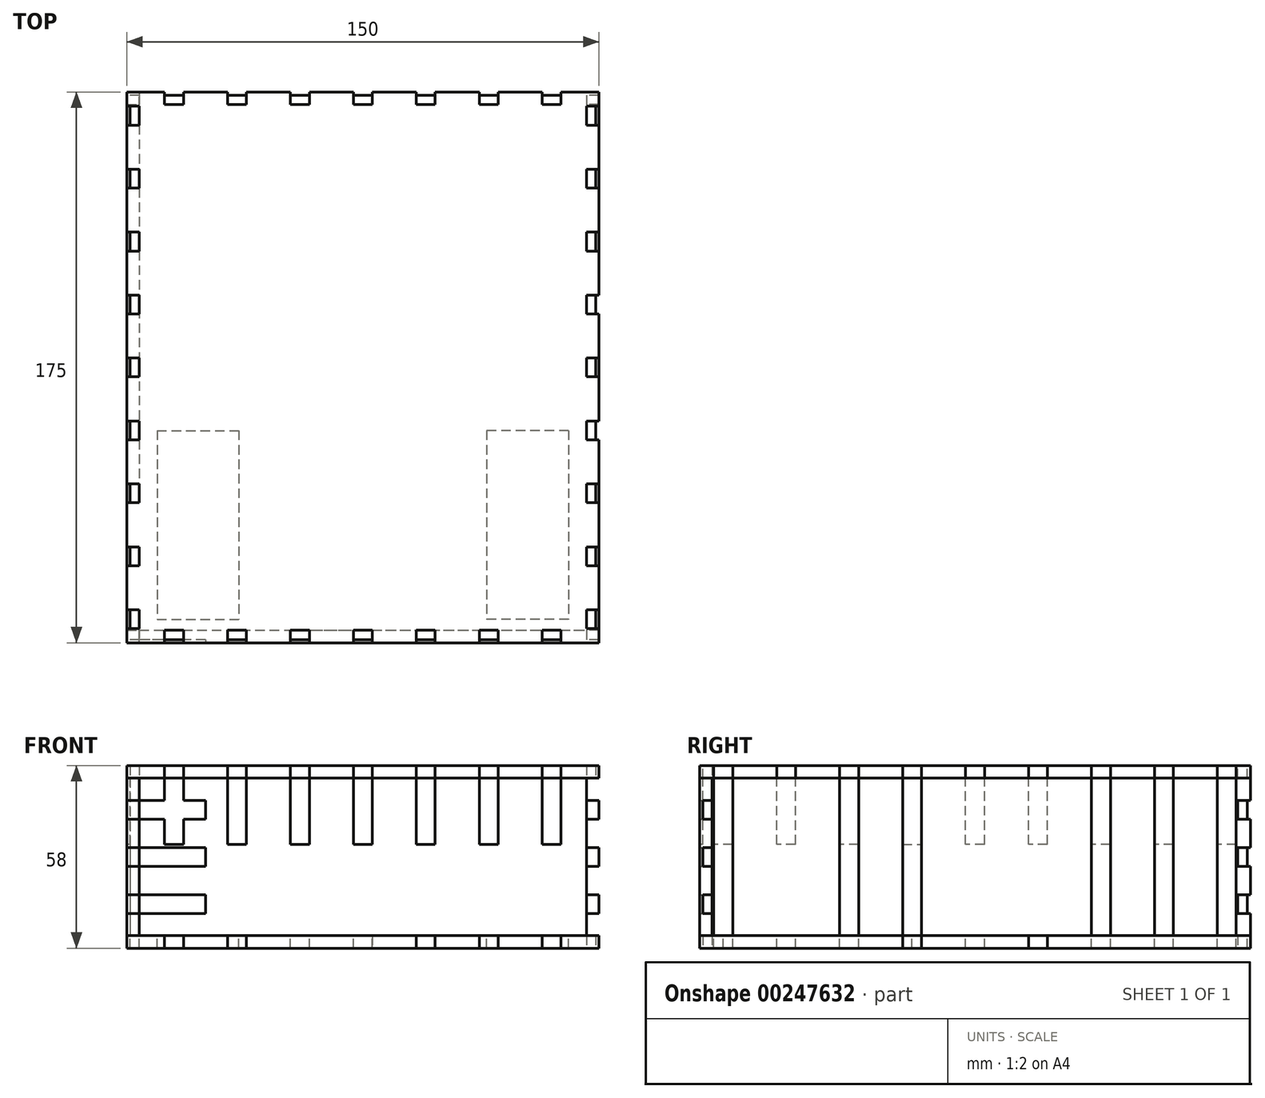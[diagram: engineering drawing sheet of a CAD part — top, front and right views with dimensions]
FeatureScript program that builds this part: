
annotation { "Feature Type Name" : "Feature", "Feature Type Description" : "" }
export const myFeature = defineFeature(function(context is Context, id is Id, definition is map)
    precondition{}
    {
        {
            var Q0;
            Q0=qCreatedBy(makeId("Top.planeOp"),FACE);
            var sketch = newSketch(context, id + "F0", { "sketchPlane" : qUnion([Q0])});
            skLineSegment(sketch, "E0.bottom", {"start": v(-75, 87.5) * mm, "end": v(75, 87.5) * mm});
            skLineSegment(sketch, "E0.top", {"start": v(-75, -87.5) * mm, "end": v(75, -87.5) * mm});
            skLineSegment(sketch, "E0.left", {"start": v(-75, 87.5) * mm, "end": v(-75, -87.5) * mm});
            skLineSegment(sketch, "E0.right", {"start": v(75, 87.5) * mm, "end": v(75, -87.5) * mm});
            skPoint(sketch, "E0.middle", {"position": v(0, 0) * mm});
            skLineSegment(sketch, "E1", {"start": v(-75, 87.5) * mm, "end": v(75, -87.5) * mm, "construction": true});
            skLineSegment(sketch, "E2", {"start": v(-75, 0) * mm, "end": v(75, 0) * mm, "construction": true});
            skLineSegment(sketch, "E3", {"start": v(0, 87.5) * mm, "end": v(0, -87.5) * mm, "construction": true});
            skLineSegment(sketch, "E4.bottom", {"start": v(-74, 3) * mm, "end": v(-71, 3) * mm});
            skLineSegment(sketch, "E4.top", {"start": v(-74, 0) * mm, "end": v(-71, 0) * mm});
            skLineSegment(sketch, "E4.left", {"start": v(-74, 3) * mm, "end": v(-74, 0) * mm});
            skLineSegment(sketch, "E4.right", {"start": v(-71, 3) * mm, "end": v(-71, 0) * mm});
            skLineSegment(sketch, "E5.MirrorCS", {"start": v(-74, -3) * mm, "end": v(-71, -3) * mm});
            skLineSegment(sketch, "E6.MirrorCS", {"start": v(-74, -3) * mm, "end": v(-74, 0) * mm});
            skLineSegment(sketch, "E7.MirrorCS", {"start": v(-71, -3) * mm, "end": v(-71, 0) * mm});
            skLineSegment(sketch, "E8.0.1.0", {"start": v(-74, 23) * mm, "end": v(-71, 23) * mm});
            skLineSegment(sketch, "E8.0.1.1", {"start": v(-74, 23) * mm, "end": v(-74, 20) * mm});
            skLineSegment(sketch, "E8.0.1.2", {"start": v(-74, 17) * mm, "end": v(-74, 20) * mm});
            skLineSegment(sketch, "E8.0.1.3", {"start": v(-74, 17) * mm, "end": v(-71, 17) * mm});
            skLineSegment(sketch, "E8.0.1.4", {"start": v(-71, 17) * mm, "end": v(-71, 20) * mm});
            skLineSegment(sketch, "E8.0.1.5", {"start": v(-71, 23) * mm, "end": v(-71, 20) * mm});
            skLineSegment(sketch, "E8.0.2.0", {"start": v(-74, 43) * mm, "end": v(-71, 43) * mm});
            skLineSegment(sketch, "E8.0.2.1", {"start": v(-74, 43) * mm, "end": v(-74, 40) * mm});
            skLineSegment(sketch, "E8.0.2.2", {"start": v(-74, 37) * mm, "end": v(-74, 40) * mm});
            skLineSegment(sketch, "E8.0.2.3", {"start": v(-74, 37) * mm, "end": v(-71, 37) * mm});
            skLineSegment(sketch, "E8.0.2.4", {"start": v(-71, 37) * mm, "end": v(-71, 40) * mm});
            skLineSegment(sketch, "E8.0.2.5", {"start": v(-71, 43) * mm, "end": v(-71, 40) * mm});
            skLineSegment(sketch, "E8.0.3.0", {"start": v(-74, 63) * mm, "end": v(-71, 63) * mm});
            skLineSegment(sketch, "E8.0.3.1", {"start": v(-74, 63) * mm, "end": v(-74, 60) * mm});
            skLineSegment(sketch, "E8.0.3.2", {"start": v(-74, 57) * mm, "end": v(-74, 60) * mm});
            skLineSegment(sketch, "E8.0.3.3", {"start": v(-74, 57) * mm, "end": v(-71, 57) * mm});
            skLineSegment(sketch, "E8.0.3.4", {"start": v(-71, 57) * mm, "end": v(-71, 60) * mm});
            skLineSegment(sketch, "E8.0.3.5", {"start": v(-71, 63) * mm, "end": v(-71, 60) * mm});
            skLineSegment(sketch, "E8.0.4.0", {"start": v(-74, 83) * mm, "end": v(-71, 83) * mm});
            skLineSegment(sketch, "E8.0.4.1", {"start": v(-74, 83) * mm, "end": v(-74, 80) * mm});
            skLineSegment(sketch, "E8.0.4.2", {"start": v(-74, 77) * mm, "end": v(-74, 80) * mm});
            skLineSegment(sketch, "E8.0.4.3", {"start": v(-74, 77) * mm, "end": v(-71, 77) * mm});
            skLineSegment(sketch, "E8.0.4.4", {"start": v(-71, 77) * mm, "end": v(-71, 80) * mm});
            skLineSegment(sketch, "E8.0.4.5", {"start": v(-71, 83) * mm, "end": v(-71, 80) * mm});
            skLineSegment(sketch, "E8.direction1", {"start": v(-74, 3) * mm, "end": v(-49, 3) * mm, "construction": true});
            skLineSegment(sketch, "E8.direction2", {"start": v(-74, 3) * mm, "end": v(-74, 23) * mm, "construction": true});
            skLineSegment(sketch, "E9.MirrorCS", {"start": v(-74, -17) * mm, "end": v(-71, -17) * mm});
            skLineSegment(sketch, "E10.MirrorCS", {"start": v(-71, -17) * mm, "end": v(-71, -20) * mm});
            skLineSegment(sketch, "E11.MirrorCS", {"start": v(-71, -23) * mm, "end": v(-71, -20) * mm});
            skLineSegment(sketch, "E12.MirrorCS", {"start": v(-74, -23) * mm, "end": v(-71, -23) * mm});
            skLineSegment(sketch, "E13.MirrorCS", {"start": v(-74, -37) * mm, "end": v(-71, -37) * mm});
            skLineSegment(sketch, "E14.MirrorCS", {"start": v(-74, -37) * mm, "end": v(-74, -40) * mm});
            skLineSegment(sketch, "E15.MirrorCS", {"start": v(-74, -43) * mm, "end": v(-74, -40) * mm});
            skLineSegment(sketch, "E16.MirrorCS", {"start": v(-74, -43) * mm, "end": v(-71, -43) * mm});
            skLineSegment(sketch, "E17.MirrorCS", {"start": v(-71, -37) * mm, "end": v(-71, -40) * mm});
            skLineSegment(sketch, "E18.MirrorCS", {"start": v(-71, -43) * mm, "end": v(-71, -40) * mm});
            skLineSegment(sketch, "E19.MirrorCS", {"start": v(-74, -57) * mm, "end": v(-74, -60) * mm});
            skLineSegment(sketch, "E20.MirrorCS", {"start": v(-74, -63) * mm, "end": v(-74, -60) * mm});
            skLineSegment(sketch, "E21.MirrorCS", {"start": v(-74, -63) * mm, "end": v(-71, -63) * mm});
            skLineSegment(sketch, "E22.MirrorCS", {"start": v(-71, -63) * mm, "end": v(-71, -60) * mm});
            skLineSegment(sketch, "E23.MirrorCS", {"start": v(-71, -57) * mm, "end": v(-71, -60) * mm});
            skLineSegment(sketch, "E24.MirrorCS", {"start": v(-74, -57) * mm, "end": v(-71, -57) * mm});
            skLineSegment(sketch, "E25.MirrorCS", {"start": v(-71, -77) * mm, "end": v(-71, -80) * mm});
            skLineSegment(sketch, "E26.MirrorCS", {"start": v(-71, -83) * mm, "end": v(-71, -80) * mm});
            skLineSegment(sketch, "E27.MirrorCS", {"start": v(-74, -83) * mm, "end": v(-71, -83) * mm});
            skLineSegment(sketch, "E28.MirrorCS", {"start": v(-74, -77) * mm, "end": v(-74, -80) * mm});
            skLineSegment(sketch, "E29.MirrorCS", {"start": v(-74, -77) * mm, "end": v(-71, -77) * mm});
            skLineSegment(sketch, "E30.MirrorCS", {"start": v(-74, -83) * mm, "end": v(-74, -80) * mm});
            skLineSegment(sketch, "E31", {"start": v(-74, -23) * mm, "end": v(-74, -17) * mm});
            skLineSegment(sketch, "E32.bottom", {"start": v(0, -83.5) * mm, "end": v(3, -83.5) * mm});
            skLineSegment(sketch, "E32.top", {"start": v(0, -86.5) * mm, "end": v(3, -86.5) * mm});
            skLineSegment(sketch, "E32.left", {"start": v(0, -83.5) * mm, "end": v(0, -86.5) * mm});
            skLineSegment(sketch, "E32.right", {"start": v(3, -83.5) * mm, "end": v(3, -86.5) * mm});
            skLineSegment(sketch, "E33.MirrorCS", {"start": v(0, -83.5) * mm, "end": v(-3, -83.5) * mm});
            skLineSegment(sketch, "E34.MirrorCS", {"start": v(-3, -83.5) * mm, "end": v(-3, -86.5) * mm});
            skLineSegment(sketch, "E35.MirrorCS", {"start": v(0, -86.5) * mm, "end": v(-3, -86.5) * mm});
            skLineSegment(sketch, "E36.1.0.0", {"start": v(20, -83.5) * mm, "end": v(17, -83.5) * mm});
            skLineSegment(sketch, "E36.1.0.1", {"start": v(20, -83.5) * mm, "end": v(23, -83.5) * mm});
            skLineSegment(sketch, "E36.1.0.2", {"start": v(20, -86.5) * mm, "end": v(17, -86.5) * mm});
            skLineSegment(sketch, "E36.1.0.3", {"start": v(17, -83.5) * mm, "end": v(17, -86.5) * mm});
            skLineSegment(sketch, "E36.1.0.4", {"start": v(20, -86.5) * mm, "end": v(23, -86.5) * mm});
            skLineSegment(sketch, "E36.1.0.5", {"start": v(23, -83.5) * mm, "end": v(23, -86.5) * mm});
            skLineSegment(sketch, "E36.2.0.0", {"start": v(40, -83.5) * mm, "end": v(37, -83.5) * mm});
            skLineSegment(sketch, "E36.2.0.1", {"start": v(40, -83.5) * mm, "end": v(43, -83.5) * mm});
            skLineSegment(sketch, "E36.2.0.2", {"start": v(40, -86.5) * mm, "end": v(37, -86.5) * mm});
            skLineSegment(sketch, "E36.2.0.3", {"start": v(37, -83.5) * mm, "end": v(37, -86.5) * mm});
            skLineSegment(sketch, "E36.2.0.4", {"start": v(40, -86.5) * mm, "end": v(43, -86.5) * mm});
            skLineSegment(sketch, "E36.2.0.5", {"start": v(43, -83.5) * mm, "end": v(43, -86.5) * mm});
            skLineSegment(sketch, "E36.3.0.0", {"start": v(60, -83.5) * mm, "end": v(57, -83.5) * mm});
            skLineSegment(sketch, "E36.3.0.1", {"start": v(60, -83.5) * mm, "end": v(63, -83.5) * mm});
            skLineSegment(sketch, "E36.3.0.2", {"start": v(60, -86.5) * mm, "end": v(57, -86.5) * mm});
            skLineSegment(sketch, "E36.3.0.3", {"start": v(57, -83.5) * mm, "end": v(57, -86.5) * mm});
            skLineSegment(sketch, "E36.3.0.4", {"start": v(60, -86.5) * mm, "end": v(63, -86.5) * mm});
            skLineSegment(sketch, "E36.3.0.5", {"start": v(63, -83.5) * mm, "end": v(63, -86.5) * mm});
            skLineSegment(sketch, "E36.direction1", {"start": v(-3, -83.5) * mm, "end": v(17, -83.5) * mm, "construction": true});
            skLineSegment(sketch, "E37.MirrorCS", {"start": v(-20, -83.5) * mm, "end": v(-17, -83.5) * mm});
            skLineSegment(sketch, "E38.MirrorCS", {"start": v(-20, -83.5) * mm, "end": v(-23, -83.5) * mm});
            skLineSegment(sketch, "E39.MirrorCS", {"start": v(-23, -83.5) * mm, "end": v(-23, -86.5) * mm});
            skLineSegment(sketch, "E40.MirrorCS", {"start": v(-20, -86.5) * mm, "end": v(-23, -86.5) * mm});
            skLineSegment(sketch, "E41.MirrorCS", {"start": v(-20, -86.5) * mm, "end": v(-17, -86.5) * mm});
            skLineSegment(sketch, "E42.MirrorCS", {"start": v(-17, -83.5) * mm, "end": v(-17, -86.5) * mm});
            skLineSegment(sketch, "E43.MirrorCS", {"start": v(-40, -83.5) * mm, "end": v(-43, -83.5) * mm});
            skLineSegment(sketch, "E44.MirrorCS", {"start": v(-40, -83.5) * mm, "end": v(-37, -83.5) * mm});
            skLineSegment(sketch, "E45.MirrorCS", {"start": v(-37, -83.5) * mm, "end": v(-37, -86.5) * mm});
            skLineSegment(sketch, "E46.MirrorCS", {"start": v(75, -87.5) * mm, "end": v(-75, -87.5) * mm});
            skLineSegment(sketch, "E47.MirrorCS", {"start": v(-40, -86.5) * mm, "end": v(-37, -86.5) * mm});
            skLineSegment(sketch, "E48.MirrorCS", {"start": v(-40, -86.5) * mm, "end": v(-43, -86.5) * mm});
            skLineSegment(sketch, "E49.MirrorCS", {"start": v(-43, -83.5) * mm, "end": v(-43, -86.5) * mm});
            skLineSegment(sketch, "E50.MirrorCS", {"start": v(-60, -83.5) * mm, "end": v(-57, -83.5) * mm});
            skLineSegment(sketch, "E51.MirrorCS", {"start": v(-60, -83.5) * mm, "end": v(-63, -83.5) * mm});
            skLineSegment(sketch, "E52.MirrorCS", {"start": v(-63, -83.5) * mm, "end": v(-63, -86.5) * mm});
            skLineSegment(sketch, "E53.MirrorCS", {"start": v(-60, -86.5) * mm, "end": v(-63, -86.5) * mm});
            skLineSegment(sketch, "E54.MirrorCS", {"start": v(-60, -86.5) * mm, "end": v(-57, -86.5) * mm});
            skLineSegment(sketch, "E55.MirrorCS", {"start": v(-57, -83.5) * mm, "end": v(-57, -86.5) * mm});
            skLineSegment(sketch, "E56.MirrorCS", {"start": v(74, 83) * mm, "end": v(71, 83) * mm});
            skLineSegment(sketch, "E57.MirrorCS", {"start": v(74, 83) * mm, "end": v(74, 80) * mm});
            skLineSegment(sketch, "E58.MirrorCS", {"start": v(71, 83) * mm, "end": v(71, 80) * mm});
            skLineSegment(sketch, "E59.MirrorCS", {"start": v(71, 77) * mm, "end": v(71, 80) * mm});
            skLineSegment(sketch, "E60.MirrorCS", {"start": v(74, 77) * mm, "end": v(71, 77) * mm});
            skLineSegment(sketch, "E61.MirrorCS", {"start": v(74, 77) * mm, "end": v(74, 80) * mm});
            skLineSegment(sketch, "E62.MirrorCS", {"start": v(74, 63) * mm, "end": v(71, 63) * mm});
            skLineSegment(sketch, "E63.MirrorCS", {"start": v(74, 63) * mm, "end": v(74, 60) * mm});
            skLineSegment(sketch, "E64.MirrorCS", {"start": v(71, 63) * mm, "end": v(71, 60) * mm});
            skLineSegment(sketch, "E65.MirrorCS", {"start": v(71, 57) * mm, "end": v(71, 60) * mm});
            skLineSegment(sketch, "E66.MirrorCS", {"start": v(74, 57) * mm, "end": v(71, 57) * mm});
            skLineSegment(sketch, "E67.MirrorCS", {"start": v(74, 57) * mm, "end": v(74, 60) * mm});
            skLineSegment(sketch, "E68.MirrorCS", {"start": v(74, 43) * mm, "end": v(71, 43) * mm});
            skLineSegment(sketch, "E69.MirrorCS", {"start": v(74, 43) * mm, "end": v(74, 40) * mm});
            skLineSegment(sketch, "E70.MirrorCS", {"start": v(71, 43) * mm, "end": v(71, 40) * mm});
            skLineSegment(sketch, "E71.MirrorCS", {"start": v(71, 37) * mm, "end": v(71, 40) * mm});
            skLineSegment(sketch, "E72.MirrorCS", {"start": v(74, 37) * mm, "end": v(74, 40) * mm});
            skLineSegment(sketch, "E73.MirrorCS", {"start": v(74, 37) * mm, "end": v(71, 37) * mm});
            skLineSegment(sketch, "E74.MirrorCS", {"start": v(74, 23) * mm, "end": v(71, 23) * mm});
            skLineSegment(sketch, "E75.MirrorCS", {"start": v(71, 23) * mm, "end": v(71, 20) * mm});
            skLineSegment(sketch, "E76.MirrorCS", {"start": v(74, 3) * mm, "end": v(74, 23) * mm, "construction": true});
            skLineSegment(sketch, "E77.MirrorCS", {"start": v(74, 17) * mm, "end": v(71, 17) * mm});
            skLineSegment(sketch, "E78.MirrorCS", {"start": v(71, 17) * mm, "end": v(71, 20) * mm});
            skLineSegment(sketch, "E79.MirrorCS", {"start": v(74, 3) * mm, "end": v(49, 3) * mm, "construction": true});
            skLineSegment(sketch, "E80.MirrorCS", {"start": v(74, 3) * mm, "end": v(74, 0) * mm});
            skLineSegment(sketch, "E81.MirrorCS", {"start": v(71, 3) * mm, "end": v(71, 0) * mm});
            skLineSegment(sketch, "E82.MirrorCS", {"start": v(74, -3) * mm, "end": v(71, -3) * mm});
            skLineSegment(sketch, "E83.MirrorCS", {"start": v(74, -3) * mm, "end": v(74, 0) * mm});
            skLineSegment(sketch, "E84.MirrorCS", {"start": v(71, -3) * mm, "end": v(71, 0) * mm});
            skLineSegment(sketch, "E85.MirrorCS", {"start": v(74, -17) * mm, "end": v(71, -17) * mm});
            skLineSegment(sketch, "E86.MirrorCS", {"start": v(74, -23) * mm, "end": v(74, -17) * mm});
            skLineSegment(sketch, "E87.MirrorCS", {"start": v(71, -17) * mm, "end": v(71, -20) * mm});
            skLineSegment(sketch, "E88.MirrorCS", {"start": v(71, -23) * mm, "end": v(71, -20) * mm});
            skLineSegment(sketch, "E89.MirrorCS", {"start": v(74, -23) * mm, "end": v(71, -23) * mm});
            skLineSegment(sketch, "E90.MirrorCS", {"start": v(74, -37) * mm, "end": v(71, -37) * mm});
            skLineSegment(sketch, "E91.MirrorCS", {"start": v(74, -37) * mm, "end": v(74, -40) * mm});
            skLineSegment(sketch, "E92.MirrorCS", {"start": v(71, -37) * mm, "end": v(71, -40) * mm});
            skLineSegment(sketch, "E93.MirrorCS", {"start": v(71, -43) * mm, "end": v(71, -40) * mm});
            skLineSegment(sketch, "E94.MirrorCS", {"start": v(74, -43) * mm, "end": v(74, -40) * mm});
            skLineSegment(sketch, "E95.MirrorCS", {"start": v(74, -43) * mm, "end": v(71, -43) * mm});
            skLineSegment(sketch, "E96.MirrorCS", {"start": v(74, -57) * mm, "end": v(71, -57) * mm});
            skLineSegment(sketch, "E97.MirrorCS", {"start": v(74, -57) * mm, "end": v(74, -60) * mm});
            skLineSegment(sketch, "E98.MirrorCS", {"start": v(74, -63) * mm, "end": v(74, -60) * mm});
            skLineSegment(sketch, "E99.MirrorCS", {"start": v(71, -57) * mm, "end": v(71, -60) * mm});
            skLineSegment(sketch, "E100.MirrorCS", {"start": v(71, -63) * mm, "end": v(71, -60) * mm});
            skLineSegment(sketch, "E101.MirrorCS", {"start": v(74, -63) * mm, "end": v(71, -63) * mm});
            skLineSegment(sketch, "E102.MirrorCS", {"start": v(74, -77) * mm, "end": v(71, -77) * mm});
            skLineSegment(sketch, "E103.MirrorCS", {"start": v(71, -77) * mm, "end": v(71, -80) * mm});
            skLineSegment(sketch, "E104.MirrorCS", {"start": v(74, -77) * mm, "end": v(74, -80) * mm});
            skLineSegment(sketch, "E105.MirrorCS", {"start": v(74, -83) * mm, "end": v(74, -80) * mm});
            skLineSegment(sketch, "E106.MirrorCS", {"start": v(71, -83) * mm, "end": v(71, -80) * mm});
            skLineSegment(sketch, "E107.MirrorCS", {"start": v(74, -83) * mm, "end": v(71, -83) * mm});
            skLineSegment(sketch, "E108", {"start": v(71, 3) * mm, "end": v(74, 3) * mm});
            skLineSegment(sketch, "E109", {"start": v(74, 23) * mm, "end": v(74, 17) * mm});
            skLineSegment(sketch, "E110.MirrorCS", {"start": v(-60, 83.5) * mm, "end": v(-63, 83.5) * mm});
            skLineSegment(sketch, "E111.MirrorCS", {"start": v(-60, 83.5) * mm, "end": v(-57, 83.5) * mm});
            skLineSegment(sketch, "E112.MirrorCS", {"start": v(-57, 83.5) * mm, "end": v(-57, 86.5) * mm});
            skLineSegment(sketch, "E113.MirrorCS", {"start": v(-60, 86.5) * mm, "end": v(-57, 86.5) * mm});
            skLineSegment(sketch, "E114.MirrorCS", {"start": v(-60, 86.5) * mm, "end": v(-63, 86.5) * mm});
            skLineSegment(sketch, "E115.MirrorCS", {"start": v(-63, 83.5) * mm, "end": v(-63, 86.5) * mm});
            skLineSegment(sketch, "E116.MirrorCS", {"start": v(-40, 83.5) * mm, "end": v(-43, 83.5) * mm});
            skLineSegment(sketch, "E117.MirrorCS", {"start": v(-40, 83.5) * mm, "end": v(-37, 83.5) * mm});
            skLineSegment(sketch, "E118.MirrorCS", {"start": v(-37, 83.5) * mm, "end": v(-37, 86.5) * mm});
            skLineSegment(sketch, "E119.MirrorCS", {"start": v(-40, 86.5) * mm, "end": v(-37, 86.5) * mm});
            skLineSegment(sketch, "E120.MirrorCS", {"start": v(-40, 86.5) * mm, "end": v(-43, 86.5) * mm});
            skLineSegment(sketch, "E121.MirrorCS", {"start": v(-43, 83.5) * mm, "end": v(-43, 86.5) * mm});
            skLineSegment(sketch, "E122.MirrorCS", {"start": v(-20, 83.5) * mm, "end": v(-23, 83.5) * mm});
            skLineSegment(sketch, "E123.MirrorCS", {"start": v(-20, 83.5) * mm, "end": v(-17, 83.5) * mm});
            skLineSegment(sketch, "E124.MirrorCS", {"start": v(-17, 83.5) * mm, "end": v(-17, 86.5) * mm});
            skLineSegment(sketch, "E125.MirrorCS", {"start": v(-20, 86.5) * mm, "end": v(-17, 86.5) * mm});
            skLineSegment(sketch, "E126.MirrorCS", {"start": v(-20, 86.5) * mm, "end": v(-23, 86.5) * mm});
            skLineSegment(sketch, "E127.MirrorCS", {"start": v(-23, 83.5) * mm, "end": v(-23, 86.5) * mm});
            skLineSegment(sketch, "E128.MirrorCS", {"start": v(-3, 83.5) * mm, "end": v(17, 83.5) * mm, "construction": true});
            skLineSegment(sketch, "E129.MirrorCS", {"start": v(0, 86.5) * mm, "end": v(3, 86.5) * mm});
            skLineSegment(sketch, "E130.MirrorCS", {"start": v(0, 86.5) * mm, "end": v(-3, 86.5) * mm});
            skLineSegment(sketch, "E131.MirrorCS", {"start": v(-3, 83.5) * mm, "end": v(-3, 86.5) * mm});
            skLineSegment(sketch, "E132.MirrorCS", {"start": v(3, 83.5) * mm, "end": v(3, 86.5) * mm});
            skLineSegment(sketch, "E133.MirrorCS", {"start": v(20, 83.5) * mm, "end": v(17, 83.5) * mm});
            skLineSegment(sketch, "E134.MirrorCS", {"start": v(20, 83.5) * mm, "end": v(23, 83.5) * mm});
            skLineSegment(sketch, "E135.MirrorCS", {"start": v(23, 83.5) * mm, "end": v(23, 86.5) * mm});
            skLineSegment(sketch, "E136.MirrorCS", {"start": v(20, 86.5) * mm, "end": v(23, 86.5) * mm});
            skLineSegment(sketch, "E137.MirrorCS", {"start": v(20, 86.5) * mm, "end": v(17, 86.5) * mm});
            skLineSegment(sketch, "E138.MirrorCS", {"start": v(17, 83.5) * mm, "end": v(17, 86.5) * mm});
            skLineSegment(sketch, "E139.MirrorCS", {"start": v(40, 83.5) * mm, "end": v(37, 83.5) * mm});
            skLineSegment(sketch, "E140.MirrorCS", {"start": v(37, 83.5) * mm, "end": v(37, 86.5) * mm});
            skLineSegment(sketch, "E141.MirrorCS", {"start": v(40, 86.5) * mm, "end": v(37, 86.5) * mm});
            skLineSegment(sketch, "E142.MirrorCS", {"start": v(40, 86.5) * mm, "end": v(43, 86.5) * mm});
            skLineSegment(sketch, "E143.MirrorCS", {"start": v(43, 83.5) * mm, "end": v(43, 86.5) * mm});
            skLineSegment(sketch, "E144.MirrorCS", {"start": v(40, 83.5) * mm, "end": v(43, 83.5) * mm});
            skLineSegment(sketch, "E145.MirrorCS", {"start": v(60, 83.5) * mm, "end": v(57, 83.5) * mm});
            skLineSegment(sketch, "E146.MirrorCS", {"start": v(60, 83.5) * mm, "end": v(63, 83.5) * mm});
            skLineSegment(sketch, "E147.MirrorCS", {"start": v(63, 83.5) * mm, "end": v(63, 86.5) * mm});
            skLineSegment(sketch, "E148.MirrorCS", {"start": v(60, 86.5) * mm, "end": v(63, 86.5) * mm});
            skLineSegment(sketch, "E149.MirrorCS", {"start": v(60, 86.5) * mm, "end": v(57, 86.5) * mm});
            skLineSegment(sketch, "E150.MirrorCS", {"start": v(57, 83.5) * mm, "end": v(57, 86.5) * mm});
            skLineSegment(sketch, "E151", {"start": v(-3, 83.5) * mm, "end": v(3, 83.5) * mm});
            skSolve(sketch);
        }
        {
            var Q0;
            Q0=makeQuery(id+"F0.imprint","IMPRINT",FACE,{"disambiguationData":[TD([[makeQuery(id+"F0.imprint","IMPRINT",EDGE,{"derivedFrom":sQuery(id+"F0.wireOp",EDGE,"E0.bottom")}),-1.0]])]});
            extrude(context, id + "F1", {"entities" : qUnion([Q0]), "depth" : 4 * mm});
        }
        {
            var Q0;
            Q0=makeQuery(id+"F1.opExtrude","CAP_FACE",FACE,{"disambiguationData":[OSD([sQuery(id+"F0.wireOp",EDGE,"E0.bottom"),sQuery(id+"F0.wireOp",EDGE,"E0.left"),sQuery(id+"F0.wireOp",EDGE,"E0.right"),sQuery(id+"F0.wireOp",EDGE,"E4.bottom"),sQuery(id+"F0.wireOp",EDGE,"E4.left"),sQuery(id+"F0.wireOp",EDGE,"E4.right"),sQuery(id+"F0.wireOp",EDGE,"E5.MirrorCS"),sQuery(id+"F0.wireOp",EDGE,"E6.MirrorCS"),sQuery(id+"F0.wireOp",EDGE,"E7.MirrorCS"),sQuery(id+"F0.wireOp",EDGE,"E8.0.1.0"),sQuery(id+"F0.wireOp",EDGE,"E8.0.1.1"),sQuery(id+"F0.wireOp",EDGE,"E8.0.1.2"),sQuery(id+"F0.wireOp",EDGE,"E8.0.1.3"),sQuery(id+"F0.wireOp",EDGE,"E8.0.1.4"),sQuery(id+"F0.wireOp",EDGE,"E8.0.1.5"),sQuery(id+"F0.wireOp",EDGE,"E8.0.2.0"),sQuery(id+"F0.wireOp",EDGE,"E8.0.2.1"),sQuery(id+"F0.wireOp",EDGE,"E8.0.2.2"),sQuery(id+"F0.wireOp",EDGE,"E8.0.2.3"),sQuery(id+"F0.wireOp",EDGE,"E8.0.2.4"),sQuery(id+"F0.wireOp",EDGE,"E8.0.2.5"),sQuery(id+"F0.wireOp",EDGE,"E8.0.3.0"),sQuery(id+"F0.wireOp",EDGE,"E8.0.3.1"),sQuery(id+"F0.wireOp",EDGE,"E8.0.3.2"),sQuery(id+"F0.wireOp",EDGE,"E8.0.3.3"),sQuery(id+"F0.wireOp",EDGE,"E8.0.3.4"),sQuery(id+"F0.wireOp",EDGE,"E8.0.3.5"),sQuery(id+"F0.wireOp",EDGE,"E8.0.4.0"),sQuery(id+"F0.wireOp",EDGE,"E8.0.4.1"),sQuery(id+"F0.wireOp",EDGE,"E8.0.4.2"),sQuery(id+"F0.wireOp",EDGE,"E8.0.4.3"),sQuery(id+"F0.wireOp",EDGE,"E8.0.4.4"),sQuery(id+"F0.wireOp",EDGE,"E8.0.4.5"),sQuery(id+"F0.wireOp",EDGE,"E9.MirrorCS"),sQuery(id+"F0.wireOp",EDGE,"E10.MirrorCS"),sQuery(id+"F0.wireOp",EDGE,"E11.MirrorCS"),sQuery(id+"F0.wireOp",EDGE,"E12.MirrorCS"),sQuery(id+"F0.wireOp",EDGE,"E13.MirrorCS"),sQuery(id+"F0.wireOp",EDGE,"E14.MirrorCS"),sQuery(id+"F0.wireOp",EDGE,"E15.MirrorCS"),sQuery(id+"F0.wireOp",EDGE,"E16.MirrorCS"),sQuery(id+"F0.wireOp",EDGE,"E17.MirrorCS"),sQuery(id+"F0.wireOp",EDGE,"E18.MirrorCS"),sQuery(id+"F0.wireOp",EDGE,"E19.MirrorCS"),sQuery(id+"F0.wireOp",EDGE,"E20.MirrorCS"),sQuery(id+"F0.wireOp",EDGE,"E21.MirrorCS"),sQuery(id+"F0.wireOp",EDGE,"E22.MirrorCS"),sQuery(id+"F0.wireOp",EDGE,"E23.MirrorCS"),sQuery(id+"F0.wireOp",EDGE,"E24.MirrorCS"),sQuery(id+"F0.wireOp",EDGE,"E25.MirrorCS"),sQuery(id+"F0.wireOp",EDGE,"E26.MirrorCS"),sQuery(id+"F0.wireOp",EDGE,"E27.MirrorCS"),sQuery(id+"F0.wireOp",EDGE,"E28.MirrorCS"),sQuery(id+"F0.wireOp",EDGE,"E29.MirrorCS"),sQuery(id+"F0.wireOp",EDGE,"E30.MirrorCS"),sQuery(id+"F0.wireOp",EDGE,"E31"),sQuery(id+"F0.wireOp",EDGE,"E32.bottom"),sQuery(id+"F0.wireOp",EDGE,"E32.top"),sQuery(id+"F0.wireOp",EDGE,"E32.right"),sQuery(id+"F0.wireOp",EDGE,"E33.MirrorCS"),sQuery(id+"F0.wireOp",EDGE,"E34.MirrorCS"),sQuery(id+"F0.wireOp",EDGE,"E35.MirrorCS"),sQuery(id+"F0.wireOp",EDGE,"E36.1.0.0"),sQuery(id+"F0.wireOp",EDGE,"E36.1.0.1"),sQuery(id+"F0.wireOp",EDGE,"E36.1.0.2"),sQuery(id+"F0.wireOp",EDGE,"E36.1.0.3"),sQuery(id+"F0.wireOp",EDGE,"E36.1.0.4"),sQuery(id+"F0.wireOp",EDGE,"E36.1.0.5"),sQuery(id+"F0.wireOp",EDGE,"E36.2.0.0"),sQuery(id+"F0.wireOp",EDGE,"E36.2.0.1"),sQuery(id+"F0.wireOp",EDGE,"E36.2.0.2"),sQuery(id+"F0.wireOp",EDGE,"E36.2.0.3"),sQuery(id+"F0.wireOp",EDGE,"E36.2.0.4"),sQuery(id+"F0.wireOp",EDGE,"E36.2.0.5"),sQuery(id+"F0.wireOp",EDGE,"E36.3.0.0"),sQuery(id+"F0.wireOp",EDGE,"E36.3.0.1"),sQuery(id+"F0.wireOp",EDGE,"E36.3.0.2"),sQuery(id+"F0.wireOp",EDGE,"E36.3.0.3"),sQuery(id+"F0.wireOp",EDGE,"E36.3.0.4"),sQuery(id+"F0.wireOp",EDGE,"E36.3.0.5"),sQuery(id+"F0.wireOp",EDGE,"E37.MirrorCS"),sQuery(id+"F0.wireOp",EDGE,"E38.MirrorCS"),sQuery(id+"F0.wireOp",EDGE,"E39.MirrorCS"),sQuery(id+"F0.wireOp",EDGE,"E40.MirrorCS"),sQuery(id+"F0.wireOp",EDGE,"E41.MirrorCS"),sQuery(id+"F0.wireOp",EDGE,"E42.MirrorCS"),sQuery(id+"F0.wireOp",EDGE,"E43.MirrorCS"),sQuery(id+"F0.wireOp",EDGE,"E44.MirrorCS"),sQuery(id+"F0.wireOp",EDGE,"E45.MirrorCS"),sQuery(id+"F0.wireOp",EDGE,"E46.MirrorCS"),sQuery(id+"F0.wireOp",EDGE,"E47.MirrorCS"),sQuery(id+"F0.wireOp",EDGE,"E48.MirrorCS"),sQuery(id+"F0.wireOp",EDGE,"E49.MirrorCS"),sQuery(id+"F0.wireOp",EDGE,"E50.MirrorCS"),sQuery(id+"F0.wireOp",EDGE,"E51.MirrorCS"),sQuery(id+"F0.wireOp",EDGE,"E52.MirrorCS"),sQuery(id+"F0.wireOp",EDGE,"E53.MirrorCS"),sQuery(id+"F0.wireOp",EDGE,"E54.MirrorCS"),sQuery(id+"F0.wireOp",EDGE,"E55.MirrorCS"),sQuery(id+"F0.wireOp",EDGE,"E56.MirrorCS"),sQuery(id+"F0.wireOp",EDGE,"E57.MirrorCS"),sQuery(id+"F0.wireOp",EDGE,"E58.MirrorCS"),sQuery(id+"F0.wireOp",EDGE,"E59.MirrorCS"),sQuery(id+"F0.wireOp",EDGE,"E60.MirrorCS"),sQuery(id+"F0.wireOp",EDGE,"E61.MirrorCS"),sQuery(id+"F0.wireOp",EDGE,"E62.MirrorCS"),sQuery(id+"F0.wireOp",EDGE,"E63.MirrorCS"),sQuery(id+"F0.wireOp",EDGE,"E64.MirrorCS"),sQuery(id+"F0.wireOp",EDGE,"E65.MirrorCS"),sQuery(id+"F0.wireOp",EDGE,"E66.MirrorCS"),sQuery(id+"F0.wireOp",EDGE,"E67.MirrorCS"),sQuery(id+"F0.wireOp",EDGE,"E68.MirrorCS"),sQuery(id+"F0.wireOp",EDGE,"E69.MirrorCS"),sQuery(id+"F0.wireOp",EDGE,"E70.MirrorCS"),sQuery(id+"F0.wireOp",EDGE,"E71.MirrorCS"),sQuery(id+"F0.wireOp",EDGE,"E72.MirrorCS"),sQuery(id+"F0.wireOp",EDGE,"E73.MirrorCS"),sQuery(id+"F0.wireOp",EDGE,"E74.MirrorCS"),sQuery(id+"F0.wireOp",EDGE,"E75.MirrorCS"),sQuery(id+"F0.wireOp",EDGE,"E77.MirrorCS"),sQuery(id+"F0.wireOp",EDGE,"E78.MirrorCS"),sQuery(id+"F0.wireOp",EDGE,"E80.MirrorCS"),sQuery(id+"F0.wireOp",EDGE,"E81.MirrorCS"),sQuery(id+"F0.wireOp",EDGE,"E82.MirrorCS"),sQuery(id+"F0.wireOp",EDGE,"E83.MirrorCS"),sQuery(id+"F0.wireOp",EDGE,"E84.MirrorCS"),sQuery(id+"F0.wireOp",EDGE,"E85.MirrorCS"),sQuery(id+"F0.wireOp",EDGE,"E86.MirrorCS"),sQuery(id+"F0.wireOp",EDGE,"E87.MirrorCS"),sQuery(id+"F0.wireOp",EDGE,"E88.MirrorCS"),sQuery(id+"F0.wireOp",EDGE,"E89.MirrorCS"),sQuery(id+"F0.wireOp",EDGE,"E90.MirrorCS"),sQuery(id+"F0.wireOp",EDGE,"E91.MirrorCS"),sQuery(id+"F0.wireOp",EDGE,"E92.MirrorCS"),sQuery(id+"F0.wireOp",EDGE,"E93.MirrorCS"),sQuery(id+"F0.wireOp",EDGE,"E94.MirrorCS"),sQuery(id+"F0.wireOp",EDGE,"E95.MirrorCS"),sQuery(id+"F0.wireOp",EDGE,"E96.MirrorCS"),sQuery(id+"F0.wireOp",EDGE,"E97.MirrorCS"),sQuery(id+"F0.wireOp",EDGE,"E98.MirrorCS"),sQuery(id+"F0.wireOp",EDGE,"E99.MirrorCS"),sQuery(id+"F0.wireOp",EDGE,"E100.MirrorCS"),sQuery(id+"F0.wireOp",EDGE,"E101.MirrorCS"),sQuery(id+"F0.wireOp",EDGE,"E102.MirrorCS"),sQuery(id+"F0.wireOp",EDGE,"E103.MirrorCS"),sQuery(id+"F0.wireOp",EDGE,"E104.MirrorCS"),sQuery(id+"F0.wireOp",EDGE,"E105.MirrorCS"),sQuery(id+"F0.wireOp",EDGE,"E106.MirrorCS"),sQuery(id+"F0.wireOp",EDGE,"E107.MirrorCS"),sQuery(id+"F0.wireOp",EDGE,"E108"),sQuery(id+"F0.wireOp",EDGE,"E109"),sQuery(id+"F0.wireOp",EDGE,"E110.MirrorCS"),sQuery(id+"F0.wireOp",EDGE,"E111.MirrorCS"),sQuery(id+"F0.wireOp",EDGE,"E112.MirrorCS"),sQuery(id+"F0.wireOp",EDGE,"E113.MirrorCS"),sQuery(id+"F0.wireOp",EDGE,"E114.MirrorCS"),sQuery(id+"F0.wireOp",EDGE,"E115.MirrorCS"),sQuery(id+"F0.wireOp",EDGE,"E116.MirrorCS"),sQuery(id+"F0.wireOp",EDGE,"E117.MirrorCS"),sQuery(id+"F0.wireOp",EDGE,"E118.MirrorCS"),sQuery(id+"F0.wireOp",EDGE,"E119.MirrorCS"),sQuery(id+"F0.wireOp",EDGE,"E120.MirrorCS"),sQuery(id+"F0.wireOp",EDGE,"E121.MirrorCS"),sQuery(id+"F0.wireOp",EDGE,"E122.MirrorCS"),sQuery(id+"F0.wireOp",EDGE,"E123.MirrorCS"),sQuery(id+"F0.wireOp",EDGE,"E124.MirrorCS"),sQuery(id+"F0.wireOp",EDGE,"E125.MirrorCS"),sQuery(id+"F0.wireOp",EDGE,"E126.MirrorCS"),sQuery(id+"F0.wireOp",EDGE,"E127.MirrorCS"),sQuery(id+"F0.wireOp",EDGE,"E129.MirrorCS"),sQuery(id+"F0.wireOp",EDGE,"E130.MirrorCS"),sQuery(id+"F0.wireOp",EDGE,"E131.MirrorCS"),sQuery(id+"F0.wireOp",EDGE,"E132.MirrorCS"),sQuery(id+"F0.wireOp",EDGE,"E133.MirrorCS"),sQuery(id+"F0.wireOp",EDGE,"E134.MirrorCS"),sQuery(id+"F0.wireOp",EDGE,"E135.MirrorCS"),sQuery(id+"F0.wireOp",EDGE,"E136.MirrorCS"),sQuery(id+"F0.wireOp",EDGE,"E137.MirrorCS"),sQuery(id+"F0.wireOp",EDGE,"E138.MirrorCS"),sQuery(id+"F0.wireOp",EDGE,"E139.MirrorCS"),sQuery(id+"F0.wireOp",EDGE,"E140.MirrorCS"),sQuery(id+"F0.wireOp",EDGE,"E141.MirrorCS"),sQuery(id+"F0.wireOp",EDGE,"E142.MirrorCS"),sQuery(id+"F0.wireOp",EDGE,"E143.MirrorCS"),sQuery(id+"F0.wireOp",EDGE,"E144.MirrorCS"),sQuery(id+"F0.wireOp",EDGE,"E145.MirrorCS"),sQuery(id+"F0.wireOp",EDGE,"E146.MirrorCS"),sQuery(id+"F0.wireOp",EDGE,"E147.MirrorCS"),sQuery(id+"F0.wireOp",EDGE,"E148.MirrorCS"),sQuery(id+"F0.wireOp",EDGE,"E149.MirrorCS"),sQuery(id+"F0.wireOp",EDGE,"E150.MirrorCS"),sQuery(id+"F0.wireOp",EDGE,"E151")])],"isStart":false});
            var sketch = newSketch(context, id + "F2", { "sketchPlane" : qUnion([Q0])});
            skPoint(sketch, "E152.0", {"position": v(-71, 83) * mm});
            skLineSegment(sketch, "E153", {"start": v(-71, 83) * mm, "end": v(-71, 87.5) * mm});
            skPoint(sketch, "E154.0", {"position": v(-71, -83) * mm});
            skLineSegment(sketch, "E155", {"start": v(-71, 83) * mm, "end": v(-71, -83) * mm});
            skLineSegment(sketch, "E156", {"start": v(-71, -83) * mm, "end": v(-71, -87.64) * mm});
            skLineSegment(sketch, "E157", {"start": v(0, 87.45) * mm, "end": v(0, -91.1) * mm, "construction": true});
            skLineSegment(sketch, "E158.MirrorCS", {"start": v(71, 83) * mm, "end": v(71, -83) * mm});
            skLineSegment(sketch, "E159.MirrorCS", {"start": v(71, 83) * mm, "end": v(71, 87.5) * mm});
            skLineSegment(sketch, "E160.MirrorCS", {"start": v(71, -83) * mm, "end": v(71, -87.64) * mm});
            skPoint(sketch, "E161", {"position": v(-63, 83.5) * mm});
            skPoint(sketch, "E162", {"position": v(63, 83.5) * mm});
            skLineSegment(sketch, "E163", {"start": v(63, 83.5) * mm, "end": v(71, 83.5) * mm});
            skLineSegment(sketch, "E164", {"start": v(63, 83.5) * mm, "end": v(-23, 83.5) * mm});
            skLineSegment(sketch, "E165", {"start": v(-23, 83.5) * mm, "end": v(-71, 83.5) * mm});
            skLineSegment(sketch, "E166.MirrorCS", {"start": v(0, 167) * mm, "end": v(-82.49, 167) * mm, "construction": true});
            skLineSegment(sketch, "E167", {"start": v(-82.49, 0) * mm, "end": v(75.5, 0) * mm, "construction": true});
            skLineSegment(sketch, "E168.MirrorCS", {"start": v(63, -83.5) * mm, "end": v(-23, -83.5) * mm});
            skLineSegment(sketch, "E169.MirrorCS", {"start": v(-23, -83.5) * mm, "end": v(-71, -83.5) * mm});
            skLineSegment(sketch, "E170.MirrorCS", {"start": v(63, -83.5) * mm, "end": v(71, -83.5) * mm});
            skSolve(sketch);
        }
        {
            var Q0;
            {var subQ8=sQuery(id+"F2.wireOp",EDGE,"E163");Q0=makeQuery(id+"F2.imprint","IMPRINT",FACE,{"disambiguationData":[TD([[makeQuery(id+"F2.imprint","IMPRINT",EDGE,{"derivedFrom":subQ8}),-1.0]])]});}
            var sketch = newSketch(context, id + "F3", { "sketchPlane" : qUnion([Q0])});
            skLineSegment(sketch, "E171.0.0", {"start": v(71, 77) * mm, "end": v(74, 77) * mm});
            skLineSegment(sketch, "E171.0.1", {"start": v(74, 77) * mm, "end": v(74, 83) * mm});
            skLineSegment(sketch, "E171.0.2", {"start": v(74, 83) * mm, "end": v(71, 83) * mm});
            skLineSegment(sketch, "E171.0.3", {"start": v(71, 83) * mm, "end": v(71, 77) * mm});
            skLineSegment(sketch, "E172.0.0", {"start": v(71, 57) * mm, "end": v(74, 57) * mm});
            skLineSegment(sketch, "E172.0.1", {"start": v(74, 57) * mm, "end": v(74, 63) * mm});
            skLineSegment(sketch, "E172.0.2", {"start": v(74, 63) * mm, "end": v(71, 63) * mm});
            skLineSegment(sketch, "E172.0.3", {"start": v(71, 63) * mm, "end": v(71, 57) * mm});
            skLineSegment(sketch, "E173.0.0", {"start": v(71, 37) * mm, "end": v(74, 37) * mm});
            skLineSegment(sketch, "E173.0.1", {"start": v(74, 37) * mm, "end": v(74, 43) * mm});
            skLineSegment(sketch, "E173.0.2", {"start": v(74, 43) * mm, "end": v(71, 43) * mm});
            skLineSegment(sketch, "E173.0.3", {"start": v(71, 43) * mm, "end": v(71, 37) * mm});
            skLineSegment(sketch, "E174.0.0", {"start": v(74, 17) * mm, "end": v(74, 23) * mm});
            skLineSegment(sketch, "E174.0.1", {"start": v(74, 23) * mm, "end": v(71, 23) * mm});
            skLineSegment(sketch, "E174.0.2", {"start": v(71, 23) * mm, "end": v(71, 17) * mm});
            skLineSegment(sketch, "E174.0.3", {"start": v(71, 17) * mm, "end": v(74, 17) * mm});
            skLineSegment(sketch, "E175.0.0", {"start": v(71, -3) * mm, "end": v(74, -3) * mm});
            skLineSegment(sketch, "E175.0.1", {"start": v(74, -3) * mm, "end": v(74, 3) * mm});
            skLineSegment(sketch, "E175.0.2", {"start": v(74, 3) * mm, "end": v(71, 3) * mm});
            skLineSegment(sketch, "E175.0.3", {"start": v(71, 3) * mm, "end": v(71, -3) * mm});
            skLineSegment(sketch, "E176.0.0", {"start": v(71, -23) * mm, "end": v(74, -23) * mm});
            skLineSegment(sketch, "E176.0.1", {"start": v(74, -23) * mm, "end": v(74, -17) * mm});
            skLineSegment(sketch, "E176.0.2", {"start": v(74, -17) * mm, "end": v(71, -17) * mm});
            skLineSegment(sketch, "E176.0.3", {"start": v(71, -17) * mm, "end": v(71, -23) * mm});
            skLineSegment(sketch, "E177.0.0", {"start": v(71, -43) * mm, "end": v(74, -43) * mm});
            skLineSegment(sketch, "E177.0.1", {"start": v(74, -43) * mm, "end": v(74, -37) * mm});
            skLineSegment(sketch, "E177.0.2", {"start": v(74, -37) * mm, "end": v(71, -37) * mm});
            skLineSegment(sketch, "E177.0.3", {"start": v(71, -37) * mm, "end": v(71, -43) * mm});
            skLineSegment(sketch, "E178.0.0", {"start": v(71, -63) * mm, "end": v(74, -63) * mm});
            skLineSegment(sketch, "E178.0.1", {"start": v(74, -63) * mm, "end": v(74, -57) * mm});
            skLineSegment(sketch, "E178.0.2", {"start": v(74, -57) * mm, "end": v(71, -57) * mm});
            skLineSegment(sketch, "E178.0.3", {"start": v(71, -57) * mm, "end": v(71, -63) * mm});
            skLineSegment(sketch, "E179.0.0", {"start": v(71, -83) * mm, "end": v(74, -83) * mm});
            skLineSegment(sketch, "E179.0.1", {"start": v(74, -83) * mm, "end": v(74, -77) * mm});
            skLineSegment(sketch, "E179.0.2", {"start": v(74, -77) * mm, "end": v(71, -77) * mm});
            skLineSegment(sketch, "E179.0.3", {"start": v(71, -77) * mm, "end": v(71, -83) * mm});
            skLineSegment(sketch, "E180.0.0", {"start": v(57, -83.5) * mm, "end": v(57, -86.5) * mm});
            skLineSegment(sketch, "E180.0.1", {"start": v(57, -86.5) * mm, "end": v(63, -86.5) * mm});
            skLineSegment(sketch, "E180.0.2", {"start": v(63, -86.5) * mm, "end": v(63, -83.5) * mm});
            skLineSegment(sketch, "E180.0.3", {"start": v(63, -83.5) * mm, "end": v(57, -83.5) * mm});
            skLineSegment(sketch, "E181.0.0", {"start": v(37, -83.5) * mm, "end": v(37, -86.5) * mm});
            skLineSegment(sketch, "E181.0.1", {"start": v(37, -86.5) * mm, "end": v(43, -86.5) * mm});
            skLineSegment(sketch, "E181.0.2", {"start": v(43, -86.5) * mm, "end": v(43, -83.5) * mm});
            skLineSegment(sketch, "E181.0.3", {"start": v(43, -83.5) * mm, "end": v(37, -83.5) * mm});
            skLineSegment(sketch, "E182.0.0", {"start": v(17, -83.5) * mm, "end": v(17, -86.5) * mm});
            skLineSegment(sketch, "E182.0.1", {"start": v(17, -86.5) * mm, "end": v(23, -86.5) * mm});
            skLineSegment(sketch, "E182.0.2", {"start": v(23, -86.5) * mm, "end": v(23, -83.5) * mm});
            skLineSegment(sketch, "E182.0.3", {"start": v(23, -83.5) * mm, "end": v(17, -83.5) * mm});
            skLineSegment(sketch, "E183.0.0", {"start": v(3, -86.5) * mm, "end": v(3, -83.5) * mm});
            skLineSegment(sketch, "E183.0.1", {"start": v(3, -83.5) * mm, "end": v(-3, -83.5) * mm});
            skLineSegment(sketch, "E183.0.2", {"start": v(-3, -83.5) * mm, "end": v(-3, -86.5) * mm});
            skLineSegment(sketch, "E183.0.3", {"start": v(-3, -86.5) * mm, "end": v(3, -86.5) * mm});
            skLineSegment(sketch, "E184.0.0", {"start": v(-17, -83.5) * mm, "end": v(-23, -83.5) * mm});
            skLineSegment(sketch, "E184.0.1", {"start": v(-23, -83.5) * mm, "end": v(-23, -86.5) * mm});
            skLineSegment(sketch, "E184.0.2", {"start": v(-23, -86.5) * mm, "end": v(-17, -86.5) * mm});
            skLineSegment(sketch, "E184.0.3", {"start": v(-17, -86.5) * mm, "end": v(-17, -83.5) * mm});
            skLineSegment(sketch, "E185.0.0", {"start": v(-37, -83.5) * mm, "end": v(-43, -83.5) * mm});
            skLineSegment(sketch, "E185.0.1", {"start": v(-43, -83.5) * mm, "end": v(-43, -86.5) * mm});
            skLineSegment(sketch, "E185.0.2", {"start": v(-43, -86.5) * mm, "end": v(-37, -86.5) * mm});
            skLineSegment(sketch, "E185.0.3", {"start": v(-37, -86.5) * mm, "end": v(-37, -83.5) * mm});
            skLineSegment(sketch, "E186.0.0", {"start": v(-57, -83.5) * mm, "end": v(-63, -83.5) * mm});
            skLineSegment(sketch, "E186.0.1", {"start": v(-63, -83.5) * mm, "end": v(-63, -86.5) * mm});
            skLineSegment(sketch, "E186.0.2", {"start": v(-63, -86.5) * mm, "end": v(-57, -86.5) * mm});
            skLineSegment(sketch, "E186.0.3", {"start": v(-57, -86.5) * mm, "end": v(-57, -83.5) * mm});
            skLineSegment(sketch, "E187.0.0", {"start": v(-71, -77) * mm, "end": v(-74, -77) * mm});
            skLineSegment(sketch, "E187.0.1", {"start": v(-74, -77) * mm, "end": v(-74, -83) * mm});
            skLineSegment(sketch, "E187.0.2", {"start": v(-74, -83) * mm, "end": v(-71, -83) * mm});
            skLineSegment(sketch, "E187.0.3", {"start": v(-71, -83) * mm, "end": v(-71, -77) * mm});
            skLineSegment(sketch, "E188.0.0", {"start": v(-71, -57) * mm, "end": v(-74, -57) * mm});
            skLineSegment(sketch, "E188.0.1", {"start": v(-74, -57) * mm, "end": v(-74, -63) * mm});
            skLineSegment(sketch, "E188.0.2", {"start": v(-74, -63) * mm, "end": v(-71, -63) * mm});
            skLineSegment(sketch, "E188.0.3", {"start": v(-71, -63) * mm, "end": v(-71, -57) * mm});
            skLineSegment(sketch, "E189.0.0", {"start": v(-74, -43) * mm, "end": v(-71, -43) * mm});
            skLineSegment(sketch, "E189.0.1", {"start": v(-71, -43) * mm, "end": v(-71, -37) * mm});
            skLineSegment(sketch, "E189.0.2", {"start": v(-71, -37) * mm, "end": v(-74, -37) * mm});
            skLineSegment(sketch, "E189.0.3", {"start": v(-74, -37) * mm, "end": v(-74, -43) * mm});
            skLineSegment(sketch, "E190.0.0", {"start": v(-74, -17) * mm, "end": v(-74, -23) * mm});
            skLineSegment(sketch, "E190.0.1", {"start": v(-74, -23) * mm, "end": v(-71, -23) * mm});
            skLineSegment(sketch, "E190.0.2", {"start": v(-71, -23) * mm, "end": v(-71, -17) * mm});
            skLineSegment(sketch, "E190.0.3", {"start": v(-71, -17) * mm, "end": v(-74, -17) * mm});
            skLineSegment(sketch, "E191.0.0", {"start": v(-74, 3) * mm, "end": v(-74, -3) * mm});
            skLineSegment(sketch, "E191.0.1", {"start": v(-74, -3) * mm, "end": v(-71, -3) * mm});
            skLineSegment(sketch, "E191.0.2", {"start": v(-71, -3) * mm, "end": v(-71, 3) * mm});
            skLineSegment(sketch, "E191.0.3", {"start": v(-71, 3) * mm, "end": v(-74, 3) * mm});
            skLineSegment(sketch, "E192.0.0", {"start": v(-71, 23) * mm, "end": v(-74, 23) * mm});
            skLineSegment(sketch, "E192.0.1", {"start": v(-74, 23) * mm, "end": v(-74, 17) * mm});
            skLineSegment(sketch, "E192.0.2", {"start": v(-74, 17) * mm, "end": v(-71, 17) * mm});
            skLineSegment(sketch, "E192.0.3", {"start": v(-71, 17) * mm, "end": v(-71, 23) * mm});
            skLineSegment(sketch, "E193.0.0", {"start": v(-71, 43) * mm, "end": v(-74, 43) * mm});
            skLineSegment(sketch, "E193.0.1", {"start": v(-74, 43) * mm, "end": v(-74, 37) * mm});
            skLineSegment(sketch, "E193.0.2", {"start": v(-74, 37) * mm, "end": v(-71, 37) * mm});
            skLineSegment(sketch, "E193.0.3", {"start": v(-71, 37) * mm, "end": v(-71, 43) * mm});
            skLineSegment(sketch, "E194.0.0", {"start": v(-71, 63) * mm, "end": v(-74, 63) * mm});
            skLineSegment(sketch, "E194.0.1", {"start": v(-74, 63) * mm, "end": v(-74, 57) * mm});
            skLineSegment(sketch, "E194.0.2", {"start": v(-74, 57) * mm, "end": v(-71, 57) * mm});
            skLineSegment(sketch, "E194.0.3", {"start": v(-71, 57) * mm, "end": v(-71, 63) * mm});
            skLineSegment(sketch, "E195.0.0", {"start": v(-71, 83) * mm, "end": v(-74, 83) * mm});
            skLineSegment(sketch, "E195.0.1", {"start": v(-74, 83) * mm, "end": v(-74, 77) * mm});
            skLineSegment(sketch, "E195.0.2", {"start": v(-74, 77) * mm, "end": v(-71, 77) * mm});
            skLineSegment(sketch, "E195.0.3", {"start": v(-71, 77) * mm, "end": v(-71, 83) * mm});
            skLineSegment(sketch, "E196.0.0", {"start": v(-63, 83.5) * mm, "end": v(-57, 83.5) * mm});
            skLineSegment(sketch, "E196.0.1", {"start": v(-57, 83.5) * mm, "end": v(-57, 86.5) * mm});
            skLineSegment(sketch, "E196.0.2", {"start": v(-57, 86.5) * mm, "end": v(-63, 86.5) * mm});
            skLineSegment(sketch, "E196.0.3", {"start": v(-63, 86.5) * mm, "end": v(-63, 83.5) * mm});
            skLineSegment(sketch, "E197.0.0", {"start": v(-43, 83.5) * mm, "end": v(-37, 83.5) * mm});
            skLineSegment(sketch, "E197.0.1", {"start": v(-37, 83.5) * mm, "end": v(-37, 86.5) * mm});
            skLineSegment(sketch, "E197.0.2", {"start": v(-37, 86.5) * mm, "end": v(-43, 86.5) * mm});
            skLineSegment(sketch, "E197.0.3", {"start": v(-43, 86.5) * mm, "end": v(-43, 83.5) * mm});
            skLineSegment(sketch, "E198.0.0", {"start": v(-23, 83.5) * mm, "end": v(-17, 83.5) * mm});
            skLineSegment(sketch, "E198.0.1", {"start": v(-17, 83.5) * mm, "end": v(-17, 86.5) * mm});
            skLineSegment(sketch, "E198.0.2", {"start": v(-17, 86.5) * mm, "end": v(-23, 86.5) * mm});
            skLineSegment(sketch, "E198.0.3", {"start": v(-23, 86.5) * mm, "end": v(-23, 83.5) * mm});
            skLineSegment(sketch, "E199.0.0", {"start": v(-3, 86.5) * mm, "end": v(-3, 83.5) * mm});
            skLineSegment(sketch, "E199.0.1", {"start": v(-3, 83.5) * mm, "end": v(3, 83.5) * mm});
            skLineSegment(sketch, "E199.0.2", {"start": v(3, 83.5) * mm, "end": v(3, 86.5) * mm});
            skLineSegment(sketch, "E199.0.3", {"start": v(3, 86.5) * mm, "end": v(-3, 86.5) * mm});
            skLineSegment(sketch, "E200.0.0", {"start": v(17, 83.5) * mm, "end": v(23, 83.5) * mm});
            skLineSegment(sketch, "E200.0.1", {"start": v(23, 83.5) * mm, "end": v(23, 86.5) * mm});
            skLineSegment(sketch, "E200.0.2", {"start": v(23, 86.5) * mm, "end": v(17, 86.5) * mm});
            skLineSegment(sketch, "E200.0.3", {"start": v(17, 86.5) * mm, "end": v(17, 83.5) * mm});
            skLineSegment(sketch, "E201.0.0", {"start": v(37, 86.5) * mm, "end": v(37, 83.5) * mm});
            skLineSegment(sketch, "E201.0.1", {"start": v(37, 83.5) * mm, "end": v(43, 83.5) * mm});
            skLineSegment(sketch, "E201.0.2", {"start": v(43, 83.5) * mm, "end": v(43, 86.5) * mm});
            skLineSegment(sketch, "E201.0.3", {"start": v(43, 86.5) * mm, "end": v(37, 86.5) * mm});
            skLineSegment(sketch, "E202.0.0", {"start": v(57, 83.5) * mm, "end": v(63, 83.5) * mm});
            skLineSegment(sketch, "E202.0.1", {"start": v(63, 83.5) * mm, "end": v(63, 86.5) * mm});
            skLineSegment(sketch, "E202.0.2", {"start": v(63, 86.5) * mm, "end": v(57, 86.5) * mm});
            skLineSegment(sketch, "E202.0.3", {"start": v(57, 86.5) * mm, "end": v(57, 83.5) * mm});
            skSolve(sketch);
        }
        {
            var Q0;
            Q0=makeQuery(id+"F3.imprint","IMPRINT",FACE,{"disambiguationData":[TD([[makeQuery(id+"F3.imprint","IMPRINT",EDGE,{"derivedFrom":sQuery(id+"F3.wireOp",EDGE,"E195.0.0")}),1.0]])]});
            var Q1;
            Q1=makeQuery(id+"F3.imprint","IMPRINT",FACE,{"disambiguationData":[TD([[makeQuery(id+"F3.imprint","IMPRINT",EDGE,{"derivedFrom":sQuery(id+"F3.wireOp",EDGE,"E194.0.0")}),1.0]])]});
            var Q2;
            Q2=makeQuery(id+"F3.imprint","IMPRINT",FACE,{"disambiguationData":[TD([[makeQuery(id+"F3.imprint","IMPRINT",EDGE,{"derivedFrom":sQuery(id+"F3.wireOp",EDGE,"E193.0.0")}),1.0]])]});
            var Q3;
            Q3=makeQuery(id+"F3.imprint","IMPRINT",FACE,{"disambiguationData":[TD([[makeQuery(id+"F3.imprint","IMPRINT",EDGE,{"derivedFrom":sQuery(id+"F3.wireOp",EDGE,"E192.0.0")}),1.0]])]});
            var Q4;
            Q4=makeQuery(id+"F3.imprint","IMPRINT",FACE,{"disambiguationData":[TD([[makeQuery(id+"F3.imprint","IMPRINT",EDGE,{"derivedFrom":sQuery(id+"F3.wireOp",EDGE,"E191.0.0")}),1.0]])]});
            var Q5;
            Q5=makeQuery(id+"F3.imprint","IMPRINT",FACE,{"disambiguationData":[TD([[makeQuery(id+"F3.imprint","IMPRINT",EDGE,{"derivedFrom":sQuery(id+"F3.wireOp",EDGE,"E190.0.0")}),1.0]])]});
            var Q6;
            Q6=makeQuery(id+"F3.imprint","IMPRINT",FACE,{"disambiguationData":[TD([[makeQuery(id+"F3.imprint","IMPRINT",EDGE,{"derivedFrom":sQuery(id+"F3.wireOp",EDGE,"E189.0.0")}),1.0]])]});
            var Q7;
            Q7=makeQuery(id+"F3.imprint","IMPRINT",FACE,{"disambiguationData":[TD([[makeQuery(id+"F3.imprint","IMPRINT",EDGE,{"derivedFrom":sQuery(id+"F3.wireOp",EDGE,"E188.0.0")}),1.0]])]});
            var Q8;
            Q8=makeQuery(id+"F3.imprint","IMPRINT",FACE,{"disambiguationData":[TD([[makeQuery(id+"F3.imprint","IMPRINT",EDGE,{"derivedFrom":sQuery(id+"F3.wireOp",EDGE,"E187.0.0")}),1.0]])]});
            var Q9;
            Q9=makeQuery(id+"F3.imprint","IMPRINT",FACE,{"disambiguationData":[TD([[makeQuery(id+"F3.imprint","IMPRINT",EDGE,{"derivedFrom":sQuery(id+"F3.wireOp",EDGE,"E179.0.0")}),1.0]])]});
            var Q10;
            Q10=makeQuery(id+"F3.imprint","IMPRINT",FACE,{"disambiguationData":[TD([[makeQuery(id+"F3.imprint","IMPRINT",EDGE,{"derivedFrom":sQuery(id+"F3.wireOp",EDGE,"E178.0.0")}),1.0]])]});
            var Q11;
            Q11=makeQuery(id+"F3.imprint","IMPRINT",FACE,{"disambiguationData":[TD([[makeQuery(id+"F3.imprint","IMPRINT",EDGE,{"derivedFrom":sQuery(id+"F3.wireOp",EDGE,"E177.0.0")}),1.0]])]});
            var Q12;
            Q12=makeQuery(id+"F3.imprint","IMPRINT",FACE,{"disambiguationData":[TD([[makeQuery(id+"F3.imprint","IMPRINT",EDGE,{"derivedFrom":sQuery(id+"F3.wireOp",EDGE,"E176.0.0")}),1.0]])]});
            var Q13;
            Q13=makeQuery(id+"F3.imprint","IMPRINT",FACE,{"disambiguationData":[TD([[makeQuery(id+"F3.imprint","IMPRINT",EDGE,{"derivedFrom":sQuery(id+"F3.wireOp",EDGE,"E175.0.0")}),1.0]])]});
            var Q14;
            Q14=makeQuery(id+"F3.imprint","IMPRINT",FACE,{"disambiguationData":[TD([[makeQuery(id+"F3.imprint","IMPRINT",EDGE,{"derivedFrom":sQuery(id+"F3.wireOp",EDGE,"E174.0.0")}),1.0]])]});
            var Q15;
            Q15=makeQuery(id+"F3.imprint","IMPRINT",FACE,{"disambiguationData":[TD([[makeQuery(id+"F3.imprint","IMPRINT",EDGE,{"derivedFrom":sQuery(id+"F3.wireOp",EDGE,"E173.0.0")}),1.0]])]});
            var Q16;
            Q16=makeQuery(id+"F3.imprint","IMPRINT",FACE,{"disambiguationData":[TD([[makeQuery(id+"F3.imprint","IMPRINT",EDGE,{"derivedFrom":sQuery(id+"F3.wireOp",EDGE,"E172.0.0")}),1.0]])]});
            var Q17;
            Q17=makeQuery(id+"F3.imprint","IMPRINT",FACE,{"disambiguationData":[TD([[makeQuery(id+"F3.imprint","IMPRINT",EDGE,{"derivedFrom":sQuery(id+"F3.wireOp",EDGE,"E171.0.0")}),1.0]])]});
            var Q18;
            Q18=makeQuery(id+"F1.opExtrude","CAP_FACE",FACE,{"disambiguationData":[OSD([sQuery(id+"F0.wireOp",EDGE,"E0.bottom"),sQuery(id+"F0.wireOp",EDGE,"E0.left"),sQuery(id+"F0.wireOp",EDGE,"E0.right"),sQuery(id+"F0.wireOp",EDGE,"E4.bottom"),sQuery(id+"F0.wireOp",EDGE,"E4.left"),sQuery(id+"F0.wireOp",EDGE,"E4.right"),sQuery(id+"F0.wireOp",EDGE,"E5.MirrorCS"),sQuery(id+"F0.wireOp",EDGE,"E6.MirrorCS"),sQuery(id+"F0.wireOp",EDGE,"E7.MirrorCS"),sQuery(id+"F0.wireOp",EDGE,"E8.0.1.0"),sQuery(id+"F0.wireOp",EDGE,"E8.0.1.1"),sQuery(id+"F0.wireOp",EDGE,"E8.0.1.2"),sQuery(id+"F0.wireOp",EDGE,"E8.0.1.3"),sQuery(id+"F0.wireOp",EDGE,"E8.0.1.4"),sQuery(id+"F0.wireOp",EDGE,"E8.0.1.5"),sQuery(id+"F0.wireOp",EDGE,"E8.0.2.0"),sQuery(id+"F0.wireOp",EDGE,"E8.0.2.1"),sQuery(id+"F0.wireOp",EDGE,"E8.0.2.2"),sQuery(id+"F0.wireOp",EDGE,"E8.0.2.3"),sQuery(id+"F0.wireOp",EDGE,"E8.0.2.4"),sQuery(id+"F0.wireOp",EDGE,"E8.0.2.5"),sQuery(id+"F0.wireOp",EDGE,"E8.0.3.0"),sQuery(id+"F0.wireOp",EDGE,"E8.0.3.1"),sQuery(id+"F0.wireOp",EDGE,"E8.0.3.2"),sQuery(id+"F0.wireOp",EDGE,"E8.0.3.3"),sQuery(id+"F0.wireOp",EDGE,"E8.0.3.4"),sQuery(id+"F0.wireOp",EDGE,"E8.0.3.5"),sQuery(id+"F0.wireOp",EDGE,"E8.0.4.0"),sQuery(id+"F0.wireOp",EDGE,"E8.0.4.1"),sQuery(id+"F0.wireOp",EDGE,"E8.0.4.2"),sQuery(id+"F0.wireOp",EDGE,"E8.0.4.3"),sQuery(id+"F0.wireOp",EDGE,"E8.0.4.4"),sQuery(id+"F0.wireOp",EDGE,"E8.0.4.5"),sQuery(id+"F0.wireOp",EDGE,"E9.MirrorCS"),sQuery(id+"F0.wireOp",EDGE,"E10.MirrorCS"),sQuery(id+"F0.wireOp",EDGE,"E11.MirrorCS"),sQuery(id+"F0.wireOp",EDGE,"E12.MirrorCS"),sQuery(id+"F0.wireOp",EDGE,"E13.MirrorCS"),sQuery(id+"F0.wireOp",EDGE,"E14.MirrorCS"),sQuery(id+"F0.wireOp",EDGE,"E15.MirrorCS"),sQuery(id+"F0.wireOp",EDGE,"E16.MirrorCS"),sQuery(id+"F0.wireOp",EDGE,"E17.MirrorCS"),sQuery(id+"F0.wireOp",EDGE,"E18.MirrorCS"),sQuery(id+"F0.wireOp",EDGE,"E19.MirrorCS"),sQuery(id+"F0.wireOp",EDGE,"E20.MirrorCS"),sQuery(id+"F0.wireOp",EDGE,"E21.MirrorCS"),sQuery(id+"F0.wireOp",EDGE,"E22.MirrorCS"),sQuery(id+"F0.wireOp",EDGE,"E23.MirrorCS"),sQuery(id+"F0.wireOp",EDGE,"E24.MirrorCS"),sQuery(id+"F0.wireOp",EDGE,"E25.MirrorCS"),sQuery(id+"F0.wireOp",EDGE,"E26.MirrorCS"),sQuery(id+"F0.wireOp",EDGE,"E27.MirrorCS"),sQuery(id+"F0.wireOp",EDGE,"E28.MirrorCS"),sQuery(id+"F0.wireOp",EDGE,"E29.MirrorCS"),sQuery(id+"F0.wireOp",EDGE,"E30.MirrorCS"),sQuery(id+"F0.wireOp",EDGE,"E31"),sQuery(id+"F0.wireOp",EDGE,"E32.bottom"),sQuery(id+"F0.wireOp",EDGE,"E32.top"),sQuery(id+"F0.wireOp",EDGE,"E32.right"),sQuery(id+"F0.wireOp",EDGE,"E33.MirrorCS"),sQuery(id+"F0.wireOp",EDGE,"E34.MirrorCS"),sQuery(id+"F0.wireOp",EDGE,"E35.MirrorCS"),sQuery(id+"F0.wireOp",EDGE,"E36.1.0.0"),sQuery(id+"F0.wireOp",EDGE,"E36.1.0.1"),sQuery(id+"F0.wireOp",EDGE,"E36.1.0.2"),sQuery(id+"F0.wireOp",EDGE,"E36.1.0.3"),sQuery(id+"F0.wireOp",EDGE,"E36.1.0.4"),sQuery(id+"F0.wireOp",EDGE,"E36.1.0.5"),sQuery(id+"F0.wireOp",EDGE,"E36.2.0.0"),sQuery(id+"F0.wireOp",EDGE,"E36.2.0.1"),sQuery(id+"F0.wireOp",EDGE,"E36.2.0.2"),sQuery(id+"F0.wireOp",EDGE,"E36.2.0.3"),sQuery(id+"F0.wireOp",EDGE,"E36.2.0.4"),sQuery(id+"F0.wireOp",EDGE,"E36.2.0.5"),sQuery(id+"F0.wireOp",EDGE,"E36.3.0.0"),sQuery(id+"F0.wireOp",EDGE,"E36.3.0.1"),sQuery(id+"F0.wireOp",EDGE,"E36.3.0.2"),sQuery(id+"F0.wireOp",EDGE,"E36.3.0.3"),sQuery(id+"F0.wireOp",EDGE,"E36.3.0.4"),sQuery(id+"F0.wireOp",EDGE,"E36.3.0.5"),sQuery(id+"F0.wireOp",EDGE,"E37.MirrorCS"),sQuery(id+"F0.wireOp",EDGE,"E38.MirrorCS"),sQuery(id+"F0.wireOp",EDGE,"E39.MirrorCS"),sQuery(id+"F0.wireOp",EDGE,"E40.MirrorCS"),sQuery(id+"F0.wireOp",EDGE,"E41.MirrorCS"),sQuery(id+"F0.wireOp",EDGE,"E42.MirrorCS"),sQuery(id+"F0.wireOp",EDGE,"E43.MirrorCS"),sQuery(id+"F0.wireOp",EDGE,"E44.MirrorCS"),sQuery(id+"F0.wireOp",EDGE,"E45.MirrorCS"),sQuery(id+"F0.wireOp",EDGE,"E46.MirrorCS"),sQuery(id+"F0.wireOp",EDGE,"E47.MirrorCS"),sQuery(id+"F0.wireOp",EDGE,"E48.MirrorCS"),sQuery(id+"F0.wireOp",EDGE,"E49.MirrorCS"),sQuery(id+"F0.wireOp",EDGE,"E50.MirrorCS"),sQuery(id+"F0.wireOp",EDGE,"E51.MirrorCS"),sQuery(id+"F0.wireOp",EDGE,"E52.MirrorCS"),sQuery(id+"F0.wireOp",EDGE,"E53.MirrorCS"),sQuery(id+"F0.wireOp",EDGE,"E54.MirrorCS"),sQuery(id+"F0.wireOp",EDGE,"E55.MirrorCS"),sQuery(id+"F0.wireOp",EDGE,"E56.MirrorCS"),sQuery(id+"F0.wireOp",EDGE,"E57.MirrorCS"),sQuery(id+"F0.wireOp",EDGE,"E58.MirrorCS"),sQuery(id+"F0.wireOp",EDGE,"E59.MirrorCS"),sQuery(id+"F0.wireOp",EDGE,"E60.MirrorCS"),sQuery(id+"F0.wireOp",EDGE,"E61.MirrorCS"),sQuery(id+"F0.wireOp",EDGE,"E62.MirrorCS"),sQuery(id+"F0.wireOp",EDGE,"E63.MirrorCS"),sQuery(id+"F0.wireOp",EDGE,"E64.MirrorCS"),sQuery(id+"F0.wireOp",EDGE,"E65.MirrorCS"),sQuery(id+"F0.wireOp",EDGE,"E66.MirrorCS"),sQuery(id+"F0.wireOp",EDGE,"E67.MirrorCS"),sQuery(id+"F0.wireOp",EDGE,"E68.MirrorCS"),sQuery(id+"F0.wireOp",EDGE,"E69.MirrorCS"),sQuery(id+"F0.wireOp",EDGE,"E70.MirrorCS"),sQuery(id+"F0.wireOp",EDGE,"E71.MirrorCS"),sQuery(id+"F0.wireOp",EDGE,"E72.MirrorCS"),sQuery(id+"F0.wireOp",EDGE,"E73.MirrorCS"),sQuery(id+"F0.wireOp",EDGE,"E74.MirrorCS"),sQuery(id+"F0.wireOp",EDGE,"E75.MirrorCS"),sQuery(id+"F0.wireOp",EDGE,"E77.MirrorCS"),sQuery(id+"F0.wireOp",EDGE,"E78.MirrorCS"),sQuery(id+"F0.wireOp",EDGE,"E80.MirrorCS"),sQuery(id+"F0.wireOp",EDGE,"E81.MirrorCS"),sQuery(id+"F0.wireOp",EDGE,"E82.MirrorCS"),sQuery(id+"F0.wireOp",EDGE,"E83.MirrorCS"),sQuery(id+"F0.wireOp",EDGE,"E84.MirrorCS"),sQuery(id+"F0.wireOp",EDGE,"E85.MirrorCS"),sQuery(id+"F0.wireOp",EDGE,"E86.MirrorCS"),sQuery(id+"F0.wireOp",EDGE,"E87.MirrorCS"),sQuery(id+"F0.wireOp",EDGE,"E88.MirrorCS"),sQuery(id+"F0.wireOp",EDGE,"E89.MirrorCS"),sQuery(id+"F0.wireOp",EDGE,"E90.MirrorCS"),sQuery(id+"F0.wireOp",EDGE,"E91.MirrorCS"),sQuery(id+"F0.wireOp",EDGE,"E92.MirrorCS"),sQuery(id+"F0.wireOp",EDGE,"E93.MirrorCS"),sQuery(id+"F0.wireOp",EDGE,"E94.MirrorCS"),sQuery(id+"F0.wireOp",EDGE,"E95.MirrorCS"),sQuery(id+"F0.wireOp",EDGE,"E96.MirrorCS"),sQuery(id+"F0.wireOp",EDGE,"E97.MirrorCS"),sQuery(id+"F0.wireOp",EDGE,"E98.MirrorCS"),sQuery(id+"F0.wireOp",EDGE,"E99.MirrorCS"),sQuery(id+"F0.wireOp",EDGE,"E100.MirrorCS"),sQuery(id+"F0.wireOp",EDGE,"E101.MirrorCS"),sQuery(id+"F0.wireOp",EDGE,"E102.MirrorCS"),sQuery(id+"F0.wireOp",EDGE,"E103.MirrorCS"),sQuery(id+"F0.wireOp",EDGE,"E104.MirrorCS"),sQuery(id+"F0.wireOp",EDGE,"E105.MirrorCS"),sQuery(id+"F0.wireOp",EDGE,"E106.MirrorCS"),sQuery(id+"F0.wireOp",EDGE,"E107.MirrorCS"),sQuery(id+"F0.wireOp",EDGE,"E108"),sQuery(id+"F0.wireOp",EDGE,"E109"),sQuery(id+"F0.wireOp",EDGE,"E110.MirrorCS"),sQuery(id+"F0.wireOp",EDGE,"E111.MirrorCS"),sQuery(id+"F0.wireOp",EDGE,"E112.MirrorCS"),sQuery(id+"F0.wireOp",EDGE,"E113.MirrorCS"),sQuery(id+"F0.wireOp",EDGE,"E114.MirrorCS"),sQuery(id+"F0.wireOp",EDGE,"E115.MirrorCS"),sQuery(id+"F0.wireOp",EDGE,"E116.MirrorCS"),sQuery(id+"F0.wireOp",EDGE,"E117.MirrorCS"),sQuery(id+"F0.wireOp",EDGE,"E118.MirrorCS"),sQuery(id+"F0.wireOp",EDGE,"E119.MirrorCS"),sQuery(id+"F0.wireOp",EDGE,"E120.MirrorCS"),sQuery(id+"F0.wireOp",EDGE,"E121.MirrorCS"),sQuery(id+"F0.wireOp",EDGE,"E122.MirrorCS"),sQuery(id+"F0.wireOp",EDGE,"E123.MirrorCS"),sQuery(id+"F0.wireOp",EDGE,"E124.MirrorCS"),sQuery(id+"F0.wireOp",EDGE,"E125.MirrorCS"),sQuery(id+"F0.wireOp",EDGE,"E126.MirrorCS"),sQuery(id+"F0.wireOp",EDGE,"E127.MirrorCS"),sQuery(id+"F0.wireOp",EDGE,"E129.MirrorCS"),sQuery(id+"F0.wireOp",EDGE,"E130.MirrorCS"),sQuery(id+"F0.wireOp",EDGE,"E131.MirrorCS"),sQuery(id+"F0.wireOp",EDGE,"E132.MirrorCS"),sQuery(id+"F0.wireOp",EDGE,"E133.MirrorCS"),sQuery(id+"F0.wireOp",EDGE,"E134.MirrorCS"),sQuery(id+"F0.wireOp",EDGE,"E135.MirrorCS"),sQuery(id+"F0.wireOp",EDGE,"E136.MirrorCS"),sQuery(id+"F0.wireOp",EDGE,"E137.MirrorCS"),sQuery(id+"F0.wireOp",EDGE,"E138.MirrorCS"),sQuery(id+"F0.wireOp",EDGE,"E139.MirrorCS"),sQuery(id+"F0.wireOp",EDGE,"E140.MirrorCS"),sQuery(id+"F0.wireOp",EDGE,"E141.MirrorCS"),sQuery(id+"F0.wireOp",EDGE,"E142.MirrorCS"),sQuery(id+"F0.wireOp",EDGE,"E143.MirrorCS"),sQuery(id+"F0.wireOp",EDGE,"E144.MirrorCS"),sQuery(id+"F0.wireOp",EDGE,"E145.MirrorCS"),sQuery(id+"F0.wireOp",EDGE,"E146.MirrorCS"),sQuery(id+"F0.wireOp",EDGE,"E147.MirrorCS"),sQuery(id+"F0.wireOp",EDGE,"E148.MirrorCS"),sQuery(id+"F0.wireOp",EDGE,"E149.MirrorCS"),sQuery(id+"F0.wireOp",EDGE,"E150.MirrorCS"),sQuery(id+"F0.wireOp",EDGE,"E151")])],"isStart":true});
            extrude(context, id + "F4", {"entities" : qUnion([Q0, Q1, Q2, Q3, Q4, Q5, Q6, Q7, Q8, Q9, Q10, Q11, Q12, Q13, Q14, Q15, Q16, Q17]), "endBound" : BoundingType.UP_TO_SURFACE, "oppositeDirection" : true, "endBoundEntityFace" : qUnion([Q18]), "depth" : 4 * mm});
        }
        {
            var Q0;
            {var subQ4=makeQuery(id+"F1.opExtrude","CAP_EDGE",EDGE,{"disambiguationData":[OSD([sQuery(id+"F0.wireOp",EDGE,"E0.left")])],"isStart":false});Q0=makeQuery(id+"F2.imprint","IMPRINT",FACE,{"disambiguationData":[TD([[makeQuery(id+"F2.imprint","IMPRINT",EDGE,{"derivedFrom":subQ4}),1.0]])]});}
            var Q1;
            Q1=makeQuery(id+"F3.imprint","IMPRINT",FACE,{"disambiguationData":[TD([[makeQuery(id+"F3.imprint","IMPRINT",EDGE,{"derivedFrom":sQuery(id+"F3.wireOp",EDGE,"E195.0.0")}),1.0]])]});
            var Q2;
            Q2=makeQuery(id+"F3.imprint","IMPRINT",FACE,{"disambiguationData":[TD([[makeQuery(id+"F3.imprint","IMPRINT",EDGE,{"derivedFrom":sQuery(id+"F3.wireOp",EDGE,"E194.0.0")}),1.0]])]});
            var Q3;
            Q3=makeQuery(id+"F3.imprint","IMPRINT",FACE,{"disambiguationData":[TD([[makeQuery(id+"F3.imprint","IMPRINT",EDGE,{"derivedFrom":sQuery(id+"F3.wireOp",EDGE,"E193.0.0")}),1.0]])]});
            var Q4;
            {var subQ1=makeQuery(id+"F1.opExtrude","CAP_EDGE",EDGE,{"disambiguationData":[OSD([sQuery(id+"F0.wireOp",EDGE,"E4.bottom")])],"isStart":false});Q4=makeQuery(id+"F2.imprint","IMPRINT",FACE,{"disambiguationData":[TD([[makeQuery(id+"F2.imprint","IMPRINT",EDGE,{"derivedFrom":subQ1}),-1.0]])]});}
            var Q5;
            Q5=makeQuery(id+"F3.imprint","IMPRINT",FACE,{"disambiguationData":[TD([[makeQuery(id+"F3.imprint","IMPRINT",EDGE,{"derivedFrom":sQuery(id+"F3.wireOp",EDGE,"E190.0.0")}),1.0]])]});
            var Q6;
            Q6=makeQuery(id+"F3.imprint","IMPRINT",FACE,{"disambiguationData":[TD([[makeQuery(id+"F3.imprint","IMPRINT",EDGE,{"derivedFrom":sQuery(id+"F3.wireOp",EDGE,"E189.0.0")}),1.0]])]});
            var Q7;
            {var subQ1=makeQuery(id+"F1.opExtrude","CAP_EDGE",EDGE,{"disambiguationData":[OSD([sQuery(id+"F0.wireOp",EDGE,"E21.MirrorCS")])],"isStart":false});Q7=makeQuery(id+"F2.imprint","IMPRINT",FACE,{"disambiguationData":[TD([[makeQuery(id+"F2.imprint","IMPRINT",EDGE,{"derivedFrom":subQ1}),1.0]])]});}
            var Q8;
            Q8=makeQuery(id+"F3.imprint","IMPRINT",FACE,{"disambiguationData":[TD([[makeQuery(id+"F3.imprint","IMPRINT",EDGE,{"derivedFrom":sQuery(id+"F3.wireOp",EDGE,"E187.0.0")}),1.0]])]});
            var Q9;
            {var subQ1=makeQuery(id+"F1.opExtrude","CAP_EDGE",EDGE,{"disambiguationData":[OSD([sQuery(id+"F0.wireOp",EDGE,"E8.0.1.0")])],"isStart":false});Q9=makeQuery(id+"F2.imprint","IMPRINT",FACE,{"disambiguationData":[TD([[makeQuery(id+"F2.imprint","IMPRINT",EDGE,{"derivedFrom":subQ1}),-1.0]])]});}
            extrude(context, id + "F5", {"entities" : qUnion([Q0, Q1, Q2, Q3, Q4, Q5, Q6, Q7, Q8, Q9]), "depth" : 50 * mm});
        }
        {
            var Q0;
            Q0=makeQuery(id+"F1.opExtrude","CAP_FACE",FACE,{"disambiguationData":[OSD([sQuery(id+"F0.wireOp",EDGE,"E0.bottom"),sQuery(id+"F0.wireOp",EDGE,"E0.left"),sQuery(id+"F0.wireOp",EDGE,"E0.right"),sQuery(id+"F0.wireOp",EDGE,"E4.bottom"),sQuery(id+"F0.wireOp",EDGE,"E4.left"),sQuery(id+"F0.wireOp",EDGE,"E4.right"),sQuery(id+"F0.wireOp",EDGE,"E5.MirrorCS"),sQuery(id+"F0.wireOp",EDGE,"E6.MirrorCS"),sQuery(id+"F0.wireOp",EDGE,"E7.MirrorCS"),sQuery(id+"F0.wireOp",EDGE,"E8.0.1.0"),sQuery(id+"F0.wireOp",EDGE,"E8.0.1.1"),sQuery(id+"F0.wireOp",EDGE,"E8.0.1.2"),sQuery(id+"F0.wireOp",EDGE,"E8.0.1.3"),sQuery(id+"F0.wireOp",EDGE,"E8.0.1.4"),sQuery(id+"F0.wireOp",EDGE,"E8.0.1.5"),sQuery(id+"F0.wireOp",EDGE,"E8.0.2.0"),sQuery(id+"F0.wireOp",EDGE,"E8.0.2.1"),sQuery(id+"F0.wireOp",EDGE,"E8.0.2.2"),sQuery(id+"F0.wireOp",EDGE,"E8.0.2.3"),sQuery(id+"F0.wireOp",EDGE,"E8.0.2.4"),sQuery(id+"F0.wireOp",EDGE,"E8.0.2.5"),sQuery(id+"F0.wireOp",EDGE,"E8.0.3.0"),sQuery(id+"F0.wireOp",EDGE,"E8.0.3.1"),sQuery(id+"F0.wireOp",EDGE,"E8.0.3.2"),sQuery(id+"F0.wireOp",EDGE,"E8.0.3.3"),sQuery(id+"F0.wireOp",EDGE,"E8.0.3.4"),sQuery(id+"F0.wireOp",EDGE,"E8.0.3.5"),sQuery(id+"F0.wireOp",EDGE,"E8.0.4.0"),sQuery(id+"F0.wireOp",EDGE,"E8.0.4.1"),sQuery(id+"F0.wireOp",EDGE,"E8.0.4.2"),sQuery(id+"F0.wireOp",EDGE,"E8.0.4.3"),sQuery(id+"F0.wireOp",EDGE,"E8.0.4.4"),sQuery(id+"F0.wireOp",EDGE,"E8.0.4.5"),sQuery(id+"F0.wireOp",EDGE,"E9.MirrorCS"),sQuery(id+"F0.wireOp",EDGE,"E10.MirrorCS"),sQuery(id+"F0.wireOp",EDGE,"E11.MirrorCS"),sQuery(id+"F0.wireOp",EDGE,"E12.MirrorCS"),sQuery(id+"F0.wireOp",EDGE,"E13.MirrorCS"),sQuery(id+"F0.wireOp",EDGE,"E14.MirrorCS"),sQuery(id+"F0.wireOp",EDGE,"E15.MirrorCS"),sQuery(id+"F0.wireOp",EDGE,"E16.MirrorCS"),sQuery(id+"F0.wireOp",EDGE,"E17.MirrorCS"),sQuery(id+"F0.wireOp",EDGE,"E18.MirrorCS"),sQuery(id+"F0.wireOp",EDGE,"E19.MirrorCS"),sQuery(id+"F0.wireOp",EDGE,"E20.MirrorCS"),sQuery(id+"F0.wireOp",EDGE,"E21.MirrorCS"),sQuery(id+"F0.wireOp",EDGE,"E22.MirrorCS"),sQuery(id+"F0.wireOp",EDGE,"E23.MirrorCS"),sQuery(id+"F0.wireOp",EDGE,"E24.MirrorCS"),sQuery(id+"F0.wireOp",EDGE,"E25.MirrorCS"),sQuery(id+"F0.wireOp",EDGE,"E26.MirrorCS"),sQuery(id+"F0.wireOp",EDGE,"E27.MirrorCS"),sQuery(id+"F0.wireOp",EDGE,"E28.MirrorCS"),sQuery(id+"F0.wireOp",EDGE,"E29.MirrorCS"),sQuery(id+"F0.wireOp",EDGE,"E30.MirrorCS"),sQuery(id+"F0.wireOp",EDGE,"E31"),sQuery(id+"F0.wireOp",EDGE,"E32.bottom"),sQuery(id+"F0.wireOp",EDGE,"E32.top"),sQuery(id+"F0.wireOp",EDGE,"E32.right"),sQuery(id+"F0.wireOp",EDGE,"E33.MirrorCS"),sQuery(id+"F0.wireOp",EDGE,"E34.MirrorCS"),sQuery(id+"F0.wireOp",EDGE,"E35.MirrorCS"),sQuery(id+"F0.wireOp",EDGE,"E36.1.0.0"),sQuery(id+"F0.wireOp",EDGE,"E36.1.0.1"),sQuery(id+"F0.wireOp",EDGE,"E36.1.0.2"),sQuery(id+"F0.wireOp",EDGE,"E36.1.0.3"),sQuery(id+"F0.wireOp",EDGE,"E36.1.0.4"),sQuery(id+"F0.wireOp",EDGE,"E36.1.0.5"),sQuery(id+"F0.wireOp",EDGE,"E36.2.0.0"),sQuery(id+"F0.wireOp",EDGE,"E36.2.0.1"),sQuery(id+"F0.wireOp",EDGE,"E36.2.0.2"),sQuery(id+"F0.wireOp",EDGE,"E36.2.0.3"),sQuery(id+"F0.wireOp",EDGE,"E36.2.0.4"),sQuery(id+"F0.wireOp",EDGE,"E36.2.0.5"),sQuery(id+"F0.wireOp",EDGE,"E36.3.0.0"),sQuery(id+"F0.wireOp",EDGE,"E36.3.0.1"),sQuery(id+"F0.wireOp",EDGE,"E36.3.0.2"),sQuery(id+"F0.wireOp",EDGE,"E36.3.0.3"),sQuery(id+"F0.wireOp",EDGE,"E36.3.0.4"),sQuery(id+"F0.wireOp",EDGE,"E36.3.0.5"),sQuery(id+"F0.wireOp",EDGE,"E37.MirrorCS"),sQuery(id+"F0.wireOp",EDGE,"E38.MirrorCS"),sQuery(id+"F0.wireOp",EDGE,"E39.MirrorCS"),sQuery(id+"F0.wireOp",EDGE,"E40.MirrorCS"),sQuery(id+"F0.wireOp",EDGE,"E41.MirrorCS"),sQuery(id+"F0.wireOp",EDGE,"E42.MirrorCS"),sQuery(id+"F0.wireOp",EDGE,"E43.MirrorCS"),sQuery(id+"F0.wireOp",EDGE,"E44.MirrorCS"),sQuery(id+"F0.wireOp",EDGE,"E45.MirrorCS"),sQuery(id+"F0.wireOp",EDGE,"E46.MirrorCS"),sQuery(id+"F0.wireOp",EDGE,"E47.MirrorCS"),sQuery(id+"F0.wireOp",EDGE,"E48.MirrorCS"),sQuery(id+"F0.wireOp",EDGE,"E49.MirrorCS"),sQuery(id+"F0.wireOp",EDGE,"E50.MirrorCS"),sQuery(id+"F0.wireOp",EDGE,"E51.MirrorCS"),sQuery(id+"F0.wireOp",EDGE,"E52.MirrorCS"),sQuery(id+"F0.wireOp",EDGE,"E53.MirrorCS"),sQuery(id+"F0.wireOp",EDGE,"E54.MirrorCS"),sQuery(id+"F0.wireOp",EDGE,"E55.MirrorCS"),sQuery(id+"F0.wireOp",EDGE,"E56.MirrorCS"),sQuery(id+"F0.wireOp",EDGE,"E57.MirrorCS"),sQuery(id+"F0.wireOp",EDGE,"E58.MirrorCS"),sQuery(id+"F0.wireOp",EDGE,"E59.MirrorCS"),sQuery(id+"F0.wireOp",EDGE,"E60.MirrorCS"),sQuery(id+"F0.wireOp",EDGE,"E61.MirrorCS"),sQuery(id+"F0.wireOp",EDGE,"E62.MirrorCS"),sQuery(id+"F0.wireOp",EDGE,"E63.MirrorCS"),sQuery(id+"F0.wireOp",EDGE,"E64.MirrorCS"),sQuery(id+"F0.wireOp",EDGE,"E65.MirrorCS"),sQuery(id+"F0.wireOp",EDGE,"E66.MirrorCS"),sQuery(id+"F0.wireOp",EDGE,"E67.MirrorCS"),sQuery(id+"F0.wireOp",EDGE,"E68.MirrorCS"),sQuery(id+"F0.wireOp",EDGE,"E69.MirrorCS"),sQuery(id+"F0.wireOp",EDGE,"E70.MirrorCS"),sQuery(id+"F0.wireOp",EDGE,"E71.MirrorCS"),sQuery(id+"F0.wireOp",EDGE,"E72.MirrorCS"),sQuery(id+"F0.wireOp",EDGE,"E73.MirrorCS"),sQuery(id+"F0.wireOp",EDGE,"E74.MirrorCS"),sQuery(id+"F0.wireOp",EDGE,"E75.MirrorCS"),sQuery(id+"F0.wireOp",EDGE,"E77.MirrorCS"),sQuery(id+"F0.wireOp",EDGE,"E78.MirrorCS"),sQuery(id+"F0.wireOp",EDGE,"E80.MirrorCS"),sQuery(id+"F0.wireOp",EDGE,"E81.MirrorCS"),sQuery(id+"F0.wireOp",EDGE,"E82.MirrorCS"),sQuery(id+"F0.wireOp",EDGE,"E83.MirrorCS"),sQuery(id+"F0.wireOp",EDGE,"E84.MirrorCS"),sQuery(id+"F0.wireOp",EDGE,"E85.MirrorCS"),sQuery(id+"F0.wireOp",EDGE,"E86.MirrorCS"),sQuery(id+"F0.wireOp",EDGE,"E87.MirrorCS"),sQuery(id+"F0.wireOp",EDGE,"E88.MirrorCS"),sQuery(id+"F0.wireOp",EDGE,"E89.MirrorCS"),sQuery(id+"F0.wireOp",EDGE,"E90.MirrorCS"),sQuery(id+"F0.wireOp",EDGE,"E91.MirrorCS"),sQuery(id+"F0.wireOp",EDGE,"E92.MirrorCS"),sQuery(id+"F0.wireOp",EDGE,"E93.MirrorCS"),sQuery(id+"F0.wireOp",EDGE,"E94.MirrorCS"),sQuery(id+"F0.wireOp",EDGE,"E95.MirrorCS"),sQuery(id+"F0.wireOp",EDGE,"E96.MirrorCS"),sQuery(id+"F0.wireOp",EDGE,"E97.MirrorCS"),sQuery(id+"F0.wireOp",EDGE,"E98.MirrorCS"),sQuery(id+"F0.wireOp",EDGE,"E99.MirrorCS"),sQuery(id+"F0.wireOp",EDGE,"E100.MirrorCS"),sQuery(id+"F0.wireOp",EDGE,"E101.MirrorCS"),sQuery(id+"F0.wireOp",EDGE,"E102.MirrorCS"),sQuery(id+"F0.wireOp",EDGE,"E103.MirrorCS"),sQuery(id+"F0.wireOp",EDGE,"E104.MirrorCS"),sQuery(id+"F0.wireOp",EDGE,"E105.MirrorCS"),sQuery(id+"F0.wireOp",EDGE,"E106.MirrorCS"),sQuery(id+"F0.wireOp",EDGE,"E107.MirrorCS"),sQuery(id+"F0.wireOp",EDGE,"E108"),sQuery(id+"F0.wireOp",EDGE,"E109"),sQuery(id+"F0.wireOp",EDGE,"E110.MirrorCS"),sQuery(id+"F0.wireOp",EDGE,"E111.MirrorCS"),sQuery(id+"F0.wireOp",EDGE,"E112.MirrorCS"),sQuery(id+"F0.wireOp",EDGE,"E113.MirrorCS"),sQuery(id+"F0.wireOp",EDGE,"E114.MirrorCS"),sQuery(id+"F0.wireOp",EDGE,"E115.MirrorCS"),sQuery(id+"F0.wireOp",EDGE,"E116.MirrorCS"),sQuery(id+"F0.wireOp",EDGE,"E117.MirrorCS"),sQuery(id+"F0.wireOp",EDGE,"E118.MirrorCS"),sQuery(id+"F0.wireOp",EDGE,"E119.MirrorCS"),sQuery(id+"F0.wireOp",EDGE,"E120.MirrorCS"),sQuery(id+"F0.wireOp",EDGE,"E121.MirrorCS"),sQuery(id+"F0.wireOp",EDGE,"E122.MirrorCS"),sQuery(id+"F0.wireOp",EDGE,"E123.MirrorCS"),sQuery(id+"F0.wireOp",EDGE,"E124.MirrorCS"),sQuery(id+"F0.wireOp",EDGE,"E125.MirrorCS"),sQuery(id+"F0.wireOp",EDGE,"E126.MirrorCS"),sQuery(id+"F0.wireOp",EDGE,"E127.MirrorCS"),sQuery(id+"F0.wireOp",EDGE,"E129.MirrorCS"),sQuery(id+"F0.wireOp",EDGE,"E130.MirrorCS"),sQuery(id+"F0.wireOp",EDGE,"E131.MirrorCS"),sQuery(id+"F0.wireOp",EDGE,"E132.MirrorCS"),sQuery(id+"F0.wireOp",EDGE,"E133.MirrorCS"),sQuery(id+"F0.wireOp",EDGE,"E134.MirrorCS"),sQuery(id+"F0.wireOp",EDGE,"E135.MirrorCS"),sQuery(id+"F0.wireOp",EDGE,"E136.MirrorCS"),sQuery(id+"F0.wireOp",EDGE,"E137.MirrorCS"),sQuery(id+"F0.wireOp",EDGE,"E138.MirrorCS"),sQuery(id+"F0.wireOp",EDGE,"E139.MirrorCS"),sQuery(id+"F0.wireOp",EDGE,"E140.MirrorCS"),sQuery(id+"F0.wireOp",EDGE,"E141.MirrorCS"),sQuery(id+"F0.wireOp",EDGE,"E142.MirrorCS"),sQuery(id+"F0.wireOp",EDGE,"E143.MirrorCS"),sQuery(id+"F0.wireOp",EDGE,"E144.MirrorCS"),sQuery(id+"F0.wireOp",EDGE,"E145.MirrorCS"),sQuery(id+"F0.wireOp",EDGE,"E146.MirrorCS"),sQuery(id+"F0.wireOp",EDGE,"E147.MirrorCS"),sQuery(id+"F0.wireOp",EDGE,"E148.MirrorCS"),sQuery(id+"F0.wireOp",EDGE,"E149.MirrorCS"),sQuery(id+"F0.wireOp",EDGE,"E150.MirrorCS"),sQuery(id+"F0.wireOp",EDGE,"E151")])],"isStart":false});
            var sketch = newSketch(context, id + "F6", { "sketchPlane" : qUnion([Q0])});
            skLineSegment(sketch, "E203.bottom", {"start": v(63, -83.5) * mm, "end": v(57, -83.5) * mm});
            skLineSegment(sketch, "E203.top", {"start": v(63, -86.5) * mm, "end": v(57, -86.5) * mm});
            skLineSegment(sketch, "E203.left", {"start": v(63, -83.5) * mm, "end": v(63, -86.5) * mm});
            skLineSegment(sketch, "E203.right", {"start": v(57, -83.5) * mm, "end": v(57, -86.5) * mm});
            skLineSegment(sketch, "E204.bottom", {"start": v(43, -83.5) * mm, "end": v(37, -83.5) * mm});
            skLineSegment(sketch, "E204.top", {"start": v(43, -86.5) * mm, "end": v(37, -86.5) * mm});
            skLineSegment(sketch, "E204.left", {"start": v(43, -83.5) * mm, "end": v(43, -86.5) * mm});
            skLineSegment(sketch, "E204.right", {"start": v(37, -83.5) * mm, "end": v(37, -86.5) * mm});
            skLineSegment(sketch, "E205.bottom", {"start": v(23, -83.5) * mm, "end": v(17, -83.5) * mm});
            skLineSegment(sketch, "E205.top", {"start": v(23, -86.5) * mm, "end": v(17, -86.5) * mm});
            skLineSegment(sketch, "E205.left", {"start": v(23, -83.5) * mm, "end": v(23, -86.5) * mm});
            skLineSegment(sketch, "E205.right", {"start": v(17, -83.5) * mm, "end": v(17, -86.5) * mm});
            skLineSegment(sketch, "E206.bottom", {"start": v(3, -83.5) * mm, "end": v(-3, -83.5) * mm});
            skLineSegment(sketch, "E206.top", {"start": v(3, -86.5) * mm, "end": v(-3, -86.5) * mm});
            skLineSegment(sketch, "E206.left", {"start": v(3, -83.5) * mm, "end": v(3, -86.5) * mm});
            skLineSegment(sketch, "E206.right", {"start": v(-3, -83.5) * mm, "end": v(-3, -86.5) * mm});
            skLineSegment(sketch, "E207.bottom", {"start": v(-17, -83.5) * mm, "end": v(-23, -83.5) * mm});
            skLineSegment(sketch, "E207.top", {"start": v(-17, -86.5) * mm, "end": v(-23, -86.5) * mm});
            skLineSegment(sketch, "E207.left", {"start": v(-17, -83.5) * mm, "end": v(-17, -86.5) * mm});
            skLineSegment(sketch, "E207.right", {"start": v(-23, -83.5) * mm, "end": v(-23, -86.5) * mm});
            skLineSegment(sketch, "E208.bottom", {"start": v(-37, -83.5) * mm, "end": v(-43, -83.5) * mm});
            skLineSegment(sketch, "E208.top", {"start": v(-37, -86.5) * mm, "end": v(-43, -86.5) * mm});
            skLineSegment(sketch, "E208.left", {"start": v(-37, -83.5) * mm, "end": v(-37, -86.5) * mm});
            skLineSegment(sketch, "E208.right", {"start": v(-43, -83.5) * mm, "end": v(-43, -86.5) * mm});
            skLineSegment(sketch, "E209.bottom", {"start": v(57, 86.5) * mm, "end": v(63, 86.5) * mm});
            skLineSegment(sketch, "E209.top", {"start": v(57, 83.5) * mm, "end": v(63, 83.5) * mm});
            skLineSegment(sketch, "E209.left", {"start": v(57, 86.5) * mm, "end": v(57, 83.5) * mm});
            skLineSegment(sketch, "E209.right", {"start": v(63, 86.5) * mm, "end": v(63, 83.5) * mm});
            skLineSegment(sketch, "E210.bottom", {"start": v(37, 86.5) * mm, "end": v(43, 86.5) * mm});
            skLineSegment(sketch, "E210.top", {"start": v(37, 83.5) * mm, "end": v(43, 83.5) * mm});
            skLineSegment(sketch, "E210.left", {"start": v(37, 86.5) * mm, "end": v(37, 83.5) * mm});
            skLineSegment(sketch, "E210.right", {"start": v(43, 86.5) * mm, "end": v(43, 83.5) * mm});
            skLineSegment(sketch, "E211.bottom", {"start": v(17, 86.5) * mm, "end": v(23, 86.5) * mm});
            skLineSegment(sketch, "E211.top", {"start": v(17, 83.5) * mm, "end": v(23, 83.5) * mm});
            skLineSegment(sketch, "E211.left", {"start": v(17, 86.5) * mm, "end": v(17, 83.5) * mm});
            skLineSegment(sketch, "E211.right", {"start": v(23, 86.5) * mm, "end": v(23, 83.5) * mm});
            skLineSegment(sketch, "E212.bottom", {"start": v(-3, 86.5) * mm, "end": v(3, 86.5) * mm});
            skLineSegment(sketch, "E212.top", {"start": v(-3, 83.5) * mm, "end": v(3, 83.5) * mm});
            skLineSegment(sketch, "E212.left", {"start": v(-3, 86.5) * mm, "end": v(-3, 83.5) * mm});
            skLineSegment(sketch, "E212.right", {"start": v(3, 86.5) * mm, "end": v(3, 83.5) * mm});
            skLineSegment(sketch, "E213.bottom", {"start": v(-23, 86.5) * mm, "end": v(-17, 86.5) * mm});
            skLineSegment(sketch, "E213.top", {"start": v(-23, 83.5) * mm, "end": v(-17, 83.5) * mm});
            skLineSegment(sketch, "E213.left", {"start": v(-23, 86.5) * mm, "end": v(-23, 83.5) * mm});
            skLineSegment(sketch, "E213.right", {"start": v(-17, 86.5) * mm, "end": v(-17, 83.5) * mm});
            skLineSegment(sketch, "E214.bottom", {"start": v(-43, 86.5) * mm, "end": v(-37, 86.5) * mm});
            skLineSegment(sketch, "E214.top", {"start": v(-43, 83.5) * mm, "end": v(-37, 83.5) * mm});
            skLineSegment(sketch, "E214.left", {"start": v(-43, 86.5) * mm, "end": v(-43, 83.5) * mm});
            skLineSegment(sketch, "E214.right", {"start": v(-37, 86.5) * mm, "end": v(-37, 83.5) * mm});
            skLineSegment(sketch, "E215.bottom", {"start": v(-63, 86.5) * mm, "end": v(-57, 86.5) * mm});
            skLineSegment(sketch, "E215.top", {"start": v(-63, 83.5) * mm, "end": v(-57, 83.5) * mm});
            skLineSegment(sketch, "E215.left", {"start": v(-63, 86.5) * mm, "end": v(-63, 83.5) * mm});
            skLineSegment(sketch, "E215.right", {"start": v(-57, 86.5) * mm, "end": v(-57, 83.5) * mm});
            skLineSegment(sketch, "E216.bottom", {"start": v(-63, -83.5) * mm, "end": v(-57, -83.5) * mm});
            skLineSegment(sketch, "E216.top", {"start": v(-63, -86.5) * mm, "end": v(-57, -86.5) * mm});
            skLineSegment(sketch, "E216.left", {"start": v(-63, -83.5) * mm, "end": v(-63, -86.5) * mm});
            skLineSegment(sketch, "E216.right", {"start": v(-57, -83.5) * mm, "end": v(-57, -86.5) * mm});
            skSolve(sketch);
        }
        {
            var Q0;
            Q0=makeQuery(id+"F6.imprint","IMPRINT",FACE,{"disambiguationData":[TD([[makeQuery(id+"F6.imprint","IMPRINT",EDGE,{"derivedFrom":sQuery(id+"F6.wireOp",EDGE,"E209.bottom")}),1.0]])]});
            var Q1;
            Q1=makeQuery(id+"F6.imprint","IMPRINT",FACE,{"disambiguationData":[TD([[makeQuery(id+"F6.imprint","IMPRINT",EDGE,{"derivedFrom":sQuery(id+"F6.wireOp",EDGE,"E210.bottom")}),1.0]])]});
            var Q2;
            Q2=makeQuery(id+"F6.imprint","IMPRINT",FACE,{"disambiguationData":[TD([[makeQuery(id+"F6.imprint","IMPRINT",EDGE,{"derivedFrom":sQuery(id+"F6.wireOp",EDGE,"E211.bottom")}),1.0]])]});
            var Q3;
            Q3=makeQuery(id+"F6.imprint","IMPRINT",FACE,{"disambiguationData":[TD([[makeQuery(id+"F6.imprint","IMPRINT",EDGE,{"derivedFrom":sQuery(id+"F6.wireOp",EDGE,"E212.bottom")}),1.0]])]});
            var Q4;
            Q4=makeQuery(id+"F6.imprint","IMPRINT",FACE,{"disambiguationData":[TD([[makeQuery(id+"F6.imprint","IMPRINT",EDGE,{"derivedFrom":sQuery(id+"F6.wireOp",EDGE,"E213.bottom")}),1.0]])]});
            var Q5;
            Q5=makeQuery(id+"F6.imprint","IMPRINT",FACE,{"disambiguationData":[TD([[makeQuery(id+"F6.imprint","IMPRINT",EDGE,{"derivedFrom":sQuery(id+"F6.wireOp",EDGE,"E214.bottom")}),1.0]])]});
            var Q6;
            Q6=makeQuery(id+"F6.imprint","IMPRINT",FACE,{"disambiguationData":[TD([[makeQuery(id+"F6.imprint","IMPRINT",EDGE,{"derivedFrom":sQuery(id+"F6.wireOp",EDGE,"E203.bottom")}),1.0]])]});
            var Q7;
            Q7=makeQuery(id+"F6.imprint","IMPRINT",FACE,{"disambiguationData":[TD([[makeQuery(id+"F6.imprint","IMPRINT",EDGE,{"derivedFrom":sQuery(id+"F6.wireOp",EDGE,"E204.bottom")}),1.0]])]});
            var Q8;
            Q8=makeQuery(id+"F6.imprint","IMPRINT",FACE,{"disambiguationData":[TD([[makeQuery(id+"F6.imprint","IMPRINT",EDGE,{"derivedFrom":sQuery(id+"F6.wireOp",EDGE,"E205.bottom")}),1.0]])]});
            var Q9;
            Q9=makeQuery(id+"F6.imprint","IMPRINT",FACE,{"disambiguationData":[TD([[makeQuery(id+"F6.imprint","IMPRINT",EDGE,{"derivedFrom":sQuery(id+"F6.wireOp",EDGE,"E206.bottom")}),1.0]])]});
            var Q10;
            Q10=makeQuery(id+"F6.imprint","IMPRINT",FACE,{"disambiguationData":[TD([[makeQuery(id+"F6.imprint","IMPRINT",EDGE,{"derivedFrom":sQuery(id+"F6.wireOp",EDGE,"E207.bottom")}),-1.0]])]});
            var Q11;
            Q11=makeQuery(id+"F6.imprint","IMPRINT",FACE,{"disambiguationData":[TD([[makeQuery(id+"F6.imprint","IMPRINT",EDGE,{"derivedFrom":sQuery(id+"F6.wireOp",EDGE,"E208.bottom")}),1.0]])]});
            var Q12;
            Q12=makeQuery(id+"F6.imprint","IMPRINT",FACE,{"disambiguationData":[TD([[makeQuery(id+"F6.imprint","IMPRINT",EDGE,{"derivedFrom":sQuery(id+"F6.wireOp",EDGE,"E216.bottom")}),-1.0]])]});
            var Q13;
            Q13=makeQuery(id+"F6.imprint","IMPRINT",FACE,{"disambiguationData":[TD([[makeQuery(id+"F6.imprint","IMPRINT",EDGE,{"derivedFrom":sQuery(id+"F6.wireOp",EDGE,"E215.bottom")}),1.0]])]});
            extrude(context, id + "F7", {"entities" : qUnion([Q0, Q1, Q2, Q3, Q4, Q5, Q6, Q7, Q8, Q9, Q10, Q11, Q12, Q13]), "oppositeDirection" : true, "depth" : 4 * mm});
        }
        {
            var Q0;
            Q0=makeQuery(id+"F1.opExtrude","CAP_FACE",FACE,{"disambiguationData":[OSD([sQuery(id+"F0.wireOp",EDGE,"E0.bottom"),sQuery(id+"F0.wireOp",EDGE,"E0.left"),sQuery(id+"F0.wireOp",EDGE,"E0.right"),sQuery(id+"F0.wireOp",EDGE,"E4.bottom"),sQuery(id+"F0.wireOp",EDGE,"E4.left"),sQuery(id+"F0.wireOp",EDGE,"E4.right"),sQuery(id+"F0.wireOp",EDGE,"E5.MirrorCS"),sQuery(id+"F0.wireOp",EDGE,"E6.MirrorCS"),sQuery(id+"F0.wireOp",EDGE,"E7.MirrorCS"),sQuery(id+"F0.wireOp",EDGE,"E8.0.1.0"),sQuery(id+"F0.wireOp",EDGE,"E8.0.1.1"),sQuery(id+"F0.wireOp",EDGE,"E8.0.1.2"),sQuery(id+"F0.wireOp",EDGE,"E8.0.1.3"),sQuery(id+"F0.wireOp",EDGE,"E8.0.1.4"),sQuery(id+"F0.wireOp",EDGE,"E8.0.1.5"),sQuery(id+"F0.wireOp",EDGE,"E8.0.2.0"),sQuery(id+"F0.wireOp",EDGE,"E8.0.2.1"),sQuery(id+"F0.wireOp",EDGE,"E8.0.2.2"),sQuery(id+"F0.wireOp",EDGE,"E8.0.2.3"),sQuery(id+"F0.wireOp",EDGE,"E8.0.2.4"),sQuery(id+"F0.wireOp",EDGE,"E8.0.2.5"),sQuery(id+"F0.wireOp",EDGE,"E8.0.3.0"),sQuery(id+"F0.wireOp",EDGE,"E8.0.3.1"),sQuery(id+"F0.wireOp",EDGE,"E8.0.3.2"),sQuery(id+"F0.wireOp",EDGE,"E8.0.3.3"),sQuery(id+"F0.wireOp",EDGE,"E8.0.3.4"),sQuery(id+"F0.wireOp",EDGE,"E8.0.3.5"),sQuery(id+"F0.wireOp",EDGE,"E8.0.4.0"),sQuery(id+"F0.wireOp",EDGE,"E8.0.4.1"),sQuery(id+"F0.wireOp",EDGE,"E8.0.4.2"),sQuery(id+"F0.wireOp",EDGE,"E8.0.4.3"),sQuery(id+"F0.wireOp",EDGE,"E8.0.4.4"),sQuery(id+"F0.wireOp",EDGE,"E8.0.4.5"),sQuery(id+"F0.wireOp",EDGE,"E9.MirrorCS"),sQuery(id+"F0.wireOp",EDGE,"E10.MirrorCS"),sQuery(id+"F0.wireOp",EDGE,"E11.MirrorCS"),sQuery(id+"F0.wireOp",EDGE,"E12.MirrorCS"),sQuery(id+"F0.wireOp",EDGE,"E13.MirrorCS"),sQuery(id+"F0.wireOp",EDGE,"E14.MirrorCS"),sQuery(id+"F0.wireOp",EDGE,"E15.MirrorCS"),sQuery(id+"F0.wireOp",EDGE,"E16.MirrorCS"),sQuery(id+"F0.wireOp",EDGE,"E17.MirrorCS"),sQuery(id+"F0.wireOp",EDGE,"E18.MirrorCS"),sQuery(id+"F0.wireOp",EDGE,"E19.MirrorCS"),sQuery(id+"F0.wireOp",EDGE,"E20.MirrorCS"),sQuery(id+"F0.wireOp",EDGE,"E21.MirrorCS"),sQuery(id+"F0.wireOp",EDGE,"E22.MirrorCS"),sQuery(id+"F0.wireOp",EDGE,"E23.MirrorCS"),sQuery(id+"F0.wireOp",EDGE,"E24.MirrorCS"),sQuery(id+"F0.wireOp",EDGE,"E25.MirrorCS"),sQuery(id+"F0.wireOp",EDGE,"E26.MirrorCS"),sQuery(id+"F0.wireOp",EDGE,"E27.MirrorCS"),sQuery(id+"F0.wireOp",EDGE,"E28.MirrorCS"),sQuery(id+"F0.wireOp",EDGE,"E29.MirrorCS"),sQuery(id+"F0.wireOp",EDGE,"E30.MirrorCS"),sQuery(id+"F0.wireOp",EDGE,"E31"),sQuery(id+"F0.wireOp",EDGE,"E32.bottom"),sQuery(id+"F0.wireOp",EDGE,"E32.top"),sQuery(id+"F0.wireOp",EDGE,"E32.right"),sQuery(id+"F0.wireOp",EDGE,"E33.MirrorCS"),sQuery(id+"F0.wireOp",EDGE,"E34.MirrorCS"),sQuery(id+"F0.wireOp",EDGE,"E35.MirrorCS"),sQuery(id+"F0.wireOp",EDGE,"E36.1.0.0"),sQuery(id+"F0.wireOp",EDGE,"E36.1.0.1"),sQuery(id+"F0.wireOp",EDGE,"E36.1.0.2"),sQuery(id+"F0.wireOp",EDGE,"E36.1.0.3"),sQuery(id+"F0.wireOp",EDGE,"E36.1.0.4"),sQuery(id+"F0.wireOp",EDGE,"E36.1.0.5"),sQuery(id+"F0.wireOp",EDGE,"E36.2.0.0"),sQuery(id+"F0.wireOp",EDGE,"E36.2.0.1"),sQuery(id+"F0.wireOp",EDGE,"E36.2.0.2"),sQuery(id+"F0.wireOp",EDGE,"E36.2.0.3"),sQuery(id+"F0.wireOp",EDGE,"E36.2.0.4"),sQuery(id+"F0.wireOp",EDGE,"E36.2.0.5"),sQuery(id+"F0.wireOp",EDGE,"E36.3.0.0"),sQuery(id+"F0.wireOp",EDGE,"E36.3.0.1"),sQuery(id+"F0.wireOp",EDGE,"E36.3.0.2"),sQuery(id+"F0.wireOp",EDGE,"E36.3.0.3"),sQuery(id+"F0.wireOp",EDGE,"E36.3.0.4"),sQuery(id+"F0.wireOp",EDGE,"E36.3.0.5"),sQuery(id+"F0.wireOp",EDGE,"E37.MirrorCS"),sQuery(id+"F0.wireOp",EDGE,"E38.MirrorCS"),sQuery(id+"F0.wireOp",EDGE,"E39.MirrorCS"),sQuery(id+"F0.wireOp",EDGE,"E40.MirrorCS"),sQuery(id+"F0.wireOp",EDGE,"E41.MirrorCS"),sQuery(id+"F0.wireOp",EDGE,"E42.MirrorCS"),sQuery(id+"F0.wireOp",EDGE,"E43.MirrorCS"),sQuery(id+"F0.wireOp",EDGE,"E44.MirrorCS"),sQuery(id+"F0.wireOp",EDGE,"E45.MirrorCS"),sQuery(id+"F0.wireOp",EDGE,"E46.MirrorCS"),sQuery(id+"F0.wireOp",EDGE,"E47.MirrorCS"),sQuery(id+"F0.wireOp",EDGE,"E48.MirrorCS"),sQuery(id+"F0.wireOp",EDGE,"E49.MirrorCS"),sQuery(id+"F0.wireOp",EDGE,"E50.MirrorCS"),sQuery(id+"F0.wireOp",EDGE,"E51.MirrorCS"),sQuery(id+"F0.wireOp",EDGE,"E52.MirrorCS"),sQuery(id+"F0.wireOp",EDGE,"E53.MirrorCS"),sQuery(id+"F0.wireOp",EDGE,"E54.MirrorCS"),sQuery(id+"F0.wireOp",EDGE,"E55.MirrorCS"),sQuery(id+"F0.wireOp",EDGE,"E56.MirrorCS"),sQuery(id+"F0.wireOp",EDGE,"E57.MirrorCS"),sQuery(id+"F0.wireOp",EDGE,"E58.MirrorCS"),sQuery(id+"F0.wireOp",EDGE,"E59.MirrorCS"),sQuery(id+"F0.wireOp",EDGE,"E60.MirrorCS"),sQuery(id+"F0.wireOp",EDGE,"E61.MirrorCS"),sQuery(id+"F0.wireOp",EDGE,"E62.MirrorCS"),sQuery(id+"F0.wireOp",EDGE,"E63.MirrorCS"),sQuery(id+"F0.wireOp",EDGE,"E64.MirrorCS"),sQuery(id+"F0.wireOp",EDGE,"E65.MirrorCS"),sQuery(id+"F0.wireOp",EDGE,"E66.MirrorCS"),sQuery(id+"F0.wireOp",EDGE,"E67.MirrorCS"),sQuery(id+"F0.wireOp",EDGE,"E68.MirrorCS"),sQuery(id+"F0.wireOp",EDGE,"E69.MirrorCS"),sQuery(id+"F0.wireOp",EDGE,"E70.MirrorCS"),sQuery(id+"F0.wireOp",EDGE,"E71.MirrorCS"),sQuery(id+"F0.wireOp",EDGE,"E72.MirrorCS"),sQuery(id+"F0.wireOp",EDGE,"E73.MirrorCS"),sQuery(id+"F0.wireOp",EDGE,"E74.MirrorCS"),sQuery(id+"F0.wireOp",EDGE,"E75.MirrorCS"),sQuery(id+"F0.wireOp",EDGE,"E77.MirrorCS"),sQuery(id+"F0.wireOp",EDGE,"E78.MirrorCS"),sQuery(id+"F0.wireOp",EDGE,"E80.MirrorCS"),sQuery(id+"F0.wireOp",EDGE,"E81.MirrorCS"),sQuery(id+"F0.wireOp",EDGE,"E82.MirrorCS"),sQuery(id+"F0.wireOp",EDGE,"E83.MirrorCS"),sQuery(id+"F0.wireOp",EDGE,"E84.MirrorCS"),sQuery(id+"F0.wireOp",EDGE,"E85.MirrorCS"),sQuery(id+"F0.wireOp",EDGE,"E86.MirrorCS"),sQuery(id+"F0.wireOp",EDGE,"E87.MirrorCS"),sQuery(id+"F0.wireOp",EDGE,"E88.MirrorCS"),sQuery(id+"F0.wireOp",EDGE,"E89.MirrorCS"),sQuery(id+"F0.wireOp",EDGE,"E90.MirrorCS"),sQuery(id+"F0.wireOp",EDGE,"E91.MirrorCS"),sQuery(id+"F0.wireOp",EDGE,"E92.MirrorCS"),sQuery(id+"F0.wireOp",EDGE,"E93.MirrorCS"),sQuery(id+"F0.wireOp",EDGE,"E94.MirrorCS"),sQuery(id+"F0.wireOp",EDGE,"E95.MirrorCS"),sQuery(id+"F0.wireOp",EDGE,"E96.MirrorCS"),sQuery(id+"F0.wireOp",EDGE,"E97.MirrorCS"),sQuery(id+"F0.wireOp",EDGE,"E98.MirrorCS"),sQuery(id+"F0.wireOp",EDGE,"E99.MirrorCS"),sQuery(id+"F0.wireOp",EDGE,"E100.MirrorCS"),sQuery(id+"F0.wireOp",EDGE,"E101.MirrorCS"),sQuery(id+"F0.wireOp",EDGE,"E102.MirrorCS"),sQuery(id+"F0.wireOp",EDGE,"E103.MirrorCS"),sQuery(id+"F0.wireOp",EDGE,"E104.MirrorCS"),sQuery(id+"F0.wireOp",EDGE,"E105.MirrorCS"),sQuery(id+"F0.wireOp",EDGE,"E106.MirrorCS"),sQuery(id+"F0.wireOp",EDGE,"E107.MirrorCS"),sQuery(id+"F0.wireOp",EDGE,"E108"),sQuery(id+"F0.wireOp",EDGE,"E109"),sQuery(id+"F0.wireOp",EDGE,"E110.MirrorCS"),sQuery(id+"F0.wireOp",EDGE,"E111.MirrorCS"),sQuery(id+"F0.wireOp",EDGE,"E112.MirrorCS"),sQuery(id+"F0.wireOp",EDGE,"E113.MirrorCS"),sQuery(id+"F0.wireOp",EDGE,"E114.MirrorCS"),sQuery(id+"F0.wireOp",EDGE,"E115.MirrorCS"),sQuery(id+"F0.wireOp",EDGE,"E116.MirrorCS"),sQuery(id+"F0.wireOp",EDGE,"E117.MirrorCS"),sQuery(id+"F0.wireOp",EDGE,"E118.MirrorCS"),sQuery(id+"F0.wireOp",EDGE,"E119.MirrorCS"),sQuery(id+"F0.wireOp",EDGE,"E120.MirrorCS"),sQuery(id+"F0.wireOp",EDGE,"E121.MirrorCS"),sQuery(id+"F0.wireOp",EDGE,"E122.MirrorCS"),sQuery(id+"F0.wireOp",EDGE,"E123.MirrorCS"),sQuery(id+"F0.wireOp",EDGE,"E124.MirrorCS"),sQuery(id+"F0.wireOp",EDGE,"E125.MirrorCS"),sQuery(id+"F0.wireOp",EDGE,"E126.MirrorCS"),sQuery(id+"F0.wireOp",EDGE,"E127.MirrorCS"),sQuery(id+"F0.wireOp",EDGE,"E129.MirrorCS"),sQuery(id+"F0.wireOp",EDGE,"E130.MirrorCS"),sQuery(id+"F0.wireOp",EDGE,"E131.MirrorCS"),sQuery(id+"F0.wireOp",EDGE,"E132.MirrorCS"),sQuery(id+"F0.wireOp",EDGE,"E133.MirrorCS"),sQuery(id+"F0.wireOp",EDGE,"E134.MirrorCS"),sQuery(id+"F0.wireOp",EDGE,"E135.MirrorCS"),sQuery(id+"F0.wireOp",EDGE,"E136.MirrorCS"),sQuery(id+"F0.wireOp",EDGE,"E137.MirrorCS"),sQuery(id+"F0.wireOp",EDGE,"E138.MirrorCS"),sQuery(id+"F0.wireOp",EDGE,"E139.MirrorCS"),sQuery(id+"F0.wireOp",EDGE,"E140.MirrorCS"),sQuery(id+"F0.wireOp",EDGE,"E141.MirrorCS"),sQuery(id+"F0.wireOp",EDGE,"E142.MirrorCS"),sQuery(id+"F0.wireOp",EDGE,"E143.MirrorCS"),sQuery(id+"F0.wireOp",EDGE,"E144.MirrorCS"),sQuery(id+"F0.wireOp",EDGE,"E145.MirrorCS"),sQuery(id+"F0.wireOp",EDGE,"E146.MirrorCS"),sQuery(id+"F0.wireOp",EDGE,"E147.MirrorCS"),sQuery(id+"F0.wireOp",EDGE,"E148.MirrorCS"),sQuery(id+"F0.wireOp",EDGE,"E149.MirrorCS"),sQuery(id+"F0.wireOp",EDGE,"E150.MirrorCS"),sQuery(id+"F0.wireOp",EDGE,"E151")])],"isStart":false});
            var sketch = newSketch(context, id + "F8", { "sketchPlane" : qUnion([Q0])});
            skPoint(sketch, "E217.0", {"position": v(-63, 83.5) * mm});
            skPoint(sketch, "E218.0", {"position": v(63, 83.5) * mm});
            skLineSegment(sketch, "E219", {"start": v(-63, 83.5) * mm, "end": v(63, 83.5) * mm});
            skLineSegment(sketch, "E220", {"start": v(-63, 83.5) * mm, "end": v(-71, 83.5) * mm});
            skLineSegment(sketch, "E221", {"start": v(63, 83.5) * mm, "end": v(71, 83.5) * mm});
            skLineSegment(sketch, "E222.MirrorCS", {"start": v(-63, -83.5) * mm, "end": v(63, -83.5) * mm});
            skLineSegment(sketch, "E223.MirrorCS", {"start": v(63, -83.5) * mm, "end": v(71, -83.5) * mm});
            skLineSegment(sketch, "E224.MirrorCS", {"start": v(-63, -83.5) * mm, "end": v(-71, -83.5) * mm});
            skLineSegment(sketch, "E225", {"start": v(71, -83.5) * mm, "end": v(71, -87.5) * mm});
            skLineSegment(sketch, "E226", {"start": v(-71, -83.5) * mm, "end": v(-71, -87.5) * mm});
            skLineSegment(sketch, "E227", {"start": v(-71, 83.5) * mm, "end": v(-71, 87.5) * mm});
            skLineSegment(sketch, "E228", {"start": v(71, 83.5) * mm, "end": v(71, 87.5) * mm});
            skSolve(sketch);
        }
        {
            var Q0;
            Q0=makeQuery(id+"F5.opExtrude","SWEPT_FACE",FACE,{"disambiguationData":[OSD([sQuery(id+"F2.wireOp",EDGE,"E156")])]});
            var sketch = newSketch(context, id + "F9", { "sketchPlane" : qUnion([Q0])});
            skLineSegment(sketch, "E229", {"start": v(-86.5, 4) * mm, "end": v(-86.5, 54) * mm});
            skLineSegment(sketch, "E230", {"start": v(-86.5, 29) * mm, "end": v(87.5, 29) * mm, "construction": true});
            skLineSegment(sketch, "E231.bottom", {"start": v(-86.5, 32) * mm, "end": v(-83.5, 32) * mm});
            skLineSegment(sketch, "E231.top", {"start": v(-86.5, 29) * mm, "end": v(-83.5, 29) * mm});
            skLineSegment(sketch, "E231.left", {"start": v(-86.5, 32) * mm, "end": v(-86.5, 29) * mm});
            skLineSegment(sketch, "E231.right", {"start": v(-83.5, 32) * mm, "end": v(-83.5, 29) * mm});
            skLineSegment(sketch, "E232.MirrorCS", {"start": v(-86.5, 26) * mm, "end": v(-83.5, 26) * mm});
            skLineSegment(sketch, "E233.MirrorCS", {"start": v(-83.5, 26) * mm, "end": v(-83.5, 29) * mm});
            skLineSegment(sketch, "E234.0.1.0", {"start": v(-86.5, 47) * mm, "end": v(-83.5, 47) * mm});
            skLineSegment(sketch, "E234.0.1.1", {"start": v(-83.5, 47) * mm, "end": v(-83.5, 44) * mm});
            skLineSegment(sketch, "E234.0.1.2", {"start": v(-83.5, 41) * mm, "end": v(-83.5, 44) * mm});
            skLineSegment(sketch, "E234.0.1.3", {"start": v(-86.5, 41) * mm, "end": v(-83.5, 41) * mm});
            skLineSegment(sketch, "E234.direction1", {"start": v(-86.5, 32) * mm, "end": v(-61.5, 32) * mm, "construction": true});
            skLineSegment(sketch, "E234.direction2", {"start": v(-86.5, 32) * mm, "end": v(-86.5, 47) * mm, "construction": true});
            skLineSegment(sketch, "E235.MirrorCS", {"start": v(-86.5, 17) * mm, "end": v(-83.5, 17) * mm});
            skLineSegment(sketch, "E236.MirrorCS", {"start": v(-83.5, 17) * mm, "end": v(-83.5, 14) * mm});
            skLineSegment(sketch, "E237.MirrorCS", {"start": v(-83.5, 11) * mm, "end": v(-83.5, 14) * mm});
            skLineSegment(sketch, "E238.MirrorCS", {"start": v(-86.5, 11) * mm, "end": v(-83.5, 11) * mm});
            skLineSegment(sketch, "E239.MirrorCS", {"start": v(86.5, 47) * mm, "end": v(83.5, 47) * mm});
            skLineSegment(sketch, "E240.MirrorCS", {"start": v(83.5, 47) * mm, "end": v(83.5, 44) * mm});
            skLineSegment(sketch, "E241.MirrorCS", {"start": v(83.5, 41) * mm, "end": v(83.5, 44) * mm});
            skLineSegment(sketch, "E242.MirrorCS", {"start": v(86.5, 41) * mm, "end": v(83.5, 41) * mm});
            skLineSegment(sketch, "E243.MirrorCS", {"start": v(86.5, 4) * mm, "end": v(86.5, 54) * mm});
            skLineSegment(sketch, "E244.MirrorCS", {"start": v(83.5, 32) * mm, "end": v(83.5, 29) * mm});
            skLineSegment(sketch, "E245.MirrorCS", {"start": v(83.5, 26) * mm, "end": v(83.5, 29) * mm});
            skLineSegment(sketch, "E246.MirrorCS", {"start": v(86.5, 26) * mm, "end": v(83.5, 26) * mm});
            skLineSegment(sketch, "E247.MirrorCS", {"start": v(86.5, 17) * mm, "end": v(83.5, 17) * mm});
            skLineSegment(sketch, "E248.MirrorCS", {"start": v(83.5, 17) * mm, "end": v(83.5, 14) * mm});
            skLineSegment(sketch, "E249.MirrorCS", {"start": v(83.5, 11) * mm, "end": v(83.5, 14) * mm});
            skLineSegment(sketch, "E250.MirrorCS", {"start": v(86.5, 11) * mm, "end": v(83.5, 11) * mm});
            skLineSegment(sketch, "E251", {"start": v(83.5, 32) * mm, "end": v(86.5, 32) * mm});
            skSolve(sketch);
        }
        {
            var Q0;
            {var subQ0=sQuery(id+"F9.wireOp",EDGE,"E234.0.1.0");Q0=makeQuery(id+"F9.imprint","IMPRINT",FACE,{"disambiguationData":[TD([[makeQuery(id+"F9.imprint","IMPRINT",EDGE,{"derivedFrom":subQ0}),-1.0]])]});}
            var Q1;
            {var subQ0=sQuery(id+"F9.wireOp",EDGE,"E231.top");Q1=makeQuery(id+"F9.imprint","IMPRINT",FACE,{"disambiguationData":[TD([[makeQuery(id+"F9.imprint","IMPRINT",EDGE,{"derivedFrom":subQ0}),-1.0]])]});}
            var Q2;
            Q2=makeQuery(id+"F9.imprint","IMPRINT",FACE,{"disambiguationData":[TD([[makeQuery(id+"F9.imprint","IMPRINT",EDGE,{"derivedFrom":sQuery(id+"F9.wireOp",EDGE,"E231.bottom")}),-1.0]])]});
            var Q3;
            {var subQ0=sQuery(id+"F9.wireOp",EDGE,"E235.MirrorCS");Q3=makeQuery(id+"F9.imprint","IMPRINT",FACE,{"disambiguationData":[TD([[makeQuery(id+"F9.imprint","IMPRINT",EDGE,{"derivedFrom":subQ0}),-1.0]])]});}
            var Q4;
            {var subQ1=sQuery(id+"F9.wireOp",EDGE,"E239.MirrorCS");Q4=makeQuery(id+"F9.imprint","IMPRINT",FACE,{"disambiguationData":[TD([[makeQuery(id+"F9.imprint","IMPRINT",EDGE,{"derivedFrom":subQ1}),1.0]])]});}
            var Q5;
            Q5=makeQuery(id+"F9.imprint","IMPRINT",FACE,{"disambiguationData":[TD([[makeQuery(id+"F9.imprint","IMPRINT",EDGE,{"derivedFrom":sQuery(id+"F9.wireOp",EDGE,"E244.MirrorCS")}),1.0]])]});
            var Q6;
            {var subQ0=sQuery(id+"F9.wireOp",EDGE,"E247.MirrorCS");Q6=makeQuery(id+"F9.imprint","IMPRINT",FACE,{"disambiguationData":[TD([[makeQuery(id+"F9.imprint","IMPRINT",EDGE,{"derivedFrom":subQ0}),1.0]])]});}
            extrude(context, id + "F10", {"entities" : qUnion([Q0, Q1, Q2, Q3, Q4, Q5, Q6]), "operationType" : NewBodyOperationType.REMOVE, "oppositeDirection" : true, "depth" : 25 * mm});
        }
        {
            var Q0;
            Q0=makeQuery(id+"F8.imprint","IMPRINT",FACE,{"disambiguationData":[TD([[makeQuery(id+"F8.imprint","IMPRINT",EDGE,{"derivedFrom":sQuery(id+"F8.wireOp",EDGE,"E220")}),-1.0]])]});
            var Q1;
            Q1=makeQuery(id+"F8.imprint","IMPRINT",FACE,{"disambiguationData":[TD([[makeQuery(id+"F8.imprint","IMPRINT",EDGE,{"derivedFrom":sQuery(id+"F8.wireOp",EDGE,"E223.MirrorCS")}),-1.0]])]});
            var Q2;
            {var subQ2=makeQuery(id+"F1.opExtrude","CAP_EDGE",EDGE,{"disambiguationData":[OSD([sQuery(id+"F0.wireOp",EDGE,"E52.MirrorCS")])],"isStart":false});Q2=makeQuery(id+"F8.imprint","IMPRINT",FACE,{"disambiguationData":[TD([[makeQuery(id+"F8.imprint","IMPRINT",EDGE,{"derivedFrom":subQ2}),1.0]])]});}
            var Q3;
            {var subQ2=makeQuery(id+"F1.opExtrude","CAP_EDGE",EDGE,{"disambiguationData":[OSD([sQuery(id+"F0.wireOp",EDGE,"E45.MirrorCS")])],"isStart":false});Q3=makeQuery(id+"F8.imprint","IMPRINT",FACE,{"disambiguationData":[TD([[makeQuery(id+"F8.imprint","IMPRINT",EDGE,{"derivedFrom":subQ2}),-1.0]])]});}
            var Q4;
            {var subQ2=makeQuery(id+"F1.opExtrude","CAP_EDGE",EDGE,{"disambiguationData":[OSD([sQuery(id+"F0.wireOp",EDGE,"E39.MirrorCS")])],"isStart":false});Q4=makeQuery(id+"F8.imprint","IMPRINT",FACE,{"disambiguationData":[TD([[makeQuery(id+"F8.imprint","IMPRINT",EDGE,{"derivedFrom":subQ2}),1.0]])]});}
            var Q5;
            {var subQ1=makeQuery(id+"F1.opExtrude","CAP_EDGE",EDGE,{"disambiguationData":[OSD([sQuery(id+"F0.wireOp",EDGE,"E32.right")])],"isStart":false});Q5=makeQuery(id+"F8.imprint","IMPRINT",FACE,{"disambiguationData":[TD([[makeQuery(id+"F8.imprint","IMPRINT",EDGE,{"derivedFrom":subQ1}),-1.0]])]});}
            var Q6;
            {var subQ1=makeQuery(id+"F1.opExtrude","CAP_EDGE",EDGE,{"disambiguationData":[OSD([sQuery(id+"F0.wireOp",EDGE,"E36.1.0.3")])],"isStart":false});Q6=makeQuery(id+"F8.imprint","IMPRINT",FACE,{"disambiguationData":[TD([[makeQuery(id+"F8.imprint","IMPRINT",EDGE,{"derivedFrom":subQ1}),1.0]])]});}
            var Q7;
            {var subQ1=makeQuery(id+"F1.opExtrude","CAP_EDGE",EDGE,{"disambiguationData":[OSD([sQuery(id+"F0.wireOp",EDGE,"E36.2.0.3")])],"isStart":false});Q7=makeQuery(id+"F8.imprint","IMPRINT",FACE,{"disambiguationData":[TD([[makeQuery(id+"F8.imprint","IMPRINT",EDGE,{"derivedFrom":subQ1}),1.0]])]});}
            var Q8;
            {var subQ1=makeQuery(id+"F1.opExtrude","CAP_EDGE",EDGE,{"disambiguationData":[OSD([sQuery(id+"F0.wireOp",EDGE,"E36.3.0.3")])],"isStart":false});Q8=makeQuery(id+"F8.imprint","IMPRINT",FACE,{"disambiguationData":[TD([[makeQuery(id+"F8.imprint","IMPRINT",EDGE,{"derivedFrom":subQ1}),1.0]])]});}
            var Q9;
            {var subQ2=makeQuery(id+"F1.opExtrude","CAP_EDGE",EDGE,{"disambiguationData":[OSD([sQuery(id+"F0.wireOp",EDGE,"E147.MirrorCS")])],"isStart":false});Q9=makeQuery(id+"F8.imprint","IMPRINT",FACE,{"disambiguationData":[TD([[makeQuery(id+"F8.imprint","IMPRINT",EDGE,{"derivedFrom":subQ2}),1.0]])]});}
            var Q10;
            {var subQ1=makeQuery(id+"F1.opExtrude","CAP_EDGE",EDGE,{"disambiguationData":[OSD([sQuery(id+"F0.wireOp",EDGE,"E140.MirrorCS")])],"isStart":false});Q10=makeQuery(id+"F8.imprint","IMPRINT",FACE,{"disambiguationData":[TD([[makeQuery(id+"F8.imprint","IMPRINT",EDGE,{"derivedFrom":subQ1}),-1.0]])]});}
            var Q11;
            {var subQ2=makeQuery(id+"F1.opExtrude","CAP_EDGE",EDGE,{"disambiguationData":[OSD([sQuery(id+"F0.wireOp",EDGE,"E135.MirrorCS")])],"isStart":false});Q11=makeQuery(id+"F8.imprint","IMPRINT",FACE,{"disambiguationData":[TD([[makeQuery(id+"F8.imprint","IMPRINT",EDGE,{"derivedFrom":subQ2}),1.0]])]});}
            var Q12;
            {var subQ1=makeQuery(id+"F1.opExtrude","CAP_EDGE",EDGE,{"disambiguationData":[OSD([sQuery(id+"F0.wireOp",EDGE,"E131.MirrorCS")])],"isStart":false});Q12=makeQuery(id+"F8.imprint","IMPRINT",FACE,{"disambiguationData":[TD([[makeQuery(id+"F8.imprint","IMPRINT",EDGE,{"derivedFrom":subQ1}),-1.0]])]});}
            var Q13;
            {var subQ2=makeQuery(id+"F1.opExtrude","CAP_EDGE",EDGE,{"disambiguationData":[OSD([sQuery(id+"F0.wireOp",EDGE,"E118.MirrorCS")])],"isStart":false});Q13=makeQuery(id+"F8.imprint","IMPRINT",FACE,{"disambiguationData":[TD([[makeQuery(id+"F8.imprint","IMPRINT",EDGE,{"derivedFrom":subQ2}),1.0]])]});}
            var Q14;
            {var subQ2=makeQuery(id+"F1.opExtrude","CAP_EDGE",EDGE,{"disambiguationData":[OSD([sQuery(id+"F0.wireOp",EDGE,"E112.MirrorCS")])],"isStart":false});Q14=makeQuery(id+"F8.imprint","IMPRINT",FACE,{"disambiguationData":[TD([[makeQuery(id+"F8.imprint","IMPRINT",EDGE,{"derivedFrom":subQ2}),1.0]])]});}
            var Q15;
            {var subQ2=makeQuery(id+"F1.opExtrude","CAP_EDGE",EDGE,{"disambiguationData":[OSD([sQuery(id+"F0.wireOp",EDGE,"E124.MirrorCS")])],"isStart":false});Q15=makeQuery(id+"F8.imprint","IMPRINT",FACE,{"disambiguationData":[TD([[makeQuery(id+"F8.imprint","IMPRINT",EDGE,{"derivedFrom":subQ2}),1.0]])]});}
            extrude(context, id + "F11", {"entities" : qUnion([Q0, Q1, Q2, Q3, Q4, Q5, Q6, Q7, Q8, Q9, Q10, Q11, Q12, Q13, Q14, Q15]), "depth" : 50 * mm});
        }
        {
            var Q0;
            Q0=makeQuery(id+"F3.imprint","IMPRINT",FACE,{"disambiguationData":[TD([[makeQuery(id+"F3.imprint","IMPRINT",EDGE,{"derivedFrom":sQuery(id+"F3.wireOp",EDGE,"E171.0.3")}),1.0]])]});
            cPlane(context, id + "F12", {"entities" : qUnion([Q0]), "cplaneType" : CPlaneType.OFFSET, "offset" : 25 * mm, "width" : 150 * mm, "height" : 150 * mm});
        }
        {
            var Q0;
            Q0=makeQuery(id+"F4.opExtrude","SWEPT_BODY",BODY,{"disambiguationData":[OSD([sQuery(id+"F3.wireOp",EDGE,"E195.0.0"),sQuery(id+"F3.wireOp",EDGE,"E195.0.1"),sQuery(id+"F3.wireOp",EDGE,"E195.0.2"),sQuery(id+"F3.wireOp",EDGE,"E195.0.3")])]});
            var Q1;
            Q1=makeQuery(id+"F4.opExtrude","SWEPT_BODY",BODY,{"disambiguationData":[OSD([sQuery(id+"F3.wireOp",EDGE,"E194.0.0"),sQuery(id+"F3.wireOp",EDGE,"E194.0.1"),sQuery(id+"F3.wireOp",EDGE,"E194.0.2"),sQuery(id+"F3.wireOp",EDGE,"E194.0.3")])]});
            var Q2;
            Q2=makeQuery(id+"F4.opExtrude","SWEPT_BODY",BODY,{"disambiguationData":[OSD([sQuery(id+"F3.wireOp",EDGE,"E193.0.0"),sQuery(id+"F3.wireOp",EDGE,"E193.0.1"),sQuery(id+"F3.wireOp",EDGE,"E193.0.2"),sQuery(id+"F3.wireOp",EDGE,"E193.0.3")])]});
            var Q3;
            Q3=makeQuery(id+"F4.opExtrude","SWEPT_BODY",BODY,{"disambiguationData":[OSD([sQuery(id+"F3.wireOp",EDGE,"E192.0.0"),sQuery(id+"F3.wireOp",EDGE,"E192.0.1"),sQuery(id+"F3.wireOp",EDGE,"E192.0.2"),sQuery(id+"F3.wireOp",EDGE,"E192.0.3")])]});
            var Q4;
            Q4=makeQuery(id+"F4.opExtrude","SWEPT_BODY",BODY,{"disambiguationData":[OSD([sQuery(id+"F3.wireOp",EDGE,"E191.0.0"),sQuery(id+"F3.wireOp",EDGE,"E191.0.1"),sQuery(id+"F3.wireOp",EDGE,"E191.0.2"),sQuery(id+"F3.wireOp",EDGE,"E191.0.3")])]});
            var Q5;
            Q5=makeQuery(id+"F4.opExtrude","SWEPT_BODY",BODY,{"disambiguationData":[OSD([sQuery(id+"F3.wireOp",EDGE,"E190.0.0"),sQuery(id+"F3.wireOp",EDGE,"E190.0.1"),sQuery(id+"F3.wireOp",EDGE,"E190.0.2"),sQuery(id+"F3.wireOp",EDGE,"E190.0.3")])]});
            var Q6;
            Q6=makeQuery(id+"F4.opExtrude","SWEPT_BODY",BODY,{"disambiguationData":[OSD([sQuery(id+"F3.wireOp",EDGE,"E189.0.0"),sQuery(id+"F3.wireOp",EDGE,"E189.0.1"),sQuery(id+"F3.wireOp",EDGE,"E189.0.2"),sQuery(id+"F3.wireOp",EDGE,"E189.0.3")])]});
            var Q7;
            Q7=makeQuery(id+"F4.opExtrude","SWEPT_BODY",BODY,{"disambiguationData":[OSD([sQuery(id+"F3.wireOp",EDGE,"E188.0.0"),sQuery(id+"F3.wireOp",EDGE,"E188.0.1"),sQuery(id+"F3.wireOp",EDGE,"E188.0.2"),sQuery(id+"F3.wireOp",EDGE,"E188.0.3")])]});
            var Q8;
            Q8=makeQuery(id+"F4.opExtrude","SWEPT_BODY",BODY,{"disambiguationData":[OSD([sQuery(id+"F3.wireOp",EDGE,"E187.0.0"),sQuery(id+"F3.wireOp",EDGE,"E187.0.1"),sQuery(id+"F3.wireOp",EDGE,"E187.0.2"),sQuery(id+"F3.wireOp",EDGE,"E187.0.3")])]});
            var Q9;
            Q9=makeQuery(id+"F4.opExtrude","SWEPT_BODY",BODY,{"disambiguationData":[OSD([sQuery(id+"F3.wireOp",EDGE,"E179.0.0"),sQuery(id+"F3.wireOp",EDGE,"E179.0.1"),sQuery(id+"F3.wireOp",EDGE,"E179.0.2"),sQuery(id+"F3.wireOp",EDGE,"E179.0.3")])]});
            var Q10;
            Q10=makeQuery(id+"F4.opExtrude","SWEPT_BODY",BODY,{"disambiguationData":[OSD([sQuery(id+"F3.wireOp",EDGE,"E177.0.0"),sQuery(id+"F3.wireOp",EDGE,"E177.0.1"),sQuery(id+"F3.wireOp",EDGE,"E177.0.2"),sQuery(id+"F3.wireOp",EDGE,"E177.0.3")])]});
            var Q11;
            Q11=makeQuery(id+"F4.opExtrude","SWEPT_BODY",BODY,{"disambiguationData":[OSD([sQuery(id+"F3.wireOp",EDGE,"E176.0.0"),sQuery(id+"F3.wireOp",EDGE,"E176.0.1"),sQuery(id+"F3.wireOp",EDGE,"E176.0.2"),sQuery(id+"F3.wireOp",EDGE,"E176.0.3")])]});
            var Q12;
            Q12=makeQuery(id+"F4.opExtrude","SWEPT_BODY",BODY,{"disambiguationData":[OSD([sQuery(id+"F3.wireOp",EDGE,"E178.0.0"),sQuery(id+"F3.wireOp",EDGE,"E178.0.1"),sQuery(id+"F3.wireOp",EDGE,"E178.0.2"),sQuery(id+"F3.wireOp",EDGE,"E178.0.3")])]});
            var Q13;
            Q13=makeQuery(id+"F4.opExtrude","SWEPT_BODY",BODY,{"disambiguationData":[OSD([sQuery(id+"F3.wireOp",EDGE,"E175.0.0"),sQuery(id+"F3.wireOp",EDGE,"E175.0.1"),sQuery(id+"F3.wireOp",EDGE,"E175.0.2"),sQuery(id+"F3.wireOp",EDGE,"E175.0.3")])]});
            var Q14;
            Q14=makeQuery(id+"F4.opExtrude","SWEPT_BODY",BODY,{"disambiguationData":[OSD([sQuery(id+"F3.wireOp",EDGE,"E174.0.0"),sQuery(id+"F3.wireOp",EDGE,"E174.0.1"),sQuery(id+"F3.wireOp",EDGE,"E174.0.2"),sQuery(id+"F3.wireOp",EDGE,"E174.0.3")])]});
            var Q15;
            Q15=makeQuery(id+"F4.opExtrude","SWEPT_BODY",BODY,{"disambiguationData":[OSD([sQuery(id+"F3.wireOp",EDGE,"E173.0.0"),sQuery(id+"F3.wireOp",EDGE,"E173.0.1"),sQuery(id+"F3.wireOp",EDGE,"E173.0.2"),sQuery(id+"F3.wireOp",EDGE,"E173.0.3")])]});
            var Q16;
            Q16=makeQuery(id+"F4.opExtrude","SWEPT_BODY",BODY,{"disambiguationData":[OSD([sQuery(id+"F3.wireOp",EDGE,"E172.0.0"),sQuery(id+"F3.wireOp",EDGE,"E172.0.1"),sQuery(id+"F3.wireOp",EDGE,"E172.0.2"),sQuery(id+"F3.wireOp",EDGE,"E172.0.3")])]});
            var Q17;
            Q17=makeQuery(id+"F4.opExtrude","SWEPT_BODY",BODY,{"disambiguationData":[OSD([sQuery(id+"F3.wireOp",EDGE,"E171.0.0"),sQuery(id+"F3.wireOp",EDGE,"E171.0.1"),sQuery(id+"F3.wireOp",EDGE,"E171.0.2"),sQuery(id+"F3.wireOp",EDGE,"E171.0.3")])]});
            var Q18;
            Q18=makeQuery(id+"F7.opExtrude","SWEPT_BODY",BODY,{"disambiguationData":[OSD([sQuery(id+"F6.wireOp",EDGE,"E209.bottom"),sQuery(id+"F6.wireOp",EDGE,"E209.top"),sQuery(id+"F6.wireOp",EDGE,"E209.left"),sQuery(id+"F6.wireOp",EDGE,"E209.right")])]});
            var Q19;
            Q19=makeQuery(id+"F7.opExtrude","SWEPT_BODY",BODY,{"disambiguationData":[OSD([sQuery(id+"F6.wireOp",EDGE,"E210.bottom"),sQuery(id+"F6.wireOp",EDGE,"E210.top"),sQuery(id+"F6.wireOp",EDGE,"E210.left"),sQuery(id+"F6.wireOp",EDGE,"E210.right")])]});
            var Q20;
            Q20=makeQuery(id+"F7.opExtrude","SWEPT_BODY",BODY,{"disambiguationData":[OSD([sQuery(id+"F6.wireOp",EDGE,"E211.bottom"),sQuery(id+"F6.wireOp",EDGE,"E211.top"),sQuery(id+"F6.wireOp",EDGE,"E211.left"),sQuery(id+"F6.wireOp",EDGE,"E211.right")])]});
            var Q21;
            Q21=makeQuery(id+"F7.opExtrude","SWEPT_BODY",BODY,{"disambiguationData":[OSD([sQuery(id+"F6.wireOp",EDGE,"E212.bottom"),sQuery(id+"F6.wireOp",EDGE,"E212.top"),sQuery(id+"F6.wireOp",EDGE,"E212.left"),sQuery(id+"F6.wireOp",EDGE,"E212.right")])]});
            var Q22;
            Q22=makeQuery(id+"F7.opExtrude","SWEPT_BODY",BODY,{"disambiguationData":[OSD([sQuery(id+"F6.wireOp",EDGE,"E213.bottom"),sQuery(id+"F6.wireOp",EDGE,"E213.top"),sQuery(id+"F6.wireOp",EDGE,"E213.left"),sQuery(id+"F6.wireOp",EDGE,"E213.right")])]});
            var Q23;
            Q23=makeQuery(id+"F7.opExtrude","SWEPT_BODY",BODY,{"disambiguationData":[OSD([sQuery(id+"F6.wireOp",EDGE,"E214.bottom"),sQuery(id+"F6.wireOp",EDGE,"E214.top"),sQuery(id+"F6.wireOp",EDGE,"E214.left"),sQuery(id+"F6.wireOp",EDGE,"E214.right")])]});
            var Q24;
            Q24=makeQuery(id+"F7.opExtrude","SWEPT_BODY",BODY,{"disambiguationData":[OSD([sQuery(id+"F6.wireOp",EDGE,"E215.bottom"),sQuery(id+"F6.wireOp",EDGE,"E215.top"),sQuery(id+"F6.wireOp",EDGE,"E215.left"),sQuery(id+"F6.wireOp",EDGE,"E215.right")])]});
            var Q25;
            Q25=makeQuery(id+"F7.opExtrude","SWEPT_BODY",BODY,{"disambiguationData":[OSD([sQuery(id+"F6.wireOp",EDGE,"E216.bottom"),sQuery(id+"F6.wireOp",EDGE,"E216.top"),sQuery(id+"F6.wireOp",EDGE,"E216.left"),sQuery(id+"F6.wireOp",EDGE,"E216.right")])]});
            var Q26;
            Q26=makeQuery(id+"F7.opExtrude","SWEPT_BODY",BODY,{"disambiguationData":[OSD([sQuery(id+"F6.wireOp",EDGE,"E208.bottom"),sQuery(id+"F6.wireOp",EDGE,"E208.top"),sQuery(id+"F6.wireOp",EDGE,"E208.left"),sQuery(id+"F6.wireOp",EDGE,"E208.right")])]});
            var Q27;
            Q27=makeQuery(id+"F7.opExtrude","SWEPT_BODY",BODY,{"disambiguationData":[OSD([sQuery(id+"F6.wireOp",EDGE,"E207.bottom"),sQuery(id+"F6.wireOp",EDGE,"E207.top"),sQuery(id+"F6.wireOp",EDGE,"E207.left"),sQuery(id+"F6.wireOp",EDGE,"E207.right")])]});
            var Q28;
            Q28=makeQuery(id+"F7.opExtrude","SWEPT_BODY",BODY,{"disambiguationData":[OSD([sQuery(id+"F6.wireOp",EDGE,"E206.bottom"),sQuery(id+"F6.wireOp",EDGE,"E206.top"),sQuery(id+"F6.wireOp",EDGE,"E206.left"),sQuery(id+"F6.wireOp",EDGE,"E206.right")])]});
            var Q29;
            Q29=makeQuery(id+"F7.opExtrude","SWEPT_BODY",BODY,{"disambiguationData":[OSD([sQuery(id+"F6.wireOp",EDGE,"E205.bottom"),sQuery(id+"F6.wireOp",EDGE,"E205.top"),sQuery(id+"F6.wireOp",EDGE,"E205.left"),sQuery(id+"F6.wireOp",EDGE,"E205.right")])]});
            var Q30;
            Q30=makeQuery(id+"F7.opExtrude","SWEPT_BODY",BODY,{"disambiguationData":[OSD([sQuery(id+"F6.wireOp",EDGE,"E204.bottom"),sQuery(id+"F6.wireOp",EDGE,"E204.top"),sQuery(id+"F6.wireOp",EDGE,"E204.left"),sQuery(id+"F6.wireOp",EDGE,"E204.right")])]});
            var Q31;
            Q31=makeQuery(id+"F7.opExtrude","SWEPT_BODY",BODY,{"disambiguationData":[OSD([sQuery(id+"F6.wireOp",EDGE,"E203.bottom"),sQuery(id+"F6.wireOp",EDGE,"E203.top"),sQuery(id+"F6.wireOp",EDGE,"E203.left"),sQuery(id+"F6.wireOp",EDGE,"E203.right")])]});
            var Q32;
            Q32=qCreatedBy(id+"F12.planeOp",FACE);
            mirror(context, id + "F13", {"entities" : qUnion([Q0, Q1, Q2, Q3, Q4, Q5, Q6, Q7, Q8, Q9, Q10, Q11, Q12, Q13, Q14, Q15, Q16, Q17, Q18, Q19, Q20, Q21, Q22, Q23, Q24, Q25, Q26, Q27, Q28, Q29, Q30, Q31]), "mirrorPlane" : qUnion([Q32])});
        }
        {
            var Q0;
            Q0=makeQuery(id+"F5.opExtrude","SWEPT_FACE",FACE,{"disambiguationData":[OSD([sQuery(id+"F0.wireOp",EDGE,"E0.left")])]});
            var sketch = newSketch(context, id + "F14", { "sketchPlane" : qUnion([Q0])});
            skLineSegment(sketch, "E252.0.0", {"start": v(-83.5, 41) * mm, "end": v(-86.5, 41) * mm});
            skLineSegment(sketch, "E252.0.1", {"start": v(-86.5, 41) * mm, "end": v(-86.5, 47) * mm});
            skLineSegment(sketch, "E252.0.2", {"start": v(-86.5, 47) * mm, "end": v(-83.5, 47) * mm});
            skLineSegment(sketch, "E252.0.3", {"start": v(-83.5, 47) * mm, "end": v(-83.5, 44) * mm});
            skLineSegment(sketch, "E252.0.4", {"start": v(-83.5, 44) * mm, "end": v(-83.5, 41) * mm});
            skLineSegment(sketch, "E253.0.0", {"start": v(-87.5, 4) * mm, "end": v(87.5, 4) * mm});
            skLineSegment(sketch, "E253.0.1", {"start": v(87.5, 4) * mm, "end": v(87.5, 54) * mm});
            skLineSegment(sketch, "E253.0.2", {"start": v(87.5, 54) * mm, "end": v(-87.5, 54) * mm});
            skLineSegment(sketch, "E253.0.3", {"start": v(-87.5, 54) * mm, "end": v(-87.5, 4) * mm});
            skLineSegment(sketch, "E254.0", {"start": v(-83.5, 32) * mm, "end": v(-86.5, 32) * mm});
            skLineSegment(sketch, "E255.0", {"start": v(-83.5, 32) * mm, "end": v(-83.5, 26) * mm});
            skLineSegment(sketch, "E256.0", {"start": v(-86.5, 26) * mm, "end": v(-83.5, 26) * mm});
            skLineSegment(sketch, "E257.0", {"start": v(-86.5, 26) * mm, "end": v(-86.5, 32) * mm});
            skLineSegment(sketch, "E258.0", {"start": v(-86.5, 17) * mm, "end": v(-83.5, 17) * mm});
            skLineSegment(sketch, "E259.0", {"start": v(-83.5, 17) * mm, "end": v(-83.5, 11) * mm});
            skLineSegment(sketch, "E260.0", {"start": v(-86.5, 11) * mm, "end": v(-83.5, 11) * mm});
            skLineSegment(sketch, "E261.0", {"start": v(-86.5, 11) * mm, "end": v(-86.5, 17) * mm});
            skLineSegment(sketch, "E262.0", {"start": v(86.5, 32) * mm, "end": v(83.5, 32) * mm});
            skLineSegment(sketch, "E263.0", {"start": v(86.5, 26) * mm, "end": v(86.5, 32) * mm});
            skLineSegment(sketch, "E264.0", {"start": v(83.5, 26) * mm, "end": v(83.5, 32) * mm});
            skLineSegment(sketch, "E265.0", {"start": v(86.5, 26) * mm, "end": v(83.5, 26) * mm});
            skPoint(sketch, "E266.0", {"position": v(85, 47) * mm});
            skLineSegment(sketch, "E267.0", {"start": v(86.5, 47) * mm, "end": v(83.5, 47) * mm});
            skLineSegment(sketch, "E268.0", {"start": v(86.5, 41) * mm, "end": v(86.5, 47) * mm});
            skLineSegment(sketch, "E269.0", {"start": v(83.5, 41) * mm, "end": v(83.5, 47) * mm});
            skLineSegment(sketch, "E270.0", {"start": v(86.5, 41) * mm, "end": v(83.5, 41) * mm});
            skLineSegment(sketch, "E271.0", {"start": v(86.5, 17) * mm, "end": v(83.5, 17) * mm});
            skLineSegment(sketch, "E272.0", {"start": v(86.5, 11) * mm, "end": v(86.5, 17) * mm});
            skLineSegment(sketch, "E273.0", {"start": v(83.5, 11) * mm, "end": v(83.5, 17) * mm});
            skLineSegment(sketch, "E274.0", {"start": v(86.5, 11) * mm, "end": v(83.5, 11) * mm});
            skSolve(sketch);
        }
        {
            var Q0;
            Q0=makeQuery(id+"F14.imprint","IMPRINT",FACE,{"disambiguationData":[TD([[makeQuery(id+"F14.imprint","IMPRINT",EDGE,{"derivedFrom":sQuery(id+"F14.wireOp",EDGE,"E252.0.0")}),1.0]])]});
            var Q1;
            Q1=makeQuery(id+"F14.imprint","IMPRINT",FACE,{"disambiguationData":[TD([[makeQuery(id+"F14.imprint","IMPRINT",EDGE,{"derivedFrom":sQuery(id+"F14.wireOp",EDGE,"E254.0")}),1.0]])]});
            var Q2;
            Q2=makeQuery(id+"F14.imprint","IMPRINT",FACE,{"disambiguationData":[TD([[makeQuery(id+"F14.imprint","IMPRINT",EDGE,{"derivedFrom":sQuery(id+"F14.wireOp",EDGE,"E258.0")}),-1.0]])]});
            var Q3;
            Q3=makeQuery(id+"F14.imprint","IMPRINT",FACE,{"disambiguationData":[TD([[makeQuery(id+"F14.imprint","IMPRINT",EDGE,{"derivedFrom":sQuery(id+"F14.wireOp",EDGE,"E267.0")}),1.0]])]});
            var Q4;
            Q4=makeQuery(id+"F14.imprint","IMPRINT",FACE,{"disambiguationData":[TD([[makeQuery(id+"F14.imprint","IMPRINT",EDGE,{"derivedFrom":sQuery(id+"F14.wireOp",EDGE,"E262.0")}),1.0]])]});
            var Q5;
            Q5=makeQuery(id+"F14.imprint","IMPRINT",FACE,{"disambiguationData":[TD([[makeQuery(id+"F14.imprint","IMPRINT",EDGE,{"derivedFrom":sQuery(id+"F14.wireOp",EDGE,"E271.0")}),1.0]])]});
            extrude(context, id + "F15", {"entities" : qUnion([Q0, Q1, Q2, Q3, Q4, Q5]), "oppositeDirection" : true, "depth" : 4 * mm});
        }
        {
            var Q0;
            Q0=makeQuery(id+"F5.opExtrude","SWEPT_BODY",BODY,{"disambiguationData":[OSD([sQuery(id+"F0.wireOp",EDGE,"E0.bottom"),sQuery(id+"F0.wireOp",EDGE,"E0.left"),sQuery(id+"F0.wireOp",EDGE,"E8.0.2.0"),sQuery(id+"F0.wireOp",EDGE,"E8.0.2.1"),sQuery(id+"F0.wireOp",EDGE,"E8.0.2.2"),sQuery(id+"F0.wireOp",EDGE,"E8.0.2.3"),sQuery(id+"F0.wireOp",EDGE,"E8.0.3.0"),sQuery(id+"F0.wireOp",EDGE,"E8.0.3.1"),sQuery(id+"F0.wireOp",EDGE,"E8.0.3.2"),sQuery(id+"F0.wireOp",EDGE,"E8.0.3.3"),sQuery(id+"F0.wireOp",EDGE,"E8.0.4.0"),sQuery(id+"F0.wireOp",EDGE,"E8.0.4.1"),sQuery(id+"F0.wireOp",EDGE,"E8.0.4.2"),sQuery(id+"F0.wireOp",EDGE,"E8.0.4.3"),sQuery(id+"F0.wireOp",EDGE,"E9.MirrorCS"),sQuery(id+"F0.wireOp",EDGE,"E12.MirrorCS"),sQuery(id+"F0.wireOp",EDGE,"E13.MirrorCS"),sQuery(id+"F0.wireOp",EDGE,"E14.MirrorCS"),sQuery(id+"F0.wireOp",EDGE,"E15.MirrorCS"),sQuery(id+"F0.wireOp",EDGE,"E16.MirrorCS"),sQuery(id+"F0.wireOp",EDGE,"E27.MirrorCS"),sQuery(id+"F0.wireOp",EDGE,"E28.MirrorCS"),sQuery(id+"F0.wireOp",EDGE,"E29.MirrorCS"),sQuery(id+"F0.wireOp",EDGE,"E30.MirrorCS"),sQuery(id+"F0.wireOp",EDGE,"E31"),sQuery(id+"F0.wireOp",EDGE,"E46.MirrorCS"),sQuery(id+"F2.wireOp",EDGE,"E153"),sQuery(id+"F2.wireOp",EDGE,"E155"),sQuery(id+"F2.wireOp",EDGE,"E156")])]});
            var Q1;
            Q1=qCreatedBy(makeId("Right.planeOp"),FACE);
            mirror(context, id + "F16", {"entities" : qUnion([Q0]), "mirrorPlane" : qUnion([Q1])});
        }
        {
            var Q0;
            Q0=makeQuery(id+"F16.opPattern","COPY",FACE,{"derivedFrom":makeQuery(id+"F10.boolean.opBoolean","COPY",FACE,{"derivedFrom":makeQuery(id+"F10.opExtrude","SWEPT_FACE",FACE,{"disambiguationData":[OSD([sQuery(id+"F9.wireOp",EDGE,"E240.MirrorCS"),sQuery(id+"F9.wireOp",EDGE,"E241.MirrorCS")])]})}),"instanceName":"1"});
            var Q1;
            Q1=makeQuery(id+"F16.opPattern","COPY",FACE,{"derivedFrom":makeQuery(id+"F10.boolean.opBoolean","COPY",FACE,{"derivedFrom":makeQuery(id+"F10.opExtrude","SWEPT_FACE",FACE,{"disambiguationData":[OSD([sQuery(id+"F9.wireOp",EDGE,"E244.MirrorCS"),sQuery(id+"F9.wireOp",EDGE,"E245.MirrorCS")])]})}),"instanceName":"1"});
            var Q2;
            Q2=makeQuery(id+"F16.opPattern","COPY",FACE,{"derivedFrom":makeQuery(id+"F10.boolean.opBoolean","COPY",FACE,{"derivedFrom":makeQuery(id+"F10.opExtrude","SWEPT_FACE",FACE,{"disambiguationData":[OSD([sQuery(id+"F9.wireOp",EDGE,"E248.MirrorCS"),sQuery(id+"F9.wireOp",EDGE,"E249.MirrorCS")])]})}),"instanceName":"1"});
            var Q3;
            {var subQ0=sQuery(id+"F9.wireOp",EDGE,"E229");Q3=makeQuery(id+"F16.opPattern","COPY",FACE,{"derivedFrom":makeQuery(id+"F10.boolean.opBoolean","COPY",FACE,{"derivedFrom":makeQuery(id+"F10.opExtrude","SWEPT_FACE",FACE,{"disambiguationData":[OSD([subQ0]),TDD([makeQuery(id+"F9.imprint","IMPRINT",EDGE,{"disambiguationData":[TD([[makeQuery(id+"F9.imprint","INTERSECT",VERTEX,{"derivedFrom":[subQ0,sQuery(id+"F9.wireOp",EDGE,"E234.0.1.0")]}),1.0]])],"derivedFrom":subQ0})])]})}),"instanceName":"1"});}
            var Q4;
            Q4=makeQuery(id+"F16.opPattern","COPY",FACE,{"derivedFrom":makeQuery(id+"F10.boolean.opBoolean","COPY",FACE,{"derivedFrom":makeQuery(id+"F10.opExtrude","SWEPT_FACE",FACE,{"disambiguationData":[OSD([sQuery(id+"F9.wireOp",EDGE,"E229"),sQuery(id+"F9.wireOp",EDGE,"E231.left")])]})}),"instanceName":"1"});
            var Q5;
            {var subQ0=sQuery(id+"F9.wireOp",EDGE,"E229");Q5=makeQuery(id+"F16.opPattern","COPY",FACE,{"derivedFrom":makeQuery(id+"F10.boolean.opBoolean","COPY",FACE,{"derivedFrom":makeQuery(id+"F10.opExtrude","SWEPT_FACE",FACE,{"disambiguationData":[OSD([subQ0]),TDD([makeQuery(id+"F9.imprint","IMPRINT",EDGE,{"disambiguationData":[TD([[makeQuery(id+"F9.imprint","INTERSECT",VERTEX,{"derivedFrom":[subQ0,sQuery(id+"F9.wireOp",EDGE,"E235.MirrorCS")]}),1.0]])],"derivedFrom":subQ0})])]})}),"instanceName":"1"});}
            extrude(context, id + "F17", {"entities" : qUnion([Q0, Q1, Q2, Q3, Q4, Q5]), "depth" : 3 * mm});
        }
        {
            var Q0;
            Q0=makeQuery(id+"F1.opExtrude","SWEPT_BODY",BODY,{"disambiguationData":[OSD([sQuery(id+"F0.wireOp",EDGE,"E0.bottom"),sQuery(id+"F0.wireOp",EDGE,"E0.left"),sQuery(id+"F0.wireOp",EDGE,"E0.right"),sQuery(id+"F0.wireOp",EDGE,"E4.bottom"),sQuery(id+"F0.wireOp",EDGE,"E4.left"),sQuery(id+"F0.wireOp",EDGE,"E4.right"),sQuery(id+"F0.wireOp",EDGE,"E5.MirrorCS"),sQuery(id+"F0.wireOp",EDGE,"E6.MirrorCS"),sQuery(id+"F0.wireOp",EDGE,"E7.MirrorCS"),sQuery(id+"F0.wireOp",EDGE,"E8.0.1.0"),sQuery(id+"F0.wireOp",EDGE,"E8.0.1.1"),sQuery(id+"F0.wireOp",EDGE,"E8.0.1.2"),sQuery(id+"F0.wireOp",EDGE,"E8.0.1.3"),sQuery(id+"F0.wireOp",EDGE,"E8.0.1.4"),sQuery(id+"F0.wireOp",EDGE,"E8.0.1.5"),sQuery(id+"F0.wireOp",EDGE,"E8.0.2.0"),sQuery(id+"F0.wireOp",EDGE,"E8.0.2.1"),sQuery(id+"F0.wireOp",EDGE,"E8.0.2.2"),sQuery(id+"F0.wireOp",EDGE,"E8.0.2.3"),sQuery(id+"F0.wireOp",EDGE,"E8.0.2.4"),sQuery(id+"F0.wireOp",EDGE,"E8.0.2.5"),sQuery(id+"F0.wireOp",EDGE,"E8.0.3.0"),sQuery(id+"F0.wireOp",EDGE,"E8.0.3.1"),sQuery(id+"F0.wireOp",EDGE,"E8.0.3.2"),sQuery(id+"F0.wireOp",EDGE,"E8.0.3.3"),sQuery(id+"F0.wireOp",EDGE,"E8.0.3.4"),sQuery(id+"F0.wireOp",EDGE,"E8.0.3.5"),sQuery(id+"F0.wireOp",EDGE,"E8.0.4.0"),sQuery(id+"F0.wireOp",EDGE,"E8.0.4.1"),sQuery(id+"F0.wireOp",EDGE,"E8.0.4.2"),sQuery(id+"F0.wireOp",EDGE,"E8.0.4.3"),sQuery(id+"F0.wireOp",EDGE,"E8.0.4.4"),sQuery(id+"F0.wireOp",EDGE,"E8.0.4.5"),sQuery(id+"F0.wireOp",EDGE,"E9.MirrorCS"),sQuery(id+"F0.wireOp",EDGE,"E10.MirrorCS"),sQuery(id+"F0.wireOp",EDGE,"E11.MirrorCS"),sQuery(id+"F0.wireOp",EDGE,"E12.MirrorCS"),sQuery(id+"F0.wireOp",EDGE,"E13.MirrorCS"),sQuery(id+"F0.wireOp",EDGE,"E14.MirrorCS"),sQuery(id+"F0.wireOp",EDGE,"E15.MirrorCS"),sQuery(id+"F0.wireOp",EDGE,"E16.MirrorCS"),sQuery(id+"F0.wireOp",EDGE,"E17.MirrorCS"),sQuery(id+"F0.wireOp",EDGE,"E18.MirrorCS"),sQuery(id+"F0.wireOp",EDGE,"E19.MirrorCS"),sQuery(id+"F0.wireOp",EDGE,"E20.MirrorCS"),sQuery(id+"F0.wireOp",EDGE,"E21.MirrorCS"),sQuery(id+"F0.wireOp",EDGE,"E22.MirrorCS"),sQuery(id+"F0.wireOp",EDGE,"E23.MirrorCS"),sQuery(id+"F0.wireOp",EDGE,"E24.MirrorCS"),sQuery(id+"F0.wireOp",EDGE,"E25.MirrorCS"),sQuery(id+"F0.wireOp",EDGE,"E26.MirrorCS"),sQuery(id+"F0.wireOp",EDGE,"E27.MirrorCS"),sQuery(id+"F0.wireOp",EDGE,"E28.MirrorCS"),sQuery(id+"F0.wireOp",EDGE,"E29.MirrorCS"),sQuery(id+"F0.wireOp",EDGE,"E30.MirrorCS"),sQuery(id+"F0.wireOp",EDGE,"E31"),sQuery(id+"F0.wireOp",EDGE,"E32.bottom"),sQuery(id+"F0.wireOp",EDGE,"E32.top"),sQuery(id+"F0.wireOp",EDGE,"E32.right"),sQuery(id+"F0.wireOp",EDGE,"E33.MirrorCS"),sQuery(id+"F0.wireOp",EDGE,"E34.MirrorCS"),sQuery(id+"F0.wireOp",EDGE,"E35.MirrorCS"),sQuery(id+"F0.wireOp",EDGE,"E36.1.0.0"),sQuery(id+"F0.wireOp",EDGE,"E36.1.0.1"),sQuery(id+"F0.wireOp",EDGE,"E36.1.0.2"),sQuery(id+"F0.wireOp",EDGE,"E36.1.0.3"),sQuery(id+"F0.wireOp",EDGE,"E36.1.0.4"),sQuery(id+"F0.wireOp",EDGE,"E36.1.0.5"),sQuery(id+"F0.wireOp",EDGE,"E36.2.0.0"),sQuery(id+"F0.wireOp",EDGE,"E36.2.0.1"),sQuery(id+"F0.wireOp",EDGE,"E36.2.0.2"),sQuery(id+"F0.wireOp",EDGE,"E36.2.0.3"),sQuery(id+"F0.wireOp",EDGE,"E36.2.0.4"),sQuery(id+"F0.wireOp",EDGE,"E36.2.0.5"),sQuery(id+"F0.wireOp",EDGE,"E36.3.0.0"),sQuery(id+"F0.wireOp",EDGE,"E36.3.0.1"),sQuery(id+"F0.wireOp",EDGE,"E36.3.0.2"),sQuery(id+"F0.wireOp",EDGE,"E36.3.0.3"),sQuery(id+"F0.wireOp",EDGE,"E36.3.0.4"),sQuery(id+"F0.wireOp",EDGE,"E36.3.0.5"),sQuery(id+"F0.wireOp",EDGE,"E37.MirrorCS"),sQuery(id+"F0.wireOp",EDGE,"E38.MirrorCS"),sQuery(id+"F0.wireOp",EDGE,"E39.MirrorCS"),sQuery(id+"F0.wireOp",EDGE,"E40.MirrorCS"),sQuery(id+"F0.wireOp",EDGE,"E41.MirrorCS"),sQuery(id+"F0.wireOp",EDGE,"E42.MirrorCS"),sQuery(id+"F0.wireOp",EDGE,"E43.MirrorCS"),sQuery(id+"F0.wireOp",EDGE,"E44.MirrorCS"),sQuery(id+"F0.wireOp",EDGE,"E45.MirrorCS"),sQuery(id+"F0.wireOp",EDGE,"E46.MirrorCS"),sQuery(id+"F0.wireOp",EDGE,"E47.MirrorCS"),sQuery(id+"F0.wireOp",EDGE,"E48.MirrorCS"),sQuery(id+"F0.wireOp",EDGE,"E49.MirrorCS"),sQuery(id+"F0.wireOp",EDGE,"E50.MirrorCS"),sQuery(id+"F0.wireOp",EDGE,"E51.MirrorCS"),sQuery(id+"F0.wireOp",EDGE,"E52.MirrorCS"),sQuery(id+"F0.wireOp",EDGE,"E53.MirrorCS"),sQuery(id+"F0.wireOp",EDGE,"E54.MirrorCS"),sQuery(id+"F0.wireOp",EDGE,"E55.MirrorCS"),sQuery(id+"F0.wireOp",EDGE,"E56.MirrorCS"),sQuery(id+"F0.wireOp",EDGE,"E57.MirrorCS"),sQuery(id+"F0.wireOp",EDGE,"E58.MirrorCS"),sQuery(id+"F0.wireOp",EDGE,"E59.MirrorCS"),sQuery(id+"F0.wireOp",EDGE,"E60.MirrorCS"),sQuery(id+"F0.wireOp",EDGE,"E61.MirrorCS"),sQuery(id+"F0.wireOp",EDGE,"E62.MirrorCS"),sQuery(id+"F0.wireOp",EDGE,"E63.MirrorCS"),sQuery(id+"F0.wireOp",EDGE,"E64.MirrorCS"),sQuery(id+"F0.wireOp",EDGE,"E65.MirrorCS"),sQuery(id+"F0.wireOp",EDGE,"E66.MirrorCS"),sQuery(id+"F0.wireOp",EDGE,"E67.MirrorCS"),sQuery(id+"F0.wireOp",EDGE,"E68.MirrorCS"),sQuery(id+"F0.wireOp",EDGE,"E69.MirrorCS"),sQuery(id+"F0.wireOp",EDGE,"E70.MirrorCS"),sQuery(id+"F0.wireOp",EDGE,"E71.MirrorCS"),sQuery(id+"F0.wireOp",EDGE,"E72.MirrorCS"),sQuery(id+"F0.wireOp",EDGE,"E73.MirrorCS"),sQuery(id+"F0.wireOp",EDGE,"E74.MirrorCS"),sQuery(id+"F0.wireOp",EDGE,"E75.MirrorCS"),sQuery(id+"F0.wireOp",EDGE,"E77.MirrorCS"),sQuery(id+"F0.wireOp",EDGE,"E78.MirrorCS"),sQuery(id+"F0.wireOp",EDGE,"E80.MirrorCS"),sQuery(id+"F0.wireOp",EDGE,"E81.MirrorCS"),sQuery(id+"F0.wireOp",EDGE,"E82.MirrorCS"),sQuery(id+"F0.wireOp",EDGE,"E83.MirrorCS"),sQuery(id+"F0.wireOp",EDGE,"E84.MirrorCS"),sQuery(id+"F0.wireOp",EDGE,"E85.MirrorCS"),sQuery(id+"F0.wireOp",EDGE,"E86.MirrorCS"),sQuery(id+"F0.wireOp",EDGE,"E87.MirrorCS"),sQuery(id+"F0.wireOp",EDGE,"E88.MirrorCS"),sQuery(id+"F0.wireOp",EDGE,"E89.MirrorCS"),sQuery(id+"F0.wireOp",EDGE,"E90.MirrorCS"),sQuery(id+"F0.wireOp",EDGE,"E91.MirrorCS"),sQuery(id+"F0.wireOp",EDGE,"E92.MirrorCS"),sQuery(id+"F0.wireOp",EDGE,"E93.MirrorCS"),sQuery(id+"F0.wireOp",EDGE,"E94.MirrorCS"),sQuery(id+"F0.wireOp",EDGE,"E95.MirrorCS"),sQuery(id+"F0.wireOp",EDGE,"E96.MirrorCS"),sQuery(id+"F0.wireOp",EDGE,"E97.MirrorCS"),sQuery(id+"F0.wireOp",EDGE,"E98.MirrorCS"),sQuery(id+"F0.wireOp",EDGE,"E99.MirrorCS"),sQuery(id+"F0.wireOp",EDGE,"E100.MirrorCS"),sQuery(id+"F0.wireOp",EDGE,"E101.MirrorCS"),sQuery(id+"F0.wireOp",EDGE,"E102.MirrorCS"),sQuery(id+"F0.wireOp",EDGE,"E103.MirrorCS"),sQuery(id+"F0.wireOp",EDGE,"E104.MirrorCS"),sQuery(id+"F0.wireOp",EDGE,"E105.MirrorCS"),sQuery(id+"F0.wireOp",EDGE,"E106.MirrorCS"),sQuery(id+"F0.wireOp",EDGE,"E107.MirrorCS"),sQuery(id+"F0.wireOp",EDGE,"E108"),sQuery(id+"F0.wireOp",EDGE,"E109"),sQuery(id+"F0.wireOp",EDGE,"E110.MirrorCS"),sQuery(id+"F0.wireOp",EDGE,"E111.MirrorCS"),sQuery(id+"F0.wireOp",EDGE,"E112.MirrorCS"),sQuery(id+"F0.wireOp",EDGE,"E113.MirrorCS"),sQuery(id+"F0.wireOp",EDGE,"E114.MirrorCS"),sQuery(id+"F0.wireOp",EDGE,"E115.MirrorCS"),sQuery(id+"F0.wireOp",EDGE,"E116.MirrorCS"),sQuery(id+"F0.wireOp",EDGE,"E117.MirrorCS"),sQuery(id+"F0.wireOp",EDGE,"E118.MirrorCS"),sQuery(id+"F0.wireOp",EDGE,"E119.MirrorCS"),sQuery(id+"F0.wireOp",EDGE,"E120.MirrorCS"),sQuery(id+"F0.wireOp",EDGE,"E121.MirrorCS"),sQuery(id+"F0.wireOp",EDGE,"E122.MirrorCS"),sQuery(id+"F0.wireOp",EDGE,"E123.MirrorCS"),sQuery(id+"F0.wireOp",EDGE,"E124.MirrorCS"),sQuery(id+"F0.wireOp",EDGE,"E125.MirrorCS"),sQuery(id+"F0.wireOp",EDGE,"E126.MirrorCS"),sQuery(id+"F0.wireOp",EDGE,"E127.MirrorCS"),sQuery(id+"F0.wireOp",EDGE,"E129.MirrorCS"),sQuery(id+"F0.wireOp",EDGE,"E130.MirrorCS"),sQuery(id+"F0.wireOp",EDGE,"E131.MirrorCS"),sQuery(id+"F0.wireOp",EDGE,"E132.MirrorCS"),sQuery(id+"F0.wireOp",EDGE,"E133.MirrorCS"),sQuery(id+"F0.wireOp",EDGE,"E134.MirrorCS"),sQuery(id+"F0.wireOp",EDGE,"E135.MirrorCS"),sQuery(id+"F0.wireOp",EDGE,"E136.MirrorCS"),sQuery(id+"F0.wireOp",EDGE,"E137.MirrorCS"),sQuery(id+"F0.wireOp",EDGE,"E138.MirrorCS"),sQuery(id+"F0.wireOp",EDGE,"E139.MirrorCS"),sQuery(id+"F0.wireOp",EDGE,"E140.MirrorCS"),sQuery(id+"F0.wireOp",EDGE,"E141.MirrorCS"),sQuery(id+"F0.wireOp",EDGE,"E142.MirrorCS"),sQuery(id+"F0.wireOp",EDGE,"E143.MirrorCS"),sQuery(id+"F0.wireOp",EDGE,"E144.MirrorCS"),sQuery(id+"F0.wireOp",EDGE,"E145.MirrorCS"),sQuery(id+"F0.wireOp",EDGE,"E146.MirrorCS"),sQuery(id+"F0.wireOp",EDGE,"E147.MirrorCS"),sQuery(id+"F0.wireOp",EDGE,"E148.MirrorCS"),sQuery(id+"F0.wireOp",EDGE,"E149.MirrorCS"),sQuery(id+"F0.wireOp",EDGE,"E150.MirrorCS"),sQuery(id+"F0.wireOp",EDGE,"E151")])]});
            var Q1;
            Q1=qCreatedBy(id+"F12.planeOp",FACE);
            mirror(context, id + "F18", {"entities" : qUnion([Q0]), "mirrorPlane" : qUnion([Q1])});
        }
        {
            var Q0;
            Q0=makeQuery(id+"F3.imprint","IMPRINT",FACE,{"disambiguationData":[TD([[makeQuery(id+"F3.imprint","IMPRINT",EDGE,{"derivedFrom":sQuery(id+"F3.wireOp",EDGE,"E171.0.3")}),1.0]])]});
            var sketch = newSketch(context, id + "F19", { "sketchPlane" : qUnion([Q0])});
            skLineSegment(sketch, "E275.bottom", {"start": v(-65.37, -20.06) * mm, "end": v(-39.37, -20.06) * mm});
            skLineSegment(sketch, "E275.top", {"start": v(-65.37, -80.06) * mm, "end": v(-39.37, -80.06) * mm});
            skLineSegment(sketch, "E275.left", {"start": v(-65.37, -20.06) * mm, "end": v(-65.37, -80.06) * mm});
            skLineSegment(sketch, "E275.right", {"start": v(-39.37, -20.06) * mm, "end": v(-39.37, -80.06) * mm});
            skLineSegment(sketch, "E276.MirrorCS", {"start": v(65.37, -20.06) * mm, "end": v(39.37, -20.06) * mm});
            skLineSegment(sketch, "E277.MirrorCS", {"start": v(65.37, -20.06) * mm, "end": v(65.37, -80.06) * mm});
            skLineSegment(sketch, "E278.MirrorCS", {"start": v(65.37, -80.06) * mm, "end": v(39.37, -80.06) * mm});
            skLineSegment(sketch, "E279.MirrorCS", {"start": v(39.37, -20.06) * mm, "end": v(39.37, -80.06) * mm});
            skSolve(sketch);
        }
        {
            var Q0;
            Q0=makeQuery(id+"F19.imprint","IMPRINT",FACE,{"disambiguationData":[TD([[makeQuery(id+"F19.imprint","IMPRINT",EDGE,{"derivedFrom":sQuery(id+"F19.wireOp",EDGE,"E275.bottom")}),-1.0]])]});
            var Q1;
            Q1=makeQuery(id+"F19.imprint","IMPRINT",FACE,{"disambiguationData":[TD([[makeQuery(id+"F19.imprint","IMPRINT",EDGE,{"derivedFrom":sQuery(id+"F19.wireOp",EDGE,"E276.MirrorCS")}),1.0]])]});
            extrude(context, id + "F20", {"entities" : qUnion([Q0, Q1]), "operationType" : NewBodyOperationType.REMOVE, "oppositeDirection" : true, "depth" : 25 * mm});
        }
        {
            var Q0;
            Q0=makeQuery(id+"F16.opPattern","COPY",BODY,{"derivedFrom":makeQuery(id+"F5.opExtrude","SWEPT_BODY",BODY,{"disambiguationData":[OSD([sQuery(id+"F0.wireOp",EDGE,"E0.bottom"),sQuery(id+"F0.wireOp",EDGE,"E0.left"),sQuery(id+"F0.wireOp",EDGE,"E8.0.2.0"),sQuery(id+"F0.wireOp",EDGE,"E8.0.2.1"),sQuery(id+"F0.wireOp",EDGE,"E8.0.2.2"),sQuery(id+"F0.wireOp",EDGE,"E8.0.2.3"),sQuery(id+"F0.wireOp",EDGE,"E8.0.3.0"),sQuery(id+"F0.wireOp",EDGE,"E8.0.3.1"),sQuery(id+"F0.wireOp",EDGE,"E8.0.3.2"),sQuery(id+"F0.wireOp",EDGE,"E8.0.3.3"),sQuery(id+"F0.wireOp",EDGE,"E8.0.4.0"),sQuery(id+"F0.wireOp",EDGE,"E8.0.4.1"),sQuery(id+"F0.wireOp",EDGE,"E8.0.4.2"),sQuery(id+"F0.wireOp",EDGE,"E8.0.4.3"),sQuery(id+"F0.wireOp",EDGE,"E9.MirrorCS"),sQuery(id+"F0.wireOp",EDGE,"E12.MirrorCS"),sQuery(id+"F0.wireOp",EDGE,"E13.MirrorCS"),sQuery(id+"F0.wireOp",EDGE,"E14.MirrorCS"),sQuery(id+"F0.wireOp",EDGE,"E15.MirrorCS"),sQuery(id+"F0.wireOp",EDGE,"E16.MirrorCS"),sQuery(id+"F0.wireOp",EDGE,"E27.MirrorCS"),sQuery(id+"F0.wireOp",EDGE,"E28.MirrorCS"),sQuery(id+"F0.wireOp",EDGE,"E29.MirrorCS"),sQuery(id+"F0.wireOp",EDGE,"E30.MirrorCS"),sQuery(id+"F0.wireOp",EDGE,"E31"),sQuery(id+"F0.wireOp",EDGE,"E46.MirrorCS"),sQuery(id+"F2.wireOp",EDGE,"E153"),sQuery(id+"F2.wireOp",EDGE,"E155"),sQuery(id+"F2.wireOp",EDGE,"E156")])]}),"instanceName":"1"});
            var Q1;
            Q1=makeQuery(id+"F11.opExtrude","SWEPT_BODY",BODY,{"disambiguationData":[OSD([sQuery(id+"F0.wireOp",EDGE,"E0.bottom"),sQuery(id+"F8.wireOp",EDGE,"E219"),sQuery(id+"F8.wireOp",EDGE,"E220"),sQuery(id+"F8.wireOp",EDGE,"E221"),sQuery(id+"F8.wireOp",EDGE,"E227"),sQuery(id+"F8.wireOp",EDGE,"E228")])]});
            deleteBodies(context, id + "F21", {"entities" : qUnion([Q0, Q1])});
        }
        {
            var Q0;
            Q0=makeQuery(id+"F5.opExtrude","SWEPT_FACE",FACE,{"disambiguationData":[OSD([sQuery(id+"F0.wireOp",EDGE,"E0.left")])]});
            var sketch = newSketch(context, id + "F22", { "sketchPlane" : qUnion([Q0])});
            skLineSegment(sketch, "E280.bottom", {"start": v(-86.5, 47) * mm, "end": v(-87.5, 47) * mm});
            skLineSegment(sketch, "E280.top", {"start": v(-86.5, 41) * mm, "end": v(-87.5, 41) * mm});
            skLineSegment(sketch, "E280.left", {"start": v(-86.5, 47) * mm, "end": v(-86.5, 41) * mm});
            skLineSegment(sketch, "E280.right", {"start": v(-87.5, 47) * mm, "end": v(-87.5, 41) * mm});
            skLineSegment(sketch, "E281.bottom", {"start": v(-86.5, 32) * mm, "end": v(-87.5, 32) * mm});
            skLineSegment(sketch, "E281.top", {"start": v(-86.5, 26) * mm, "end": v(-87.5, 26) * mm});
            skLineSegment(sketch, "E281.left", {"start": v(-86.5, 32) * mm, "end": v(-86.5, 26) * mm});
            skLineSegment(sketch, "E281.right", {"start": v(-87.5, 32) * mm, "end": v(-87.5, 26) * mm});
            skLineSegment(sketch, "E282.bottom", {"start": v(-86.5, 17) * mm, "end": v(-87.5, 17) * mm});
            skLineSegment(sketch, "E282.top", {"start": v(-86.5, 11) * mm, "end": v(-87.5, 11) * mm});
            skLineSegment(sketch, "E282.left", {"start": v(-86.5, 17) * mm, "end": v(-86.5, 11) * mm});
            skLineSegment(sketch, "E282.right", {"start": v(-87.5, 17) * mm, "end": v(-87.5, 11) * mm});
            skLineSegment(sketch, "E283.bottom", {"start": v(86.5, 47) * mm, "end": v(87.5, 47) * mm});
            skLineSegment(sketch, "E283.top", {"start": v(86.5, 41) * mm, "end": v(87.5, 41) * mm});
            skLineSegment(sketch, "E283.left", {"start": v(86.5, 47) * mm, "end": v(86.5, 41) * mm});
            skLineSegment(sketch, "E283.right", {"start": v(87.5, 47) * mm, "end": v(87.5, 41) * mm});
            skLineSegment(sketch, "E284.bottom", {"start": v(86.5, 32) * mm, "end": v(87.5, 32) * mm});
            skLineSegment(sketch, "E284.top", {"start": v(86.5, 26) * mm, "end": v(87.5, 26) * mm});
            skLineSegment(sketch, "E284.left", {"start": v(86.5, 32) * mm, "end": v(86.5, 26) * mm});
            skLineSegment(sketch, "E284.right", {"start": v(87.5, 32) * mm, "end": v(87.5, 26) * mm});
            skLineSegment(sketch, "E285.bottom", {"start": v(86.5, 17) * mm, "end": v(87.5, 17) * mm});
            skLineSegment(sketch, "E285.top", {"start": v(86.5, 11) * mm, "end": v(87.5, 11) * mm});
            skLineSegment(sketch, "E285.left", {"start": v(86.5, 17) * mm, "end": v(86.5, 11) * mm});
            skLineSegment(sketch, "E285.right", {"start": v(87.5, 17) * mm, "end": v(87.5, 11) * mm});
            skSolve(sketch);
        }
        {
            var Q0;
            Q0=makeQuery(id+"F22.imprint","IMPRINT",FACE,{"disambiguationData":[TD([[makeQuery(id+"F22.imprint","IMPRINT",EDGE,{"derivedFrom":sQuery(id+"F22.wireOp",EDGE,"E282.bottom")}),1.0]])]});
            var Q1;
            Q1=makeQuery(id+"F22.imprint","IMPRINT",FACE,{"disambiguationData":[TD([[makeQuery(id+"F22.imprint","IMPRINT",EDGE,{"derivedFrom":sQuery(id+"F22.wireOp",EDGE,"E281.bottom")}),1.0]])]});
            var Q2;
            Q2=makeQuery(id+"F22.imprint","IMPRINT",FACE,{"disambiguationData":[TD([[makeQuery(id+"F22.imprint","IMPRINT",EDGE,{"derivedFrom":sQuery(id+"F22.wireOp",EDGE,"E280.bottom")}),1.0]])]});
            var Q3;
            Q3=makeQuery(id+"F22.imprint","IMPRINT",FACE,{"disambiguationData":[TD([[makeQuery(id+"F22.imprint","IMPRINT",EDGE,{"derivedFrom":sQuery(id+"F22.wireOp",EDGE,"E283.bottom")}),-1.0]])]});
            var Q4;
            Q4=makeQuery(id+"F22.imprint","IMPRINT",FACE,{"disambiguationData":[TD([[makeQuery(id+"F22.imprint","IMPRINT",EDGE,{"derivedFrom":sQuery(id+"F22.wireOp",EDGE,"E284.bottom")}),-1.0]])]});
            var Q5;
            Q5=makeQuery(id+"F22.imprint","IMPRINT",FACE,{"disambiguationData":[TD([[makeQuery(id+"F22.imprint","IMPRINT",EDGE,{"derivedFrom":sQuery(id+"F22.wireOp",EDGE,"E285.bottom")}),-1.0]])]});
            extrude(context, id + "F23", {"entities" : qUnion([Q0, Q1, Q2, Q3, Q4, Q5]), "operationType" : NewBodyOperationType.REMOVE, "oppositeDirection" : true, "depth" : 25 * mm});
        }
        {
            var Q0;
            Q0=makeQuery(id+"F18.opPattern","COPY",FACE,{"derivedFrom":makeQuery(id+"F1.opExtrude","CAP_FACE",FACE,{"disambiguationData":[OSD([sQuery(id+"F0.wireOp",EDGE,"E0.bottom"),sQuery(id+"F0.wireOp",EDGE,"E0.left"),sQuery(id+"F0.wireOp",EDGE,"E0.right"),sQuery(id+"F0.wireOp",EDGE,"E4.bottom"),sQuery(id+"F0.wireOp",EDGE,"E4.left"),sQuery(id+"F0.wireOp",EDGE,"E4.right"),sQuery(id+"F0.wireOp",EDGE,"E5.MirrorCS"),sQuery(id+"F0.wireOp",EDGE,"E6.MirrorCS"),sQuery(id+"F0.wireOp",EDGE,"E7.MirrorCS"),sQuery(id+"F0.wireOp",EDGE,"E8.0.1.0"),sQuery(id+"F0.wireOp",EDGE,"E8.0.1.1"),sQuery(id+"F0.wireOp",EDGE,"E8.0.1.2"),sQuery(id+"F0.wireOp",EDGE,"E8.0.1.3"),sQuery(id+"F0.wireOp",EDGE,"E8.0.1.4"),sQuery(id+"F0.wireOp",EDGE,"E8.0.1.5"),sQuery(id+"F0.wireOp",EDGE,"E8.0.2.0"),sQuery(id+"F0.wireOp",EDGE,"E8.0.2.1"),sQuery(id+"F0.wireOp",EDGE,"E8.0.2.2"),sQuery(id+"F0.wireOp",EDGE,"E8.0.2.3"),sQuery(id+"F0.wireOp",EDGE,"E8.0.2.4"),sQuery(id+"F0.wireOp",EDGE,"E8.0.2.5"),sQuery(id+"F0.wireOp",EDGE,"E8.0.3.0"),sQuery(id+"F0.wireOp",EDGE,"E8.0.3.1"),sQuery(id+"F0.wireOp",EDGE,"E8.0.3.2"),sQuery(id+"F0.wireOp",EDGE,"E8.0.3.3"),sQuery(id+"F0.wireOp",EDGE,"E8.0.3.4"),sQuery(id+"F0.wireOp",EDGE,"E8.0.3.5"),sQuery(id+"F0.wireOp",EDGE,"E8.0.4.0"),sQuery(id+"F0.wireOp",EDGE,"E8.0.4.1"),sQuery(id+"F0.wireOp",EDGE,"E8.0.4.2"),sQuery(id+"F0.wireOp",EDGE,"E8.0.4.3"),sQuery(id+"F0.wireOp",EDGE,"E8.0.4.4"),sQuery(id+"F0.wireOp",EDGE,"E8.0.4.5"),sQuery(id+"F0.wireOp",EDGE,"E9.MirrorCS"),sQuery(id+"F0.wireOp",EDGE,"E10.MirrorCS"),sQuery(id+"F0.wireOp",EDGE,"E11.MirrorCS"),sQuery(id+"F0.wireOp",EDGE,"E12.MirrorCS"),sQuery(id+"F0.wireOp",EDGE,"E13.MirrorCS"),sQuery(id+"F0.wireOp",EDGE,"E14.MirrorCS"),sQuery(id+"F0.wireOp",EDGE,"E15.MirrorCS"),sQuery(id+"F0.wireOp",EDGE,"E16.MirrorCS"),sQuery(id+"F0.wireOp",EDGE,"E17.MirrorCS"),sQuery(id+"F0.wireOp",EDGE,"E18.MirrorCS"),sQuery(id+"F0.wireOp",EDGE,"E19.MirrorCS"),sQuery(id+"F0.wireOp",EDGE,"E20.MirrorCS"),sQuery(id+"F0.wireOp",EDGE,"E21.MirrorCS"),sQuery(id+"F0.wireOp",EDGE,"E22.MirrorCS"),sQuery(id+"F0.wireOp",EDGE,"E23.MirrorCS"),sQuery(id+"F0.wireOp",EDGE,"E24.MirrorCS"),sQuery(id+"F0.wireOp",EDGE,"E25.MirrorCS"),sQuery(id+"F0.wireOp",EDGE,"E26.MirrorCS"),sQuery(id+"F0.wireOp",EDGE,"E27.MirrorCS"),sQuery(id+"F0.wireOp",EDGE,"E28.MirrorCS"),sQuery(id+"F0.wireOp",EDGE,"E29.MirrorCS"),sQuery(id+"F0.wireOp",EDGE,"E30.MirrorCS"),sQuery(id+"F0.wireOp",EDGE,"E31"),sQuery(id+"F0.wireOp",EDGE,"E32.bottom"),sQuery(id+"F0.wireOp",EDGE,"E32.top"),sQuery(id+"F0.wireOp",EDGE,"E32.right"),sQuery(id+"F0.wireOp",EDGE,"E33.MirrorCS"),sQuery(id+"F0.wireOp",EDGE,"E34.MirrorCS"),sQuery(id+"F0.wireOp",EDGE,"E35.MirrorCS"),sQuery(id+"F0.wireOp",EDGE,"E36.1.0.0"),sQuery(id+"F0.wireOp",EDGE,"E36.1.0.1"),sQuery(id+"F0.wireOp",EDGE,"E36.1.0.2"),sQuery(id+"F0.wireOp",EDGE,"E36.1.0.3"),sQuery(id+"F0.wireOp",EDGE,"E36.1.0.4"),sQuery(id+"F0.wireOp",EDGE,"E36.1.0.5"),sQuery(id+"F0.wireOp",EDGE,"E36.2.0.0"),sQuery(id+"F0.wireOp",EDGE,"E36.2.0.1"),sQuery(id+"F0.wireOp",EDGE,"E36.2.0.2"),sQuery(id+"F0.wireOp",EDGE,"E36.2.0.3"),sQuery(id+"F0.wireOp",EDGE,"E36.2.0.4"),sQuery(id+"F0.wireOp",EDGE,"E36.2.0.5"),sQuery(id+"F0.wireOp",EDGE,"E36.3.0.0"),sQuery(id+"F0.wireOp",EDGE,"E36.3.0.1"),sQuery(id+"F0.wireOp",EDGE,"E36.3.0.2"),sQuery(id+"F0.wireOp",EDGE,"E36.3.0.3"),sQuery(id+"F0.wireOp",EDGE,"E36.3.0.4"),sQuery(id+"F0.wireOp",EDGE,"E36.3.0.5"),sQuery(id+"F0.wireOp",EDGE,"E37.MirrorCS"),sQuery(id+"F0.wireOp",EDGE,"E38.MirrorCS"),sQuery(id+"F0.wireOp",EDGE,"E39.MirrorCS"),sQuery(id+"F0.wireOp",EDGE,"E40.MirrorCS"),sQuery(id+"F0.wireOp",EDGE,"E41.MirrorCS"),sQuery(id+"F0.wireOp",EDGE,"E42.MirrorCS"),sQuery(id+"F0.wireOp",EDGE,"E43.MirrorCS"),sQuery(id+"F0.wireOp",EDGE,"E44.MirrorCS"),sQuery(id+"F0.wireOp",EDGE,"E45.MirrorCS"),sQuery(id+"F0.wireOp",EDGE,"E46.MirrorCS"),sQuery(id+"F0.wireOp",EDGE,"E47.MirrorCS"),sQuery(id+"F0.wireOp",EDGE,"E48.MirrorCS"),sQuery(id+"F0.wireOp",EDGE,"E49.MirrorCS"),sQuery(id+"F0.wireOp",EDGE,"E50.MirrorCS"),sQuery(id+"F0.wireOp",EDGE,"E51.MirrorCS"),sQuery(id+"F0.wireOp",EDGE,"E52.MirrorCS"),sQuery(id+"F0.wireOp",EDGE,"E53.MirrorCS"),sQuery(id+"F0.wireOp",EDGE,"E54.MirrorCS"),sQuery(id+"F0.wireOp",EDGE,"E55.MirrorCS"),sQuery(id+"F0.wireOp",EDGE,"E56.MirrorCS"),sQuery(id+"F0.wireOp",EDGE,"E57.MirrorCS"),sQuery(id+"F0.wireOp",EDGE,"E58.MirrorCS"),sQuery(id+"F0.wireOp",EDGE,"E59.MirrorCS"),sQuery(id+"F0.wireOp",EDGE,"E60.MirrorCS"),sQuery(id+"F0.wireOp",EDGE,"E61.MirrorCS"),sQuery(id+"F0.wireOp",EDGE,"E62.MirrorCS"),sQuery(id+"F0.wireOp",EDGE,"E63.MirrorCS"),sQuery(id+"F0.wireOp",EDGE,"E64.MirrorCS"),sQuery(id+"F0.wireOp",EDGE,"E65.MirrorCS"),sQuery(id+"F0.wireOp",EDGE,"E66.MirrorCS"),sQuery(id+"F0.wireOp",EDGE,"E67.MirrorCS"),sQuery(id+"F0.wireOp",EDGE,"E68.MirrorCS"),sQuery(id+"F0.wireOp",EDGE,"E69.MirrorCS"),sQuery(id+"F0.wireOp",EDGE,"E70.MirrorCS"),sQuery(id+"F0.wireOp",EDGE,"E71.MirrorCS"),sQuery(id+"F0.wireOp",EDGE,"E72.MirrorCS"),sQuery(id+"F0.wireOp",EDGE,"E73.MirrorCS"),sQuery(id+"F0.wireOp",EDGE,"E74.MirrorCS"),sQuery(id+"F0.wireOp",EDGE,"E75.MirrorCS"),sQuery(id+"F0.wireOp",EDGE,"E77.MirrorCS"),sQuery(id+"F0.wireOp",EDGE,"E78.MirrorCS"),sQuery(id+"F0.wireOp",EDGE,"E80.MirrorCS"),sQuery(id+"F0.wireOp",EDGE,"E81.MirrorCS"),sQuery(id+"F0.wireOp",EDGE,"E82.MirrorCS"),sQuery(id+"F0.wireOp",EDGE,"E83.MirrorCS"),sQuery(id+"F0.wireOp",EDGE,"E84.MirrorCS"),sQuery(id+"F0.wireOp",EDGE,"E85.MirrorCS"),sQuery(id+"F0.wireOp",EDGE,"E86.MirrorCS"),sQuery(id+"F0.wireOp",EDGE,"E87.MirrorCS"),sQuery(id+"F0.wireOp",EDGE,"E88.MirrorCS"),sQuery(id+"F0.wireOp",EDGE,"E89.MirrorCS"),sQuery(id+"F0.wireOp",EDGE,"E90.MirrorCS"),sQuery(id+"F0.wireOp",EDGE,"E91.MirrorCS"),sQuery(id+"F0.wireOp",EDGE,"E92.MirrorCS"),sQuery(id+"F0.wireOp",EDGE,"E93.MirrorCS"),sQuery(id+"F0.wireOp",EDGE,"E94.MirrorCS"),sQuery(id+"F0.wireOp",EDGE,"E95.MirrorCS"),sQuery(id+"F0.wireOp",EDGE,"E96.MirrorCS"),sQuery(id+"F0.wireOp",EDGE,"E97.MirrorCS"),sQuery(id+"F0.wireOp",EDGE,"E98.MirrorCS"),sQuery(id+"F0.wireOp",EDGE,"E99.MirrorCS"),sQuery(id+"F0.wireOp",EDGE,"E100.MirrorCS"),sQuery(id+"F0.wireOp",EDGE,"E101.MirrorCS"),sQuery(id+"F0.wireOp",EDGE,"E102.MirrorCS"),sQuery(id+"F0.wireOp",EDGE,"E103.MirrorCS"),sQuery(id+"F0.wireOp",EDGE,"E104.MirrorCS"),sQuery(id+"F0.wireOp",EDGE,"E105.MirrorCS"),sQuery(id+"F0.wireOp",EDGE,"E106.MirrorCS"),sQuery(id+"F0.wireOp",EDGE,"E107.MirrorCS"),sQuery(id+"F0.wireOp",EDGE,"E108"),sQuery(id+"F0.wireOp",EDGE,"E109"),sQuery(id+"F0.wireOp",EDGE,"E110.MirrorCS"),sQuery(id+"F0.wireOp",EDGE,"E111.MirrorCS"),sQuery(id+"F0.wireOp",EDGE,"E112.MirrorCS"),sQuery(id+"F0.wireOp",EDGE,"E113.MirrorCS"),sQuery(id+"F0.wireOp",EDGE,"E114.MirrorCS"),sQuery(id+"F0.wireOp",EDGE,"E115.MirrorCS"),sQuery(id+"F0.wireOp",EDGE,"E116.MirrorCS"),sQuery(id+"F0.wireOp",EDGE,"E117.MirrorCS"),sQuery(id+"F0.wireOp",EDGE,"E118.MirrorCS"),sQuery(id+"F0.wireOp",EDGE,"E119.MirrorCS"),sQuery(id+"F0.wireOp",EDGE,"E120.MirrorCS"),sQuery(id+"F0.wireOp",EDGE,"E121.MirrorCS"),sQuery(id+"F0.wireOp",EDGE,"E122.MirrorCS"),sQuery(id+"F0.wireOp",EDGE,"E123.MirrorCS"),sQuery(id+"F0.wireOp",EDGE,"E124.MirrorCS"),sQuery(id+"F0.wireOp",EDGE,"E125.MirrorCS"),sQuery(id+"F0.wireOp",EDGE,"E126.MirrorCS"),sQuery(id+"F0.wireOp",EDGE,"E127.MirrorCS"),sQuery(id+"F0.wireOp",EDGE,"E129.MirrorCS"),sQuery(id+"F0.wireOp",EDGE,"E130.MirrorCS"),sQuery(id+"F0.wireOp",EDGE,"E131.MirrorCS"),sQuery(id+"F0.wireOp",EDGE,"E132.MirrorCS"),sQuery(id+"F0.wireOp",EDGE,"E133.MirrorCS"),sQuery(id+"F0.wireOp",EDGE,"E134.MirrorCS"),sQuery(id+"F0.wireOp",EDGE,"E135.MirrorCS"),sQuery(id+"F0.wireOp",EDGE,"E136.MirrorCS"),sQuery(id+"F0.wireOp",EDGE,"E137.MirrorCS"),sQuery(id+"F0.wireOp",EDGE,"E138.MirrorCS"),sQuery(id+"F0.wireOp",EDGE,"E139.MirrorCS"),sQuery(id+"F0.wireOp",EDGE,"E140.MirrorCS"),sQuery(id+"F0.wireOp",EDGE,"E141.MirrorCS"),sQuery(id+"F0.wireOp",EDGE,"E142.MirrorCS"),sQuery(id+"F0.wireOp",EDGE,"E143.MirrorCS"),sQuery(id+"F0.wireOp",EDGE,"E144.MirrorCS"),sQuery(id+"F0.wireOp",EDGE,"E145.MirrorCS"),sQuery(id+"F0.wireOp",EDGE,"E146.MirrorCS"),sQuery(id+"F0.wireOp",EDGE,"E147.MirrorCS"),sQuery(id+"F0.wireOp",EDGE,"E148.MirrorCS"),sQuery(id+"F0.wireOp",EDGE,"E149.MirrorCS"),sQuery(id+"F0.wireOp",EDGE,"E150.MirrorCS"),sQuery(id+"F0.wireOp",EDGE,"E151")])],"isStart":true}),"instanceName":"1"});
            var sketch = newSketch(context, id + "F24", { "sketchPlane" : qUnion([Q0])});
            skLineSegment(sketch, "E286.bottom", {"start": v(-74, 83) * mm, "end": v(-75, 83) * mm});
            skLineSegment(sketch, "E286.top", {"start": v(-74, 77) * mm, "end": v(-75, 77) * mm});
            skLineSegment(sketch, "E286.left", {"start": v(-74, 83) * mm, "end": v(-74, 77) * mm});
            skLineSegment(sketch, "E286.right", {"start": v(-75, 83) * mm, "end": v(-75, 77) * mm});
            skLineSegment(sketch, "E287.bottom", {"start": v(-74, 63) * mm, "end": v(-75, 63) * mm});
            skLineSegment(sketch, "E287.top", {"start": v(-74, 57) * mm, "end": v(-75, 57) * mm});
            skLineSegment(sketch, "E287.left", {"start": v(-74, 63) * mm, "end": v(-74, 57) * mm});
            skLineSegment(sketch, "E287.right", {"start": v(-75, 63) * mm, "end": v(-75, 57) * mm});
            skLineSegment(sketch, "E288.bottom", {"start": v(-74, 43) * mm, "end": v(-75, 43) * mm});
            skLineSegment(sketch, "E288.top", {"start": v(-74, 37) * mm, "end": v(-75, 37) * mm});
            skLineSegment(sketch, "E288.left", {"start": v(-74, 43) * mm, "end": v(-74, 37) * mm});
            skLineSegment(sketch, "E288.right", {"start": v(-75, 43) * mm, "end": v(-75, 37) * mm});
            skLineSegment(sketch, "E289.bottom", {"start": v(-74, 23) * mm, "end": v(-75, 23) * mm});
            skLineSegment(sketch, "E289.top", {"start": v(-74, 17) * mm, "end": v(-75, 17) * mm});
            skLineSegment(sketch, "E289.left", {"start": v(-74, 23) * mm, "end": v(-74, 17) * mm});
            skLineSegment(sketch, "E289.right", {"start": v(-75, 23) * mm, "end": v(-75, 17) * mm});
            skLineSegment(sketch, "E290.bottom", {"start": v(-74, 3) * mm, "end": v(-75, 3) * mm});
            skLineSegment(sketch, "E290.top", {"start": v(-74, -3) * mm, "end": v(-75, -3) * mm});
            skLineSegment(sketch, "E290.left", {"start": v(-74, 3) * mm, "end": v(-74, -3) * mm});
            skLineSegment(sketch, "E290.right", {"start": v(-75, 3) * mm, "end": v(-75, -3) * mm});
            skLineSegment(sketch, "E291.bottom", {"start": v(-74, -17) * mm, "end": v(-75, -17) * mm});
            skLineSegment(sketch, "E291.top", {"start": v(-74, -23) * mm, "end": v(-75, -23) * mm});
            skLineSegment(sketch, "E291.left", {"start": v(-74, -17) * mm, "end": v(-74, -23) * mm});
            skLineSegment(sketch, "E291.right", {"start": v(-75, -17) * mm, "end": v(-75, -23) * mm});
            skLineSegment(sketch, "E292.bottom", {"start": v(-74, -37) * mm, "end": v(-75, -37) * mm});
            skLineSegment(sketch, "E292.top", {"start": v(-74, -43) * mm, "end": v(-75, -43) * mm});
            skLineSegment(sketch, "E292.left", {"start": v(-74, -37) * mm, "end": v(-74, -43) * mm});
            skLineSegment(sketch, "E292.right", {"start": v(-75, -37) * mm, "end": v(-75, -43) * mm});
            skLineSegment(sketch, "E293.bottom", {"start": v(-74, -57) * mm, "end": v(-75, -57) * mm});
            skLineSegment(sketch, "E293.top", {"start": v(-74, -63) * mm, "end": v(-75, -63) * mm});
            skLineSegment(sketch, "E293.left", {"start": v(-74, -57) * mm, "end": v(-74, -63) * mm});
            skLineSegment(sketch, "E293.right", {"start": v(-75, -57) * mm, "end": v(-75, -63) * mm});
            skLineSegment(sketch, "E294.bottom", {"start": v(-74, -77) * mm, "end": v(-75, -77) * mm});
            skLineSegment(sketch, "E294.top", {"start": v(-74, -83) * mm, "end": v(-75, -83) * mm});
            skLineSegment(sketch, "E294.left", {"start": v(-74, -77) * mm, "end": v(-74, -83) * mm});
            skLineSegment(sketch, "E294.right", {"start": v(-75, -77) * mm, "end": v(-75, -83) * mm});
            skLineSegment(sketch, "E295.bottom", {"start": v(-57, -86.5) * mm, "end": v(-63, -86.5) * mm});
            skLineSegment(sketch, "E295.top", {"start": v(-57, -87.5) * mm, "end": v(-63, -87.5) * mm});
            skLineSegment(sketch, "E295.left", {"start": v(-57, -86.5) * mm, "end": v(-57, -87.5) * mm});
            skLineSegment(sketch, "E295.right", {"start": v(-63, -86.5) * mm, "end": v(-63, -87.5) * mm});
            skLineSegment(sketch, "E296.bottom", {"start": v(-37, -86.5) * mm, "end": v(-43, -86.5) * mm});
            skLineSegment(sketch, "E296.top", {"start": v(-37, -87.5) * mm, "end": v(-43, -87.5) * mm});
            skLineSegment(sketch, "E296.left", {"start": v(-37, -86.5) * mm, "end": v(-37, -87.5) * mm});
            skLineSegment(sketch, "E296.right", {"start": v(-43, -86.5) * mm, "end": v(-43, -87.5) * mm});
            skLineSegment(sketch, "E297.bottom", {"start": v(-17, -86.5) * mm, "end": v(-23, -86.5) * mm});
            skLineSegment(sketch, "E297.top", {"start": v(-17, -87.5) * mm, "end": v(-23, -87.5) * mm});
            skLineSegment(sketch, "E297.left", {"start": v(-17, -86.5) * mm, "end": v(-17, -87.5) * mm});
            skLineSegment(sketch, "E297.right", {"start": v(-23, -86.5) * mm, "end": v(-23, -87.5) * mm});
            skLineSegment(sketch, "E298.bottom", {"start": v(3, -86.5) * mm, "end": v(-3, -86.5) * mm});
            skLineSegment(sketch, "E298.top", {"start": v(3, -87.5) * mm, "end": v(-3, -87.5) * mm});
            skLineSegment(sketch, "E298.left", {"start": v(3, -86.5) * mm, "end": v(3, -87.5) * mm});
            skLineSegment(sketch, "E298.right", {"start": v(-3, -86.5) * mm, "end": v(-3, -87.5) * mm});
            skLineSegment(sketch, "E299.bottom", {"start": v(-63, 86.5) * mm, "end": v(-57, 86.5) * mm});
            skLineSegment(sketch, "E299.top", {"start": v(-63, 87.5) * mm, "end": v(-57, 87.5) * mm});
            skLineSegment(sketch, "E299.left", {"start": v(-63, 86.5) * mm, "end": v(-63, 87.5) * mm});
            skLineSegment(sketch, "E299.right", {"start": v(-57, 86.5) * mm, "end": v(-57, 87.5) * mm});
            skLineSegment(sketch, "E300.bottom", {"start": v(-43, 86.5) * mm, "end": v(-37, 86.5) * mm});
            skLineSegment(sketch, "E300.top", {"start": v(-43, 87.5) * mm, "end": v(-37, 87.5) * mm});
            skLineSegment(sketch, "E300.left", {"start": v(-43, 86.5) * mm, "end": v(-43, 87.5) * mm});
            skLineSegment(sketch, "E300.right", {"start": v(-37, 86.5) * mm, "end": v(-37, 87.5) * mm});
            skLineSegment(sketch, "E301.bottom", {"start": v(-23, 86.5) * mm, "end": v(-17, 86.5) * mm});
            skLineSegment(sketch, "E301.top", {"start": v(-23, 87.5) * mm, "end": v(-17, 87.5) * mm});
            skLineSegment(sketch, "E301.left", {"start": v(-23, 86.5) * mm, "end": v(-23, 87.5) * mm});
            skLineSegment(sketch, "E301.right", {"start": v(-17, 86.5) * mm, "end": v(-17, 87.5) * mm});
            skLineSegment(sketch, "E302.bottom", {"start": v(-3, 86.5) * mm, "end": v(3, 86.5) * mm});
            skLineSegment(sketch, "E302.top", {"start": v(-3, 87.5) * mm, "end": v(3, 87.5) * mm});
            skLineSegment(sketch, "E302.left", {"start": v(-3, 86.5) * mm, "end": v(-3, 87.5) * mm});
            skLineSegment(sketch, "E302.right", {"start": v(3, 86.5) * mm, "end": v(3, 87.5) * mm});
            skLineSegment(sketch, "E303.bottom", {"start": v(17, 86.5) * mm, "end": v(23, 86.5) * mm});
            skLineSegment(sketch, "E303.top", {"start": v(17, 87.5) * mm, "end": v(23, 87.5) * mm});
            skLineSegment(sketch, "E303.left", {"start": v(17, 86.5) * mm, "end": v(17, 87.5) * mm});
            skLineSegment(sketch, "E303.right", {"start": v(23, 86.5) * mm, "end": v(23, 87.5) * mm});
            skLineSegment(sketch, "E304.bottom", {"start": v(37, 86.5) * mm, "end": v(43, 86.5) * mm});
            skLineSegment(sketch, "E304.top", {"start": v(37, 87.5) * mm, "end": v(43, 87.5) * mm});
            skLineSegment(sketch, "E304.left", {"start": v(37, 86.5) * mm, "end": v(37, 87.5) * mm});
            skLineSegment(sketch, "E304.right", {"start": v(43, 86.5) * mm, "end": v(43, 87.5) * mm});
            skLineSegment(sketch, "E305.bottom", {"start": v(57, 86.5) * mm, "end": v(63, 86.5) * mm});
            skLineSegment(sketch, "E305.top", {"start": v(57, 87.5) * mm, "end": v(63, 87.5) * mm});
            skLineSegment(sketch, "E305.left", {"start": v(57, 86.5) * mm, "end": v(57, 87.5) * mm});
            skLineSegment(sketch, "E305.right", {"start": v(63, 86.5) * mm, "end": v(63, 87.5) * mm});
            skLineSegment(sketch, "E306.bottom", {"start": v(74, 83) * mm, "end": v(75, 83) * mm});
            skLineSegment(sketch, "E306.top", {"start": v(74, 77) * mm, "end": v(75, 77) * mm});
            skLineSegment(sketch, "E306.left", {"start": v(74, 83) * mm, "end": v(74, 77) * mm});
            skLineSegment(sketch, "E306.right", {"start": v(75, 83) * mm, "end": v(75, 77) * mm});
            skLineSegment(sketch, "E307.bottom", {"start": v(74, 63) * mm, "end": v(75, 63) * mm});
            skLineSegment(sketch, "E307.top", {"start": v(74, 57) * mm, "end": v(75, 57) * mm});
            skLineSegment(sketch, "E307.left", {"start": v(74, 63) * mm, "end": v(74, 57) * mm});
            skLineSegment(sketch, "E307.right", {"start": v(75, 63) * mm, "end": v(75, 57) * mm});
            skLineSegment(sketch, "E308.bottom", {"start": v(74, 43) * mm, "end": v(75, 43) * mm});
            skLineSegment(sketch, "E308.top", {"start": v(74, 37) * mm, "end": v(75, 37) * mm});
            skLineSegment(sketch, "E308.left", {"start": v(74, 43) * mm, "end": v(74, 37) * mm});
            skLineSegment(sketch, "E308.right", {"start": v(75, 43) * mm, "end": v(75, 37) * mm});
            skLineSegment(sketch, "E309.bottom", {"start": v(74, 23) * mm, "end": v(75, 23) * mm});
            skLineSegment(sketch, "E309.top", {"start": v(74, 17) * mm, "end": v(75, 17) * mm});
            skLineSegment(sketch, "E309.left", {"start": v(74, 23) * mm, "end": v(74, 17) * mm});
            skLineSegment(sketch, "E309.right", {"start": v(75, 23) * mm, "end": v(75, 17) * mm});
            skLineSegment(sketch, "E310.bottom", {"start": v(74, 3) * mm, "end": v(75, 3) * mm});
            skLineSegment(sketch, "E310.top", {"start": v(74, -3) * mm, "end": v(75, -3) * mm});
            skLineSegment(sketch, "E310.left", {"start": v(74, 3) * mm, "end": v(74, -3) * mm});
            skLineSegment(sketch, "E310.right", {"start": v(75, 3) * mm, "end": v(75, -3) * mm});
            skLineSegment(sketch, "E311.bottom", {"start": v(74, -17) * mm, "end": v(75, -17) * mm});
            skLineSegment(sketch, "E311.top", {"start": v(74, -23) * mm, "end": v(75, -23) * mm});
            skLineSegment(sketch, "E311.left", {"start": v(74, -17) * mm, "end": v(74, -23) * mm});
            skLineSegment(sketch, "E311.right", {"start": v(75, -17) * mm, "end": v(75, -23) * mm});
            skLineSegment(sketch, "E312.bottom", {"start": v(74, -37) * mm, "end": v(75, -37) * mm});
            skLineSegment(sketch, "E312.top", {"start": v(74, -43) * mm, "end": v(75, -43) * mm});
            skLineSegment(sketch, "E312.left", {"start": v(74, -37) * mm, "end": v(74, -43) * mm});
            skLineSegment(sketch, "E312.right", {"start": v(75, -37) * mm, "end": v(75, -43) * mm});
            skLineSegment(sketch, "E313.bottom", {"start": v(74, -57) * mm, "end": v(75, -57) * mm});
            skLineSegment(sketch, "E313.top", {"start": v(74, -63) * mm, "end": v(75, -63) * mm});
            skLineSegment(sketch, "E313.left", {"start": v(74, -57) * mm, "end": v(74, -63) * mm});
            skLineSegment(sketch, "E313.right", {"start": v(75, -57) * mm, "end": v(75, -63) * mm});
            skLineSegment(sketch, "E314.bottom", {"start": v(74, -77) * mm, "end": v(75, -77) * mm});
            skLineSegment(sketch, "E314.top", {"start": v(74, -83) * mm, "end": v(75, -83) * mm});
            skLineSegment(sketch, "E314.left", {"start": v(74, -77) * mm, "end": v(74, -83) * mm});
            skLineSegment(sketch, "E314.right", {"start": v(75, -77) * mm, "end": v(75, -83) * mm});
            skLineSegment(sketch, "E315.bottom", {"start": v(17, -86.5) * mm, "end": v(23, -86.5) * mm});
            skLineSegment(sketch, "E315.top", {"start": v(17, -87.5) * mm, "end": v(23, -87.5) * mm});
            skLineSegment(sketch, "E315.left", {"start": v(17, -86.5) * mm, "end": v(17, -87.5) * mm});
            skLineSegment(sketch, "E315.right", {"start": v(23, -86.5) * mm, "end": v(23, -87.5) * mm});
            skLineSegment(sketch, "E316.bottom", {"start": v(37, -86.5) * mm, "end": v(43, -86.5) * mm});
            skLineSegment(sketch, "E316.top", {"start": v(37, -87.5) * mm, "end": v(43, -87.5) * mm});
            skLineSegment(sketch, "E316.left", {"start": v(37, -86.5) * mm, "end": v(37, -87.5) * mm});
            skLineSegment(sketch, "E316.right", {"start": v(43, -86.5) * mm, "end": v(43, -87.5) * mm});
            skLineSegment(sketch, "E317.bottom", {"start": v(57, -86.5) * mm, "end": v(63, -86.5) * mm});
            skLineSegment(sketch, "E317.top", {"start": v(57, -87.5) * mm, "end": v(63, -87.5) * mm});
            skLineSegment(sketch, "E317.left", {"start": v(57, -86.5) * mm, "end": v(57, -87.5) * mm});
            skLineSegment(sketch, "E317.right", {"start": v(63, -86.5) * mm, "end": v(63, -87.5) * mm});
            skSolve(sketch);
        }
        {
            var Q0;
            Q0=makeQuery(id+"F24.imprint","IMPRINT",FACE,{"disambiguationData":[TD([[makeQuery(id+"F24.imprint","IMPRINT",EDGE,{"derivedFrom":sQuery(id+"F24.wireOp",EDGE,"E297.bottom")}),-1.0]])]});
            var Q1;
            Q1=makeQuery(id+"F24.imprint","IMPRINT",FACE,{"disambiguationData":[TD([[makeQuery(id+"F24.imprint","IMPRINT",EDGE,{"derivedFrom":sQuery(id+"F24.wireOp",EDGE,"E298.bottom")}),-1.0]])]});
            var Q2;
            Q2=makeQuery(id+"F24.imprint","IMPRINT",FACE,{"disambiguationData":[TD([[makeQuery(id+"F24.imprint","IMPRINT",EDGE,{"derivedFrom":sQuery(id+"F24.wireOp",EDGE,"E296.bottom")}),-1.0]])]});
            var Q3;
            Q3=makeQuery(id+"F24.imprint","IMPRINT",FACE,{"disambiguationData":[TD([[makeQuery(id+"F24.imprint","IMPRINT",EDGE,{"derivedFrom":sQuery(id+"F24.wireOp",EDGE,"E295.bottom")}),-1.0]])]});
            var Q4;
            Q4=makeQuery(id+"F24.imprint","IMPRINT",FACE,{"disambiguationData":[TD([[makeQuery(id+"F24.imprint","IMPRINT",EDGE,{"derivedFrom":sQuery(id+"F24.wireOp",EDGE,"E294.bottom")}),1.0]])]});
            var Q5;
            Q5=makeQuery(id+"F24.imprint","IMPRINT",FACE,{"disambiguationData":[TD([[makeQuery(id+"F24.imprint","IMPRINT",EDGE,{"derivedFrom":sQuery(id+"F24.wireOp",EDGE,"E293.bottom")}),1.0]])]});
            var Q6;
            Q6=makeQuery(id+"F24.imprint","IMPRINT",FACE,{"disambiguationData":[TD([[makeQuery(id+"F24.imprint","IMPRINT",EDGE,{"derivedFrom":sQuery(id+"F24.wireOp",EDGE,"E292.bottom")}),1.0]])]});
            var Q7;
            Q7=makeQuery(id+"F24.imprint","IMPRINT",FACE,{"disambiguationData":[TD([[makeQuery(id+"F24.imprint","IMPRINT",EDGE,{"derivedFrom":sQuery(id+"F24.wireOp",EDGE,"E291.bottom")}),1.0]])]});
            var Q8;
            Q8=makeQuery(id+"F24.imprint","IMPRINT",FACE,{"disambiguationData":[TD([[makeQuery(id+"F24.imprint","IMPRINT",EDGE,{"derivedFrom":sQuery(id+"F24.wireOp",EDGE,"E290.bottom")}),1.0]])]});
            var Q9;
            Q9=makeQuery(id+"F24.imprint","IMPRINT",FACE,{"disambiguationData":[TD([[makeQuery(id+"F24.imprint","IMPRINT",EDGE,{"derivedFrom":sQuery(id+"F24.wireOp",EDGE,"E289.bottom")}),1.0]])]});
            var Q10;
            Q10=makeQuery(id+"F24.imprint","IMPRINT",FACE,{"disambiguationData":[TD([[makeQuery(id+"F24.imprint","IMPRINT",EDGE,{"derivedFrom":sQuery(id+"F24.wireOp",EDGE,"E288.bottom")}),1.0]])]});
            var Q11;
            Q11=makeQuery(id+"F24.imprint","IMPRINT",FACE,{"disambiguationData":[TD([[makeQuery(id+"F24.imprint","IMPRINT",EDGE,{"derivedFrom":sQuery(id+"F24.wireOp",EDGE,"E286.bottom")}),1.0]])]});
            var Q12;
            Q12=makeQuery(id+"F24.imprint","IMPRINT",FACE,{"disambiguationData":[TD([[makeQuery(id+"F24.imprint","IMPRINT",EDGE,{"derivedFrom":sQuery(id+"F24.wireOp",EDGE,"E287.bottom")}),1.0]])]});
            var Q13;
            Q13=makeQuery(id+"F24.imprint","IMPRINT",FACE,{"disambiguationData":[TD([[makeQuery(id+"F24.imprint","IMPRINT",EDGE,{"derivedFrom":sQuery(id+"F24.wireOp",EDGE,"E314.bottom")}),-1.0]])]});
            var Q14;
            Q14=makeQuery(id+"F24.imprint","IMPRINT",FACE,{"disambiguationData":[TD([[makeQuery(id+"F24.imprint","IMPRINT",EDGE,{"derivedFrom":sQuery(id+"F24.wireOp",EDGE,"E313.bottom")}),-1.0]])]});
            var Q15;
            Q15=makeQuery(id+"F24.imprint","IMPRINT",FACE,{"disambiguationData":[TD([[makeQuery(id+"F24.imprint","IMPRINT",EDGE,{"derivedFrom":sQuery(id+"F24.wireOp",EDGE,"E312.bottom")}),-1.0]])]});
            var Q16;
            Q16=makeQuery(id+"F24.imprint","IMPRINT",FACE,{"disambiguationData":[TD([[makeQuery(id+"F24.imprint","IMPRINT",EDGE,{"derivedFrom":sQuery(id+"F24.wireOp",EDGE,"E311.bottom")}),-1.0]])]});
            var Q17;
            Q17=makeQuery(id+"F24.imprint","IMPRINT",FACE,{"disambiguationData":[TD([[makeQuery(id+"F24.imprint","IMPRINT",EDGE,{"derivedFrom":sQuery(id+"F24.wireOp",EDGE,"E310.bottom")}),-1.0]])]});
            var Q18;
            Q18=makeQuery(id+"F24.imprint","IMPRINT",FACE,{"disambiguationData":[TD([[makeQuery(id+"F24.imprint","IMPRINT",EDGE,{"derivedFrom":sQuery(id+"F24.wireOp",EDGE,"E309.bottom")}),-1.0]])]});
            var Q19;
            Q19=makeQuery(id+"F24.imprint","IMPRINT",FACE,{"disambiguationData":[TD([[makeQuery(id+"F24.imprint","IMPRINT",EDGE,{"derivedFrom":sQuery(id+"F24.wireOp",EDGE,"E308.bottom")}),-1.0]])]});
            var Q20;
            Q20=makeQuery(id+"F24.imprint","IMPRINT",FACE,{"disambiguationData":[TD([[makeQuery(id+"F24.imprint","IMPRINT",EDGE,{"derivedFrom":sQuery(id+"F24.wireOp",EDGE,"E307.bottom")}),-1.0]])]});
            var Q21;
            Q21=makeQuery(id+"F24.imprint","IMPRINT",FACE,{"disambiguationData":[TD([[makeQuery(id+"F24.imprint","IMPRINT",EDGE,{"derivedFrom":sQuery(id+"F24.wireOp",EDGE,"E306.bottom")}),-1.0]])]});
            var Q22;
            Q22=makeQuery(id+"F24.imprint","IMPRINT",FACE,{"disambiguationData":[TD([[makeQuery(id+"F24.imprint","IMPRINT",EDGE,{"derivedFrom":sQuery(id+"F24.wireOp",EDGE,"E305.bottom")}),-1.0]])]});
            var Q23;
            Q23=makeQuery(id+"F24.imprint","IMPRINT",FACE,{"disambiguationData":[TD([[makeQuery(id+"F24.imprint","IMPRINT",EDGE,{"derivedFrom":sQuery(id+"F24.wireOp",EDGE,"E304.bottom")}),-1.0]])]});
            var Q24;
            Q24=makeQuery(id+"F24.imprint","IMPRINT",FACE,{"disambiguationData":[TD([[makeQuery(id+"F24.imprint","IMPRINT",EDGE,{"derivedFrom":sQuery(id+"F24.wireOp",EDGE,"E303.bottom")}),-1.0]])]});
            var Q25;
            Q25=makeQuery(id+"F24.imprint","IMPRINT",FACE,{"disambiguationData":[TD([[makeQuery(id+"F24.imprint","IMPRINT",EDGE,{"derivedFrom":sQuery(id+"F24.wireOp",EDGE,"E302.bottom")}),-1.0]])]});
            var Q26;
            Q26=makeQuery(id+"F24.imprint","IMPRINT",FACE,{"disambiguationData":[TD([[makeQuery(id+"F24.imprint","IMPRINT",EDGE,{"derivedFrom":sQuery(id+"F24.wireOp",EDGE,"E301.bottom")}),-1.0]])]});
            var Q27;
            Q27=makeQuery(id+"F24.imprint","IMPRINT",FACE,{"disambiguationData":[TD([[makeQuery(id+"F24.imprint","IMPRINT",EDGE,{"derivedFrom":sQuery(id+"F24.wireOp",EDGE,"E300.bottom")}),-1.0]])]});
            var Q28;
            Q28=makeQuery(id+"F24.imprint","IMPRINT",FACE,{"disambiguationData":[TD([[makeQuery(id+"F24.imprint","IMPRINT",EDGE,{"derivedFrom":sQuery(id+"F24.wireOp",EDGE,"E299.bottom")}),-1.0]])]});
            var Q29;
            Q29=makeQuery(id+"F24.imprint","IMPRINT",FACE,{"disambiguationData":[TD([[makeQuery(id+"F24.imprint","IMPRINT",EDGE,{"derivedFrom":sQuery(id+"F24.wireOp",EDGE,"E315.bottom")}),-1.0]])]});
            var Q30;
            Q30=makeQuery(id+"F24.imprint","IMPRINT",FACE,{"disambiguationData":[TD([[makeQuery(id+"F24.imprint","IMPRINT",EDGE,{"derivedFrom":sQuery(id+"F24.wireOp",EDGE,"E316.bottom")}),-1.0]])]});
            var Q31;
            Q31=makeQuery(id+"F24.imprint","IMPRINT",FACE,{"disambiguationData":[TD([[makeQuery(id+"F24.imprint","IMPRINT",EDGE,{"derivedFrom":sQuery(id+"F24.wireOp",EDGE,"E317.bottom")}),-1.0]])]});
            extrude(context, id + "F25", {"entities" : qUnion([Q0, Q1, Q2, Q3, Q4, Q5, Q6, Q7, Q8, Q9, Q10, Q11, Q12, Q13, Q14, Q15, Q16, Q17, Q18, Q19, Q20, Q21, Q22, Q23, Q24, Q25, Q26, Q27, Q28, Q29, Q30, Q31]), "operationType" : NewBodyOperationType.REMOVE, "oppositeDirection" : true, "depth" : 25 * mm});
        }
        {
            var Q0;
            Q0=makeQuery(id+"F1.opExtrude","CAP_FACE",FACE,{"disambiguationData":[OSD([sQuery(id+"F0.wireOp",EDGE,"E0.bottom"),sQuery(id+"F0.wireOp",EDGE,"E0.left"),sQuery(id+"F0.wireOp",EDGE,"E0.right"),sQuery(id+"F0.wireOp",EDGE,"E4.bottom"),sQuery(id+"F0.wireOp",EDGE,"E4.left"),sQuery(id+"F0.wireOp",EDGE,"E4.right"),sQuery(id+"F0.wireOp",EDGE,"E5.MirrorCS"),sQuery(id+"F0.wireOp",EDGE,"E6.MirrorCS"),sQuery(id+"F0.wireOp",EDGE,"E7.MirrorCS"),sQuery(id+"F0.wireOp",EDGE,"E8.0.1.0"),sQuery(id+"F0.wireOp",EDGE,"E8.0.1.1"),sQuery(id+"F0.wireOp",EDGE,"E8.0.1.2"),sQuery(id+"F0.wireOp",EDGE,"E8.0.1.3"),sQuery(id+"F0.wireOp",EDGE,"E8.0.1.4"),sQuery(id+"F0.wireOp",EDGE,"E8.0.1.5"),sQuery(id+"F0.wireOp",EDGE,"E8.0.2.0"),sQuery(id+"F0.wireOp",EDGE,"E8.0.2.1"),sQuery(id+"F0.wireOp",EDGE,"E8.0.2.2"),sQuery(id+"F0.wireOp",EDGE,"E8.0.2.3"),sQuery(id+"F0.wireOp",EDGE,"E8.0.2.4"),sQuery(id+"F0.wireOp",EDGE,"E8.0.2.5"),sQuery(id+"F0.wireOp",EDGE,"E8.0.3.0"),sQuery(id+"F0.wireOp",EDGE,"E8.0.3.1"),sQuery(id+"F0.wireOp",EDGE,"E8.0.3.2"),sQuery(id+"F0.wireOp",EDGE,"E8.0.3.3"),sQuery(id+"F0.wireOp",EDGE,"E8.0.3.4"),sQuery(id+"F0.wireOp",EDGE,"E8.0.3.5"),sQuery(id+"F0.wireOp",EDGE,"E8.0.4.0"),sQuery(id+"F0.wireOp",EDGE,"E8.0.4.1"),sQuery(id+"F0.wireOp",EDGE,"E8.0.4.2"),sQuery(id+"F0.wireOp",EDGE,"E8.0.4.3"),sQuery(id+"F0.wireOp",EDGE,"E8.0.4.4"),sQuery(id+"F0.wireOp",EDGE,"E8.0.4.5"),sQuery(id+"F0.wireOp",EDGE,"E9.MirrorCS"),sQuery(id+"F0.wireOp",EDGE,"E10.MirrorCS"),sQuery(id+"F0.wireOp",EDGE,"E11.MirrorCS"),sQuery(id+"F0.wireOp",EDGE,"E12.MirrorCS"),sQuery(id+"F0.wireOp",EDGE,"E13.MirrorCS"),sQuery(id+"F0.wireOp",EDGE,"E14.MirrorCS"),sQuery(id+"F0.wireOp",EDGE,"E15.MirrorCS"),sQuery(id+"F0.wireOp",EDGE,"E16.MirrorCS"),sQuery(id+"F0.wireOp",EDGE,"E17.MirrorCS"),sQuery(id+"F0.wireOp",EDGE,"E18.MirrorCS"),sQuery(id+"F0.wireOp",EDGE,"E19.MirrorCS"),sQuery(id+"F0.wireOp",EDGE,"E20.MirrorCS"),sQuery(id+"F0.wireOp",EDGE,"E21.MirrorCS"),sQuery(id+"F0.wireOp",EDGE,"E22.MirrorCS"),sQuery(id+"F0.wireOp",EDGE,"E23.MirrorCS"),sQuery(id+"F0.wireOp",EDGE,"E24.MirrorCS"),sQuery(id+"F0.wireOp",EDGE,"E25.MirrorCS"),sQuery(id+"F0.wireOp",EDGE,"E26.MirrorCS"),sQuery(id+"F0.wireOp",EDGE,"E27.MirrorCS"),sQuery(id+"F0.wireOp",EDGE,"E28.MirrorCS"),sQuery(id+"F0.wireOp",EDGE,"E29.MirrorCS"),sQuery(id+"F0.wireOp",EDGE,"E30.MirrorCS"),sQuery(id+"F0.wireOp",EDGE,"E31"),sQuery(id+"F0.wireOp",EDGE,"E32.bottom"),sQuery(id+"F0.wireOp",EDGE,"E32.top"),sQuery(id+"F0.wireOp",EDGE,"E32.right"),sQuery(id+"F0.wireOp",EDGE,"E33.MirrorCS"),sQuery(id+"F0.wireOp",EDGE,"E34.MirrorCS"),sQuery(id+"F0.wireOp",EDGE,"E35.MirrorCS"),sQuery(id+"F0.wireOp",EDGE,"E36.1.0.0"),sQuery(id+"F0.wireOp",EDGE,"E36.1.0.1"),sQuery(id+"F0.wireOp",EDGE,"E36.1.0.2"),sQuery(id+"F0.wireOp",EDGE,"E36.1.0.3"),sQuery(id+"F0.wireOp",EDGE,"E36.1.0.4"),sQuery(id+"F0.wireOp",EDGE,"E36.1.0.5"),sQuery(id+"F0.wireOp",EDGE,"E36.2.0.0"),sQuery(id+"F0.wireOp",EDGE,"E36.2.0.1"),sQuery(id+"F0.wireOp",EDGE,"E36.2.0.2"),sQuery(id+"F0.wireOp",EDGE,"E36.2.0.3"),sQuery(id+"F0.wireOp",EDGE,"E36.2.0.4"),sQuery(id+"F0.wireOp",EDGE,"E36.2.0.5"),sQuery(id+"F0.wireOp",EDGE,"E36.3.0.0"),sQuery(id+"F0.wireOp",EDGE,"E36.3.0.1"),sQuery(id+"F0.wireOp",EDGE,"E36.3.0.2"),sQuery(id+"F0.wireOp",EDGE,"E36.3.0.3"),sQuery(id+"F0.wireOp",EDGE,"E36.3.0.4"),sQuery(id+"F0.wireOp",EDGE,"E36.3.0.5"),sQuery(id+"F0.wireOp",EDGE,"E37.MirrorCS"),sQuery(id+"F0.wireOp",EDGE,"E38.MirrorCS"),sQuery(id+"F0.wireOp",EDGE,"E39.MirrorCS"),sQuery(id+"F0.wireOp",EDGE,"E40.MirrorCS"),sQuery(id+"F0.wireOp",EDGE,"E41.MirrorCS"),sQuery(id+"F0.wireOp",EDGE,"E42.MirrorCS"),sQuery(id+"F0.wireOp",EDGE,"E43.MirrorCS"),sQuery(id+"F0.wireOp",EDGE,"E44.MirrorCS"),sQuery(id+"F0.wireOp",EDGE,"E45.MirrorCS"),sQuery(id+"F0.wireOp",EDGE,"E46.MirrorCS"),sQuery(id+"F0.wireOp",EDGE,"E47.MirrorCS"),sQuery(id+"F0.wireOp",EDGE,"E48.MirrorCS"),sQuery(id+"F0.wireOp",EDGE,"E49.MirrorCS"),sQuery(id+"F0.wireOp",EDGE,"E50.MirrorCS"),sQuery(id+"F0.wireOp",EDGE,"E51.MirrorCS"),sQuery(id+"F0.wireOp",EDGE,"E52.MirrorCS"),sQuery(id+"F0.wireOp",EDGE,"E53.MirrorCS"),sQuery(id+"F0.wireOp",EDGE,"E54.MirrorCS"),sQuery(id+"F0.wireOp",EDGE,"E55.MirrorCS"),sQuery(id+"F0.wireOp",EDGE,"E56.MirrorCS"),sQuery(id+"F0.wireOp",EDGE,"E57.MirrorCS"),sQuery(id+"F0.wireOp",EDGE,"E58.MirrorCS"),sQuery(id+"F0.wireOp",EDGE,"E59.MirrorCS"),sQuery(id+"F0.wireOp",EDGE,"E60.MirrorCS"),sQuery(id+"F0.wireOp",EDGE,"E61.MirrorCS"),sQuery(id+"F0.wireOp",EDGE,"E62.MirrorCS"),sQuery(id+"F0.wireOp",EDGE,"E63.MirrorCS"),sQuery(id+"F0.wireOp",EDGE,"E64.MirrorCS"),sQuery(id+"F0.wireOp",EDGE,"E65.MirrorCS"),sQuery(id+"F0.wireOp",EDGE,"E66.MirrorCS"),sQuery(id+"F0.wireOp",EDGE,"E67.MirrorCS"),sQuery(id+"F0.wireOp",EDGE,"E68.MirrorCS"),sQuery(id+"F0.wireOp",EDGE,"E69.MirrorCS"),sQuery(id+"F0.wireOp",EDGE,"E70.MirrorCS"),sQuery(id+"F0.wireOp",EDGE,"E71.MirrorCS"),sQuery(id+"F0.wireOp",EDGE,"E72.MirrorCS"),sQuery(id+"F0.wireOp",EDGE,"E73.MirrorCS"),sQuery(id+"F0.wireOp",EDGE,"E74.MirrorCS"),sQuery(id+"F0.wireOp",EDGE,"E75.MirrorCS"),sQuery(id+"F0.wireOp",EDGE,"E77.MirrorCS"),sQuery(id+"F0.wireOp",EDGE,"E78.MirrorCS"),sQuery(id+"F0.wireOp",EDGE,"E80.MirrorCS"),sQuery(id+"F0.wireOp",EDGE,"E81.MirrorCS"),sQuery(id+"F0.wireOp",EDGE,"E82.MirrorCS"),sQuery(id+"F0.wireOp",EDGE,"E83.MirrorCS"),sQuery(id+"F0.wireOp",EDGE,"E84.MirrorCS"),sQuery(id+"F0.wireOp",EDGE,"E85.MirrorCS"),sQuery(id+"F0.wireOp",EDGE,"E86.MirrorCS"),sQuery(id+"F0.wireOp",EDGE,"E87.MirrorCS"),sQuery(id+"F0.wireOp",EDGE,"E88.MirrorCS"),sQuery(id+"F0.wireOp",EDGE,"E89.MirrorCS"),sQuery(id+"F0.wireOp",EDGE,"E90.MirrorCS"),sQuery(id+"F0.wireOp",EDGE,"E91.MirrorCS"),sQuery(id+"F0.wireOp",EDGE,"E92.MirrorCS"),sQuery(id+"F0.wireOp",EDGE,"E93.MirrorCS"),sQuery(id+"F0.wireOp",EDGE,"E94.MirrorCS"),sQuery(id+"F0.wireOp",EDGE,"E95.MirrorCS"),sQuery(id+"F0.wireOp",EDGE,"E96.MirrorCS"),sQuery(id+"F0.wireOp",EDGE,"E97.MirrorCS"),sQuery(id+"F0.wireOp",EDGE,"E98.MirrorCS"),sQuery(id+"F0.wireOp",EDGE,"E99.MirrorCS"),sQuery(id+"F0.wireOp",EDGE,"E100.MirrorCS"),sQuery(id+"F0.wireOp",EDGE,"E101.MirrorCS"),sQuery(id+"F0.wireOp",EDGE,"E102.MirrorCS"),sQuery(id+"F0.wireOp",EDGE,"E103.MirrorCS"),sQuery(id+"F0.wireOp",EDGE,"E104.MirrorCS"),sQuery(id+"F0.wireOp",EDGE,"E105.MirrorCS"),sQuery(id+"F0.wireOp",EDGE,"E106.MirrorCS"),sQuery(id+"F0.wireOp",EDGE,"E107.MirrorCS"),sQuery(id+"F0.wireOp",EDGE,"E108"),sQuery(id+"F0.wireOp",EDGE,"E109"),sQuery(id+"F0.wireOp",EDGE,"E110.MirrorCS"),sQuery(id+"F0.wireOp",EDGE,"E111.MirrorCS"),sQuery(id+"F0.wireOp",EDGE,"E112.MirrorCS"),sQuery(id+"F0.wireOp",EDGE,"E113.MirrorCS"),sQuery(id+"F0.wireOp",EDGE,"E114.MirrorCS"),sQuery(id+"F0.wireOp",EDGE,"E115.MirrorCS"),sQuery(id+"F0.wireOp",EDGE,"E116.MirrorCS"),sQuery(id+"F0.wireOp",EDGE,"E117.MirrorCS"),sQuery(id+"F0.wireOp",EDGE,"E118.MirrorCS"),sQuery(id+"F0.wireOp",EDGE,"E119.MirrorCS"),sQuery(id+"F0.wireOp",EDGE,"E120.MirrorCS"),sQuery(id+"F0.wireOp",EDGE,"E121.MirrorCS"),sQuery(id+"F0.wireOp",EDGE,"E122.MirrorCS"),sQuery(id+"F0.wireOp",EDGE,"E123.MirrorCS"),sQuery(id+"F0.wireOp",EDGE,"E124.MirrorCS"),sQuery(id+"F0.wireOp",EDGE,"E125.MirrorCS"),sQuery(id+"F0.wireOp",EDGE,"E126.MirrorCS"),sQuery(id+"F0.wireOp",EDGE,"E127.MirrorCS"),sQuery(id+"F0.wireOp",EDGE,"E129.MirrorCS"),sQuery(id+"F0.wireOp",EDGE,"E130.MirrorCS"),sQuery(id+"F0.wireOp",EDGE,"E131.MirrorCS"),sQuery(id+"F0.wireOp",EDGE,"E132.MirrorCS"),sQuery(id+"F0.wireOp",EDGE,"E133.MirrorCS"),sQuery(id+"F0.wireOp",EDGE,"E134.MirrorCS"),sQuery(id+"F0.wireOp",EDGE,"E135.MirrorCS"),sQuery(id+"F0.wireOp",EDGE,"E136.MirrorCS"),sQuery(id+"F0.wireOp",EDGE,"E137.MirrorCS"),sQuery(id+"F0.wireOp",EDGE,"E138.MirrorCS"),sQuery(id+"F0.wireOp",EDGE,"E139.MirrorCS"),sQuery(id+"F0.wireOp",EDGE,"E140.MirrorCS"),sQuery(id+"F0.wireOp",EDGE,"E141.MirrorCS"),sQuery(id+"F0.wireOp",EDGE,"E142.MirrorCS"),sQuery(id+"F0.wireOp",EDGE,"E143.MirrorCS"),sQuery(id+"F0.wireOp",EDGE,"E144.MirrorCS"),sQuery(id+"F0.wireOp",EDGE,"E145.MirrorCS"),sQuery(id+"F0.wireOp",EDGE,"E146.MirrorCS"),sQuery(id+"F0.wireOp",EDGE,"E147.MirrorCS"),sQuery(id+"F0.wireOp",EDGE,"E148.MirrorCS"),sQuery(id+"F0.wireOp",EDGE,"E149.MirrorCS"),sQuery(id+"F0.wireOp",EDGE,"E150.MirrorCS"),sQuery(id+"F0.wireOp",EDGE,"E151")])],"isStart":false});
            var sketch = newSketch(context, id + "F26", { "sketchPlane" : qUnion([Q0])});
            skLineSegment(sketch, "E318.bottom", {"start": v(-23, -87.5) * mm, "end": v(-17, -87.5) * mm});
            skLineSegment(sketch, "E318.top", {"start": v(-23, -86.5) * mm, "end": v(-17, -86.5) * mm});
            skLineSegment(sketch, "E318.left", {"start": v(-23, -87.5) * mm, "end": v(-23, -86.5) * mm});
            skLineSegment(sketch, "E318.right", {"start": v(-17, -87.5) * mm, "end": v(-17, -86.5) * mm});
            skLineSegment(sketch, "E319.bottom", {"start": v(-43, -86.5) * mm, "end": v(-37, -86.5) * mm});
            skLineSegment(sketch, "E319.top", {"start": v(-43, -87.5) * mm, "end": v(-37, -87.5) * mm});
            skLineSegment(sketch, "E319.left", {"start": v(-43, -86.5) * mm, "end": v(-43, -87.5) * mm});
            skLineSegment(sketch, "E319.right", {"start": v(-37, -86.5) * mm, "end": v(-37, -87.5) * mm});
            skLineSegment(sketch, "E320.bottom", {"start": v(-63, -86.5) * mm, "end": v(-57, -86.5) * mm});
            skLineSegment(sketch, "E320.top", {"start": v(-63, -87.5) * mm, "end": v(-57, -87.5) * mm});
            skLineSegment(sketch, "E320.left", {"start": v(-63, -86.5) * mm, "end": v(-63, -87.5) * mm});
            skLineSegment(sketch, "E320.right", {"start": v(-57, -86.5) * mm, "end": v(-57, -87.5) * mm});
            skLineSegment(sketch, "E321.MirrorCS", {"start": v(63, -86.5) * mm, "end": v(57, -86.5) * mm});
            skLineSegment(sketch, "E322.MirrorCS", {"start": v(63, -86.5) * mm, "end": v(63, -87.5) * mm});
            skLineSegment(sketch, "E323.MirrorCS", {"start": v(63, -87.5) * mm, "end": v(57, -87.5) * mm});
            skLineSegment(sketch, "E324.MirrorCS", {"start": v(57, -86.5) * mm, "end": v(57, -87.5) * mm});
            skLineSegment(sketch, "E325.MirrorCS", {"start": v(43, -86.5) * mm, "end": v(37, -86.5) * mm});
            skLineSegment(sketch, "E326.MirrorCS", {"start": v(43, -86.5) * mm, "end": v(43, -87.5) * mm});
            skLineSegment(sketch, "E327.MirrorCS", {"start": v(43, -87.5) * mm, "end": v(37, -87.5) * mm});
            skLineSegment(sketch, "E328.MirrorCS", {"start": v(37, -86.5) * mm, "end": v(37, -87.5) * mm});
            skLineSegment(sketch, "E329.MirrorCS", {"start": v(23, -86.5) * mm, "end": v(17, -86.5) * mm});
            skLineSegment(sketch, "E330.MirrorCS", {"start": v(23, -87.5) * mm, "end": v(23, -86.5) * mm});
            skLineSegment(sketch, "E331.MirrorCS", {"start": v(23, -87.5) * mm, "end": v(17, -87.5) * mm});
            skLineSegment(sketch, "E332.MirrorCS", {"start": v(17, -87.5) * mm, "end": v(17, -86.5) * mm});
            skLineSegment(sketch, "E333.bottom", {"start": v(-3, -86.5) * mm, "end": v(3, -86.5) * mm});
            skLineSegment(sketch, "E333.top", {"start": v(-3, -87.5) * mm, "end": v(3, -87.5) * mm});
            skLineSegment(sketch, "E333.left", {"start": v(-3, -86.5) * mm, "end": v(-3, -87.5) * mm});
            skLineSegment(sketch, "E333.right", {"start": v(3, -86.5) * mm, "end": v(3, -87.5) * mm});
            skLineSegment(sketch, "E334.1.0.0", {"start": v(17, -86.5) * mm, "end": v(23, -86.5) * mm});
            skLineSegment(sketch, "E334.1.0.1", {"start": v(17, -86.5) * mm, "end": v(17, -87.5) * mm});
            skLineSegment(sketch, "E334.1.0.2", {"start": v(17, -87.5) * mm, "end": v(23, -87.5) * mm});
            skLineSegment(sketch, "E334.1.0.3", {"start": v(23, -86.5) * mm, "end": v(23, -87.5) * mm});
            skLineSegment(sketch, "E334.2.0.0", {"start": v(37, -86.5) * mm, "end": v(43, -86.5) * mm});
            skLineSegment(sketch, "E334.2.0.2", {"start": v(37, -87.5) * mm, "end": v(43, -87.5) * mm});
            skLineSegment(sketch, "E334.3.0.0", {"start": v(57, -86.5) * mm, "end": v(63, -86.5) * mm});
            skLineSegment(sketch, "E334.3.0.2", {"start": v(57, -87.5) * mm, "end": v(63, -87.5) * mm});
            skLineSegment(sketch, "E334.direction1", {"start": v(-3, -86.5) * mm, "end": v(17, -86.5) * mm, "construction": true});
            skLineSegment(sketch, "E335.MirrorCS", {"start": v(-63, 86.5) * mm, "end": v(-57, 86.5) * mm});
            skLineSegment(sketch, "E336.MirrorCS", {"start": v(-63, 86.5) * mm, "end": v(-63, 87.5) * mm});
            skLineSegment(sketch, "E337.MirrorCS", {"start": v(-63, 87.5) * mm, "end": v(-57, 87.5) * mm});
            skLineSegment(sketch, "E338.MirrorCS", {"start": v(-57, 86.5) * mm, "end": v(-57, 87.5) * mm});
            skLineSegment(sketch, "E339.MirrorCS", {"start": v(-43, 86.5) * mm, "end": v(-37, 86.5) * mm});
            skLineSegment(sketch, "E340.MirrorCS", {"start": v(-43, 86.5) * mm, "end": v(-43, 87.5) * mm});
            skLineSegment(sketch, "E341.MirrorCS", {"start": v(-43, 87.5) * mm, "end": v(-37, 87.5) * mm});
            skLineSegment(sketch, "E342.MirrorCS", {"start": v(-37, 86.5) * mm, "end": v(-37, 87.5) * mm});
            skLineSegment(sketch, "E343.MirrorCS", {"start": v(-23, 86.5) * mm, "end": v(-17, 86.5) * mm});
            skLineSegment(sketch, "E344.MirrorCS", {"start": v(-23, 87.5) * mm, "end": v(-23, 86.5) * mm});
            skLineSegment(sketch, "E345.MirrorCS", {"start": v(-23, 87.5) * mm, "end": v(-17, 87.5) * mm});
            skLineSegment(sketch, "E346.MirrorCS", {"start": v(-17, 87.5) * mm, "end": v(-17, 86.5) * mm});
            skLineSegment(sketch, "E347.MirrorCS", {"start": v(-3, 86.5) * mm, "end": v(17, 86.5) * mm, "construction": true});
            skLineSegment(sketch, "E348.MirrorCS", {"start": v(-3, 86.5) * mm, "end": v(-3, 87.5) * mm});
            skLineSegment(sketch, "E349.MirrorCS", {"start": v(-3, 87.5) * mm, "end": v(3, 87.5) * mm});
            skLineSegment(sketch, "E350.MirrorCS", {"start": v(3, 86.5) * mm, "end": v(3, 87.5) * mm});
            skLineSegment(sketch, "E351.MirrorCS", {"start": v(17, 86.5) * mm, "end": v(23, 86.5) * mm});
            skLineSegment(sketch, "E352.MirrorCS", {"start": v(17, 87.5) * mm, "end": v(17, 86.5) * mm});
            skLineSegment(sketch, "E353.MirrorCS", {"start": v(23, 87.5) * mm, "end": v(17, 87.5) * mm});
            skLineSegment(sketch, "E354.MirrorCS", {"start": v(23, 86.5) * mm, "end": v(23, 87.5) * mm});
            skLineSegment(sketch, "E355.MirrorCS", {"start": v(43, 86.5) * mm, "end": v(37, 86.5) * mm});
            skLineSegment(sketch, "E356.MirrorCS", {"start": v(37, 86.5) * mm, "end": v(37, 87.5) * mm});
            skLineSegment(sketch, "E357.MirrorCS", {"start": v(43, 86.5) * mm, "end": v(43, 87.5) * mm});
            skLineSegment(sketch, "E358.MirrorCS", {"start": v(43, 87.5) * mm, "end": v(37, 87.5) * mm});
            skLineSegment(sketch, "E359.MirrorCS", {"start": v(57, 86.5) * mm, "end": v(63, 86.5) * mm});
            skLineSegment(sketch, "E360.MirrorCS", {"start": v(63, 86.5) * mm, "end": v(63, 87.5) * mm});
            skLineSegment(sketch, "E361.MirrorCS", {"start": v(57, 87.5) * mm, "end": v(63, 87.5) * mm});
            skLineSegment(sketch, "E362.MirrorCS", {"start": v(57, 86.5) * mm, "end": v(57, 87.5) * mm});
            skLineSegment(sketch, "E363", {"start": v(3, 86.5) * mm, "end": v(-3, 86.5) * mm});
            skLineSegment(sketch, "E364.bottom", {"start": v(-74, 83) * mm, "end": v(-75, 83) * mm});
            skLineSegment(sketch, "E364.top", {"start": v(-74, 77) * mm, "end": v(-75, 77) * mm});
            skLineSegment(sketch, "E364.left", {"start": v(-74, 83) * mm, "end": v(-74, 77) * mm});
            skLineSegment(sketch, "E364.right", {"start": v(-75, 83) * mm, "end": v(-75, 77) * mm});
            skLineSegment(sketch, "E365.bottom", {"start": v(-74, 63) * mm, "end": v(-75, 63) * mm});
            skLineSegment(sketch, "E365.top", {"start": v(-74, 57) * mm, "end": v(-75, 57) * mm});
            skLineSegment(sketch, "E365.left", {"start": v(-74, 63) * mm, "end": v(-74, 57) * mm});
            skLineSegment(sketch, "E365.right", {"start": v(-75, 63) * mm, "end": v(-75, 57) * mm});
            skLineSegment(sketch, "E366.bottom", {"start": v(-74, 43) * mm, "end": v(-75, 43) * mm});
            skLineSegment(sketch, "E366.top", {"start": v(-74, 37) * mm, "end": v(-75, 37) * mm});
            skLineSegment(sketch, "E366.left", {"start": v(-74, 43) * mm, "end": v(-74, 37) * mm});
            skLineSegment(sketch, "E366.right", {"start": v(-75, 43) * mm, "end": v(-75, 37) * mm});
            skLineSegment(sketch, "E367.bottom", {"start": v(-74, 23) * mm, "end": v(-75, 23) * mm});
            skLineSegment(sketch, "E367.top", {"start": v(-74, 17) * mm, "end": v(-75, 17) * mm});
            skLineSegment(sketch, "E367.left", {"start": v(-74, 23) * mm, "end": v(-74, 17) * mm});
            skLineSegment(sketch, "E367.right", {"start": v(-75, 23) * mm, "end": v(-75, 17) * mm});
            skLineSegment(sketch, "E368.bottom", {"start": v(-74, 3) * mm, "end": v(-75, 3) * mm});
            skLineSegment(sketch, "E368.top", {"start": v(-74, -3) * mm, "end": v(-75, -3) * mm});
            skLineSegment(sketch, "E368.left", {"start": v(-74, 3) * mm, "end": v(-74, -3) * mm});
            skLineSegment(sketch, "E368.right", {"start": v(-75, 3) * mm, "end": v(-75, -3) * mm});
            skLineSegment(sketch, "E369.bottom", {"start": v(-74, -17) * mm, "end": v(-75, -17) * mm});
            skLineSegment(sketch, "E369.top", {"start": v(-74, -23) * mm, "end": v(-75, -23) * mm});
            skLineSegment(sketch, "E369.left", {"start": v(-74, -17) * mm, "end": v(-74, -23) * mm});
            skLineSegment(sketch, "E369.right", {"start": v(-75, -17) * mm, "end": v(-75, -23) * mm});
            skLineSegment(sketch, "E370.bottom", {"start": v(-74, -37) * mm, "end": v(-75, -37) * mm});
            skLineSegment(sketch, "E370.top", {"start": v(-74, -43) * mm, "end": v(-75, -43) * mm});
            skLineSegment(sketch, "E370.left", {"start": v(-74, -37) * mm, "end": v(-74, -43) * mm});
            skLineSegment(sketch, "E370.right", {"start": v(-75, -37) * mm, "end": v(-75, -43) * mm});
            skLineSegment(sketch, "E371.bottom", {"start": v(-74, -57) * mm, "end": v(-75, -57) * mm});
            skLineSegment(sketch, "E371.top", {"start": v(-74, -63) * mm, "end": v(-75, -63) * mm});
            skLineSegment(sketch, "E371.left", {"start": v(-74, -57) * mm, "end": v(-74, -63) * mm});
            skLineSegment(sketch, "E371.right", {"start": v(-75, -57) * mm, "end": v(-75, -63) * mm});
            skLineSegment(sketch, "E372.bottom", {"start": v(-74, -77) * mm, "end": v(-75, -77) * mm});
            skLineSegment(sketch, "E372.top", {"start": v(-74, -83) * mm, "end": v(-75, -83) * mm});
            skLineSegment(sketch, "E372.left", {"start": v(-74, -77) * mm, "end": v(-74, -83) * mm});
            skLineSegment(sketch, "E372.right", {"start": v(-75, -77) * mm, "end": v(-75, -83) * mm});
            skLineSegment(sketch, "E373.MirrorCS", {"start": v(74, 83) * mm, "end": v(74, 77) * mm});
            skLineSegment(sketch, "E374.MirrorCS", {"start": v(74, 83) * mm, "end": v(75, 83) * mm});
            skLineSegment(sketch, "E375.MirrorCS", {"start": v(75, 83) * mm, "end": v(75, 77) * mm});
            skLineSegment(sketch, "E376.MirrorCS", {"start": v(74, 77) * mm, "end": v(75, 77) * mm});
            skLineSegment(sketch, "E377.MirrorCS", {"start": v(74, 63) * mm, "end": v(74, 57) * mm});
            skLineSegment(sketch, "E378.MirrorCS", {"start": v(74, 63) * mm, "end": v(75, 63) * mm});
            skLineSegment(sketch, "E379.MirrorCS", {"start": v(75, 63) * mm, "end": v(75, 57) * mm});
            skLineSegment(sketch, "E380.MirrorCS", {"start": v(74, 57) * mm, "end": v(75, 57) * mm});
            skLineSegment(sketch, "E381.MirrorCS", {"start": v(74, 43) * mm, "end": v(74, 37) * mm});
            skLineSegment(sketch, "E382.MirrorCS", {"start": v(74, 43) * mm, "end": v(75, 43) * mm});
            skLineSegment(sketch, "E383.MirrorCS", {"start": v(75, 43) * mm, "end": v(75, 37) * mm});
            skLineSegment(sketch, "E384.MirrorCS", {"start": v(74, 37) * mm, "end": v(75, 37) * mm});
            skLineSegment(sketch, "E385.MirrorCS", {"start": v(74, 23) * mm, "end": v(74, 17) * mm});
            skLineSegment(sketch, "E386.MirrorCS", {"start": v(74, 23) * mm, "end": v(75, 23) * mm});
            skLineSegment(sketch, "E387.MirrorCS", {"start": v(75, 23) * mm, "end": v(75, 17) * mm});
            skLineSegment(sketch, "E388.MirrorCS", {"start": v(74, 17) * mm, "end": v(75, 17) * mm});
            skLineSegment(sketch, "E389.MirrorCS", {"start": v(74, 3) * mm, "end": v(74, -3) * mm});
            skLineSegment(sketch, "E390.MirrorCS", {"start": v(74, 3) * mm, "end": v(75, 3) * mm});
            skLineSegment(sketch, "E391.MirrorCS", {"start": v(75, 3) * mm, "end": v(75, -3) * mm});
            skLineSegment(sketch, "E392.MirrorCS", {"start": v(74, -3) * mm, "end": v(75, -3) * mm});
            skLineSegment(sketch, "E393.MirrorCS", {"start": v(74, -17) * mm, "end": v(74, -23) * mm});
            skLineSegment(sketch, "E394.MirrorCS", {"start": v(74, -17) * mm, "end": v(75, -17) * mm});
            skLineSegment(sketch, "E395.MirrorCS", {"start": v(75, -17) * mm, "end": v(75, -23) * mm});
            skLineSegment(sketch, "E396.MirrorCS", {"start": v(74, -23) * mm, "end": v(75, -23) * mm});
            skLineSegment(sketch, "E397.MirrorCS", {"start": v(74, -37) * mm, "end": v(74, -43) * mm});
            skLineSegment(sketch, "E398.MirrorCS", {"start": v(74, -37) * mm, "end": v(75, -37) * mm});
            skLineSegment(sketch, "E399.MirrorCS", {"start": v(75, -37) * mm, "end": v(75, -43) * mm});
            skLineSegment(sketch, "E400.MirrorCS", {"start": v(74, -43) * mm, "end": v(75, -43) * mm});
            skLineSegment(sketch, "E401.MirrorCS", {"start": v(74, -57) * mm, "end": v(74, -63) * mm});
            skLineSegment(sketch, "E402.MirrorCS", {"start": v(74, -57) * mm, "end": v(75, -57) * mm});
            skLineSegment(sketch, "E403.MirrorCS", {"start": v(75, -57) * mm, "end": v(75, -63) * mm});
            skLineSegment(sketch, "E404.MirrorCS", {"start": v(74, -63) * mm, "end": v(75, -63) * mm});
            skLineSegment(sketch, "E405.MirrorCS", {"start": v(74, -77) * mm, "end": v(74, -83) * mm});
            skLineSegment(sketch, "E406.MirrorCS", {"start": v(74, -77) * mm, "end": v(75, -77) * mm});
            skLineSegment(sketch, "E407.MirrorCS", {"start": v(75, -77) * mm, "end": v(75, -83) * mm});
            skLineSegment(sketch, "E408.MirrorCS", {"start": v(74, -83) * mm, "end": v(75, -83) * mm});
            skSolve(sketch);
        }
        {
            var Q0;
            Q0=makeQuery(id+"F26.imprint","IMPRINT",FACE,{"disambiguationData":[TD([[makeQuery(id+"F26.imprint","IMPRINT",EDGE,{"derivedFrom":sQuery(id+"F26.wireOp",EDGE,"E335.MirrorCS")}),-1.0]])]});
            var Q1;
            Q1=makeQuery(id+"F26.imprint","IMPRINT",FACE,{"disambiguationData":[TD([[makeQuery(id+"F26.imprint","IMPRINT",EDGE,{"derivedFrom":sQuery(id+"F26.wireOp",EDGE,"E339.MirrorCS")}),-1.0]])]});
            var Q2;
            Q2=makeQuery(id+"F26.imprint","IMPRINT",FACE,{"disambiguationData":[TD([[makeQuery(id+"F26.imprint","IMPRINT",EDGE,{"derivedFrom":sQuery(id+"F26.wireOp",EDGE,"E343.MirrorCS")}),-1.0]])]});
            var Q3;
            {var subQ2=sQuery(id+"F26.wireOp",EDGE,"E348.MirrorCS");Q3=makeQuery(id+"F26.imprint","IMPRINT",FACE,{"disambiguationData":[TD([[makeQuery(id+"F26.imprint","IMPRINT",EDGE,{"derivedFrom":subQ2}),-1.0]])]});}
            var Q4;
            {var subQ1=sQuery(id+"F26.wireOp",EDGE,"E352.MirrorCS");Q4=makeQuery(id+"F26.imprint","IMPRINT",FACE,{"disambiguationData":[TD([[makeQuery(id+"F26.imprint","IMPRINT",EDGE,{"derivedFrom":subQ1}),1.0]])]});}
            var Q5;
            Q5=makeQuery(id+"F26.imprint","IMPRINT",FACE,{"disambiguationData":[TD([[makeQuery(id+"F26.imprint","IMPRINT",EDGE,{"derivedFrom":sQuery(id+"F26.wireOp",EDGE,"E355.MirrorCS")}),-1.0]])]});
            var Q6;
            {var subQ0=sQuery(id+"F26.wireOp",EDGE,"E360.MirrorCS");Q6=makeQuery(id+"F26.imprint","IMPRINT",FACE,{"disambiguationData":[TD([[makeQuery(id+"F26.imprint","IMPRINT",EDGE,{"derivedFrom":subQ0}),1.0]])]});}
            var Q7;
            Q7=makeQuery(id+"F26.imprint","IMPRINT",FACE,{"disambiguationData":[TD([[makeQuery(id+"F26.imprint","IMPRINT",EDGE,{"derivedFrom":sQuery(id+"F26.wireOp",EDGE,"E373.MirrorCS")}),-1.0]])]});
            var Q8;
            Q8=makeQuery(id+"F26.imprint","IMPRINT",FACE,{"disambiguationData":[TD([[makeQuery(id+"F26.imprint","IMPRINT",EDGE,{"derivedFrom":sQuery(id+"F26.wireOp",EDGE,"E377.MirrorCS")}),-1.0]])]});
            var Q9;
            Q9=makeQuery(id+"F26.imprint","IMPRINT",FACE,{"disambiguationData":[TD([[makeQuery(id+"F26.imprint","IMPRINT",EDGE,{"derivedFrom":sQuery(id+"F26.wireOp",EDGE,"E381.MirrorCS")}),-1.0]])]});
            var Q10;
            Q10=makeQuery(id+"F26.imprint","IMPRINT",FACE,{"disambiguationData":[TD([[makeQuery(id+"F26.imprint","IMPRINT",EDGE,{"derivedFrom":sQuery(id+"F26.wireOp",EDGE,"E385.MirrorCS")}),1.0]])]});
            var Q11;
            Q11=makeQuery(id+"F26.imprint","IMPRINT",FACE,{"disambiguationData":[TD([[makeQuery(id+"F26.imprint","IMPRINT",EDGE,{"derivedFrom":sQuery(id+"F26.wireOp",EDGE,"E389.MirrorCS")}),1.0]])]});
            var Q12;
            Q12=makeQuery(id+"F26.imprint","IMPRINT",FACE,{"disambiguationData":[TD([[makeQuery(id+"F26.imprint","IMPRINT",EDGE,{"derivedFrom":sQuery(id+"F26.wireOp",EDGE,"E393.MirrorCS")}),-1.0]])]});
            var Q13;
            Q13=makeQuery(id+"F26.imprint","IMPRINT",FACE,{"disambiguationData":[TD([[makeQuery(id+"F26.imprint","IMPRINT",EDGE,{"derivedFrom":sQuery(id+"F26.wireOp",EDGE,"E397.MirrorCS")}),-1.0]])]});
            var Q14;
            Q14=makeQuery(id+"F26.imprint","IMPRINT",FACE,{"disambiguationData":[TD([[makeQuery(id+"F26.imprint","IMPRINT",EDGE,{"derivedFrom":sQuery(id+"F26.wireOp",EDGE,"E401.MirrorCS")}),-1.0]])]});
            var Q15;
            Q15=makeQuery(id+"F26.imprint","IMPRINT",FACE,{"disambiguationData":[TD([[makeQuery(id+"F26.imprint","IMPRINT",EDGE,{"derivedFrom":sQuery(id+"F26.wireOp",EDGE,"E405.MirrorCS")}),-1.0]])]});
            var Q16;
            {var subQ0=sQuery(id+"F26.wireOp",EDGE,"E322.MirrorCS");Q16=makeQuery(id+"F26.imprint","IMPRINT",FACE,{"disambiguationData":[TD([[makeQuery(id+"F26.imprint","IMPRINT",EDGE,{"derivedFrom":subQ0}),-1.0]])]});}
            var Q17;
            {var subQ0=sQuery(id+"F26.wireOp",EDGE,"E326.MirrorCS");Q17=makeQuery(id+"F26.imprint","IMPRINT",FACE,{"disambiguationData":[TD([[makeQuery(id+"F26.imprint","IMPRINT",EDGE,{"derivedFrom":subQ0}),-1.0]])]});}
            var Q18;
            {var subQ0=sQuery(id+"F26.wireOp",EDGE,"E330.MirrorCS");Q18=makeQuery(id+"F26.imprint","IMPRINT",FACE,{"disambiguationData":[TD([[makeQuery(id+"F26.imprint","IMPRINT",EDGE,{"derivedFrom":subQ0}),1.0]])]});}
            var Q19;
            Q19=makeQuery(id+"F26.imprint","IMPRINT",FACE,{"disambiguationData":[TD([[makeQuery(id+"F26.imprint","IMPRINT",EDGE,{"derivedFrom":sQuery(id+"F26.wireOp",EDGE,"E333.top")}),-1.0]])]});
            var Q20;
            Q20=makeQuery(id+"F26.imprint","IMPRINT",FACE,{"disambiguationData":[TD([[makeQuery(id+"F26.imprint","IMPRINT",EDGE,{"derivedFrom":sQuery(id+"F26.wireOp",EDGE,"E318.bottom")}),-1.0]])]});
            var Q21;
            Q21=makeQuery(id+"F26.imprint","IMPRINT",FACE,{"disambiguationData":[TD([[makeQuery(id+"F26.imprint","IMPRINT",EDGE,{"derivedFrom":sQuery(id+"F26.wireOp",EDGE,"E320.bottom")}),-1.0]])]});
            var Q22;
            Q22=makeQuery(id+"F26.imprint","IMPRINT",FACE,{"disambiguationData":[TD([[makeQuery(id+"F26.imprint","IMPRINT",EDGE,{"derivedFrom":sQuery(id+"F26.wireOp",EDGE,"E372.bottom")}),1.0]])]});
            var Q23;
            Q23=makeQuery(id+"F26.imprint","IMPRINT",FACE,{"disambiguationData":[TD([[makeQuery(id+"F26.imprint","IMPRINT",EDGE,{"derivedFrom":sQuery(id+"F26.wireOp",EDGE,"E371.bottom")}),1.0]])]});
            var Q24;
            Q24=makeQuery(id+"F26.imprint","IMPRINT",FACE,{"disambiguationData":[TD([[makeQuery(id+"F26.imprint","IMPRINT",EDGE,{"derivedFrom":sQuery(id+"F26.wireOp",EDGE,"E370.bottom")}),1.0]])]});
            var Q25;
            Q25=makeQuery(id+"F26.imprint","IMPRINT",FACE,{"disambiguationData":[TD([[makeQuery(id+"F26.imprint","IMPRINT",EDGE,{"derivedFrom":sQuery(id+"F26.wireOp",EDGE,"E369.bottom")}),1.0]])]});
            var Q26;
            Q26=makeQuery(id+"F26.imprint","IMPRINT",FACE,{"disambiguationData":[TD([[makeQuery(id+"F26.imprint","IMPRINT",EDGE,{"derivedFrom":sQuery(id+"F26.wireOp",EDGE,"E368.bottom")}),1.0]])]});
            var Q27;
            Q27=makeQuery(id+"F26.imprint","IMPRINT",FACE,{"disambiguationData":[TD([[makeQuery(id+"F26.imprint","IMPRINT",EDGE,{"derivedFrom":sQuery(id+"F26.wireOp",EDGE,"E367.bottom")}),1.0]])]});
            var Q28;
            Q28=makeQuery(id+"F26.imprint","IMPRINT",FACE,{"disambiguationData":[TD([[makeQuery(id+"F26.imprint","IMPRINT",EDGE,{"derivedFrom":sQuery(id+"F26.wireOp",EDGE,"E366.bottom")}),1.0]])]});
            var Q29;
            Q29=makeQuery(id+"F26.imprint","IMPRINT",FACE,{"disambiguationData":[TD([[makeQuery(id+"F26.imprint","IMPRINT",EDGE,{"derivedFrom":sQuery(id+"F26.wireOp",EDGE,"E365.bottom")}),1.0]])]});
            var Q30;
            Q30=makeQuery(id+"F26.imprint","IMPRINT",FACE,{"disambiguationData":[TD([[makeQuery(id+"F26.imprint","IMPRINT",EDGE,{"derivedFrom":sQuery(id+"F26.wireOp",EDGE,"E364.bottom")}),1.0]])]});
            var Q31;
            Q31=makeQuery(id+"F26.imprint","IMPRINT",FACE,{"disambiguationData":[TD([[makeQuery(id+"F26.imprint","IMPRINT",EDGE,{"derivedFrom":sQuery(id+"F26.wireOp",EDGE,"E319.bottom")}),-1.0]])]});
            extrude(context, id + "F27", {"entities" : qUnion([Q0, Q1, Q2, Q3, Q4, Q5, Q6, Q7, Q8, Q9, Q10, Q11, Q12, Q13, Q14, Q15, Q16, Q17, Q18, Q19, Q20, Q21, Q22, Q23, Q24, Q25, Q26, Q27, Q28, Q29, Q30, Q31]), "operationType" : NewBodyOperationType.REMOVE, "oppositeDirection" : true, "depth" : 25 * mm});
        }
    });
